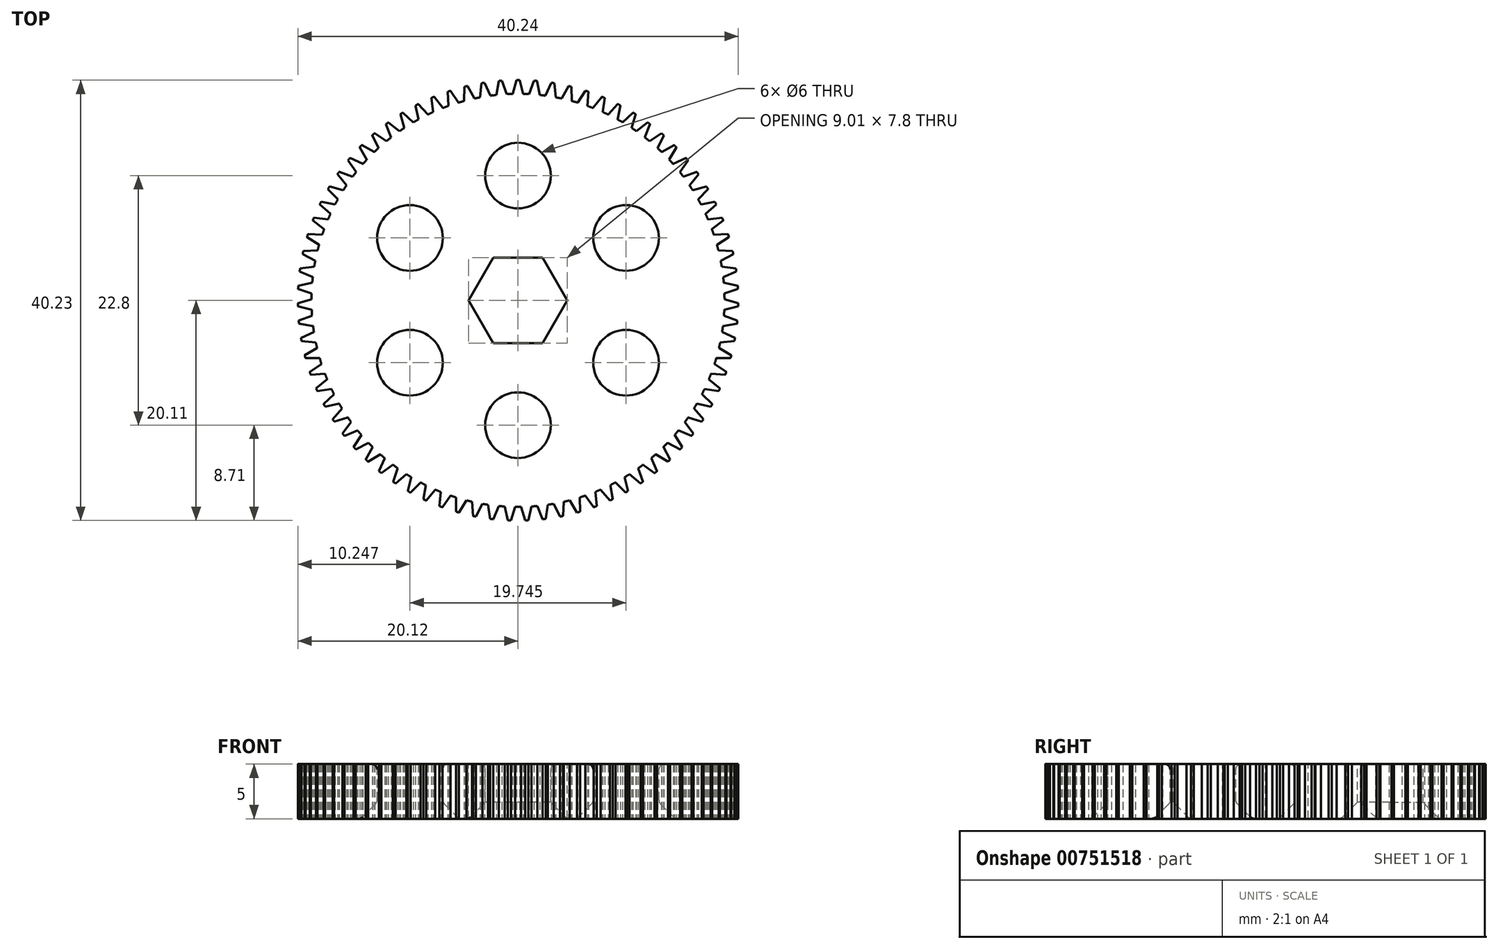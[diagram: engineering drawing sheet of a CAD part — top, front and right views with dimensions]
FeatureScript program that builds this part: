
annotation { "Feature Type Name" : "Feature", "Feature Type Description" : "" }
export const myFeature = defineFeature(function(context is Context, id is Id, definition is map)
    precondition{}
    {
        {
            assignVariable(context, id + "F0", {"name" : "GearHeight", "anyValue" : 5 * mm});
        }
        {
            assignVariable(context, id + "F1", {"name" : "teeth", "anyValue" : 79});
        }
        {
            var Q0;
            Q0=qCreatedBy(makeId("Top.planeOp"),FACE);
            var sketch = newSketch(context, id + "F2", { "sketchPlane" : qUnion([Q0])});
            skCircle(sketch, "E0", {"center": v(0, 0) * mm, "radius": 18.87 * mm});
            skCircle(sketch, "E1", {"center": v(0, 0) * mm, "radius": 20.12 * mm});
            skLineSegment(sketch, "E2", {"start": v(0.48, 18.86) * mm, "end": v(0.14, 20.12) * mm});
            skLineSegment(sketch, "E3", {"start": v(-0.48, 18.86) * mm, "end": v(-0.14, 20.12) * mm});
            skLineSegment(sketch, "E4", {"start": v(0, 0) * mm, "end": v(0, 64.06) * mm, "construction": true});
            skArc(sketch, "E5", {"start": v(-0.48, 18.86) * mm, "mid": v(-0.24, 18.87) * mm, "end": v(0, 18.87) * mm});
            skArc(sketch, "E6", {"start": v(0.48, 18.86) * mm, "mid": v(0.24, 18.87) * mm, "end": v(0, 18.87) * mm});
            skCircle(sketch, "E7", {"center": v(0, 0) * mm, "radius": 19.5 * mm, "construction": true});
            skPoint(sketch, "E8", {"position": v(-0.31, 19.5) * mm});
            skArc(sketch, "E9", {"start": v(0.14, 20.12) * mm, "mid": v(0.07, 20.12) * mm, "end": v(0, 20.12) * mm});
            skArc(sketch, "E10", {"start": v(-0.14, 20.12) * mm, "mid": v(-0.07, 20.12) * mm, "end": v(0, 20.12) * mm});
            skPoint(sketch, "E11", {"position": v(0.31, 19.5) * mm});
            skSolve(sketch);
        }
        {
            var Q0;
            Q0=qCreatedBy(makeId("Right.planeOp"),FACE);
            var sketch = newSketch(context, id + "F3", { "sketchPlane" : qUnion([Q0])});
            skLineSegment(sketch, "E12", {"start": v(0, 16.96) * mm, "end": v(0, -9.96) * mm, "construction": true});
            skSolve(sketch);
        }
        {
            var Q0;
            {var subQ0=sQuery(id+"F2.wireOp",EDGE,"E0");var subQ1=makeQuery(id+"F2.imprint","INTERSECT",VERTEX,{"derivedFrom":[subQ0,sQuery(id+"F2.wireOp",EDGE,"E2")]});Q0=makeQuery(id+"F2.imprint","IMPRINT",FACE,{"disambiguationData":[TD([[makeQuery(id+"F2.imprint","IMPRINT",EDGE,{"disambiguationData":[TD([[subQ1,-1.0]])],"derivedFrom":subQ0}),1.0]])]});}
            extrude(context, id + "F4", {"entities" : qUnion([Q0]), "depth" : getVariable(context, 'GearHeight'), "offsetDistance" : 25 * mm});
        }
        {
            var Q0;
            {var subQ0=sQuery(id+"F2.wireOp",EDGE,"E2");Q0=makeQuery(id+"F2.imprint","IMPRINT",FACE,{"disambiguationData":[TD([[makeQuery(id+"F2.imprint","IMPRINT",EDGE,{"derivedFrom":subQ0}),1.0]])]});}
            extrude(context, id + "F5", {"entities" : qUnion([Q0]), "operationType" : NewBodyOperationType.ADD, "depth" : getVariable(context, 'GearHeight'), "offsetDistance" : 25 * mm});
        }
        {
            var Q0;
            Q0=makeQuery(id+"F4.opExtrude","SWEPT_BODY",BODY,{"disambiguationData":[OSD([sQuery(id+"F2.wireOp",EDGE,"E0")])]});
            var Q1;
            Q1=sQuery(id+"F3.wireOp",EDGE,"E12");
            circularPattern(context, id + "F6", {"operationType" : NewBodyOperationType.ADD, "entities" : qUnion([Q0]), "axis" : qUnion([Q1]), "angle" : 360 * degree, "instanceCount" : getVariable(context, 'teeth'), "equalSpace" : true});
        }
        {
            var Q0;
            {var subQ0=sQuery(id+"F2.wireOp",EDGE,"E0");var subQ1=makeQuery(id+"F5.boolean.opBoolean","MERGE",FACE,{"derivedFrom":[makeQuery(id+"F4.opExtrude","CAP_FACE",FACE,{"disambiguationData":[OSD([subQ0])],"isStart":false}),makeQuery(id+"F5.opExtrude","CAP_FACE",FACE,{"disambiguationData":[OSD([subQ0,sQuery(id+"F2.wireOp",EDGE,"E1"),sQuery(id+"F2.wireOp",EDGE,"E2"),sQuery(id+"F2.wireOp",EDGE,"E3")])],"isStart":false})]});Q0=makeQuery(id+"F6.boolean.opBoolean","MERGE",FACE,{"derivedFrom":[subQ1,makeQuery(id+"F6.opPattern","COPY",FACE,{"derivedFrom":subQ1,"instanceName":"1"}),makeQuery(id+"F6.opPattern","COPY",FACE,{"derivedFrom":subQ1,"instanceName":"2"}),makeQuery(id+"F6.opPattern","COPY",FACE,{"derivedFrom":subQ1,"instanceName":"3"}),makeQuery(id+"F6.opPattern","COPY",FACE,{"derivedFrom":subQ1,"instanceName":"4"}),makeQuery(id+"F6.opPattern","COPY",FACE,{"derivedFrom":subQ1,"instanceName":"5"}),makeQuery(id+"F6.opPattern","COPY",FACE,{"derivedFrom":subQ1,"instanceName":"6"}),makeQuery(id+"F6.opPattern","COPY",FACE,{"derivedFrom":subQ1,"instanceName":"7"}),makeQuery(id+"F6.opPattern","COPY",FACE,{"derivedFrom":subQ1,"instanceName":"8"}),makeQuery(id+"F6.opPattern","COPY",FACE,{"derivedFrom":subQ1,"instanceName":"9"}),makeQuery(id+"F6.opPattern","COPY",FACE,{"derivedFrom":subQ1,"instanceName":"10"}),makeQuery(id+"F6.opPattern","COPY",FACE,{"derivedFrom":subQ1,"instanceName":"11"}),makeQuery(id+"F6.opPattern","COPY",FACE,{"derivedFrom":subQ1,"instanceName":"12"}),makeQuery(id+"F6.opPattern","COPY",FACE,{"derivedFrom":subQ1,"instanceName":"13"}),makeQuery(id+"F6.opPattern","COPY",FACE,{"derivedFrom":subQ1,"instanceName":"14"}),makeQuery(id+"F6.opPattern","COPY",FACE,{"derivedFrom":subQ1,"instanceName":"15"}),makeQuery(id+"F6.opPattern","COPY",FACE,{"derivedFrom":subQ1,"instanceName":"16"}),makeQuery(id+"F6.opPattern","COPY",FACE,{"derivedFrom":subQ1,"instanceName":"17"}),makeQuery(id+"F6.opPattern","COPY",FACE,{"derivedFrom":subQ1,"instanceName":"18"}),makeQuery(id+"F6.opPattern","COPY",FACE,{"derivedFrom":subQ1,"instanceName":"19"}),makeQuery(id+"F6.opPattern","COPY",FACE,{"derivedFrom":subQ1,"instanceName":"20"}),makeQuery(id+"F6.opPattern","COPY",FACE,{"derivedFrom":subQ1,"instanceName":"21"}),makeQuery(id+"F6.opPattern","COPY",FACE,{"derivedFrom":subQ1,"instanceName":"22"}),makeQuery(id+"F6.opPattern","COPY",FACE,{"derivedFrom":subQ1,"instanceName":"23"}),makeQuery(id+"F6.opPattern","COPY",FACE,{"derivedFrom":subQ1,"instanceName":"24"})]});}
            var sketch = newSketch(context, id + "F7", { "sketchPlane" : qUnion([Q0])});
            skCircle(sketch, "E13.cCircle", {"center": v(0, 0) * mm, "radius": 3.9 * mm, "construction": true});
            skLineSegment(sketch, "E13.0", {"start": v(-2.25, 3.9) * mm, "end": v(2.25, 3.9) * mm});
            skLineSegment(sketch, "E13.1", {"start": v(2.25, 3.9) * mm, "end": v(4.5, 0) * mm});
            skLineSegment(sketch, "E13.2", {"start": v(4.5, 0) * mm, "end": v(2.25, -3.9) * mm});
            skLineSegment(sketch, "E13.3", {"start": v(2.25, -3.9) * mm, "end": v(-2.25, -3.9) * mm});
            skLineSegment(sketch, "E13.4", {"start": v(-2.25, -3.9) * mm, "end": v(-4.5, 0) * mm});
            skLineSegment(sketch, "E13.5", {"start": v(-4.5, 0) * mm, "end": v(-2.25, 3.9) * mm});
            skPoint(sketch, "E13.0.midPoint", {"position": v(0, 3.9) * mm});
            skCircle(sketch, "E14", {"center": v(0, 11.4) * mm, "radius": 3 * mm});
            skCircle(sketch, "E15.1.0", {"center": v(-9.87, 5.7) * mm, "radius": 3 * mm});
            skCircle(sketch, "E15.2.0", {"center": v(-9.87, -5.7) * mm, "radius": 3 * mm});
            skCircle(sketch, "E16.1.3.0", {"center": v(0, -11.4) * mm, "radius": 3 * mm});
            skCircle(sketch, "E16.1.4.0", {"center": v(9.87, -5.7) * mm, "radius": 3 * mm});
            skCircle(sketch, "E16.1.5.0", {"center": v(9.87, 5.7) * mm, "radius": 3 * mm});
            skSolve(sketch);
        }
        {
            var Q0;
            Q0=makeQuery(id+"F7.imprint","IMPRINT",FACE,{"disambiguationData":[TD([[makeQuery(id+"F7.imprint","IMPRINT",EDGE,{"derivedFrom":sQuery(id+"F7.wireOp",EDGE,"E13.0")}),-1.0]])]});
            var Q1;
            Q1=makeQuery(id+"F7.imprint","IMPRINT",FACE,{"disambiguationData":[TD([[makeQuery(id+"F7.imprint","IMPRINT",EDGE,{"derivedFrom":sQuery(id+"F7.wireOp",EDGE,"E14")}),1.0]])]});
            var Q2;
            Q2=makeQuery(id+"F7.imprint","IMPRINT",FACE,{"disambiguationData":[TD([[makeQuery(id+"F7.imprint","IMPRINT",EDGE,{"derivedFrom":sQuery(id+"F7.wireOp",EDGE,"E15.1.0")}),1.0]])]});
            var Q3;
            Q3=makeQuery(id+"F7.imprint","IMPRINT",FACE,{"disambiguationData":[TD([[makeQuery(id+"F7.imprint","IMPRINT",EDGE,{"derivedFrom":sQuery(id+"F7.wireOp",EDGE,"E15.2.0")}),1.0]])]});
            var Q4;
            Q4=makeQuery(id+"F7.imprint","IMPRINT",FACE,{"disambiguationData":[TD([[makeQuery(id+"F7.imprint","IMPRINT",EDGE,{"derivedFrom":sQuery(id+"F7.wireOp",EDGE,"E16.1.3.0")}),1.0]])]});
            var Q5;
            Q5=makeQuery(id+"F7.imprint","IMPRINT",FACE,{"disambiguationData":[TD([[makeQuery(id+"F7.imprint","IMPRINT",EDGE,{"derivedFrom":sQuery(id+"F7.wireOp",EDGE,"E16.1.4.0")}),1.0]])]});
            var Q6;
            Q6=makeQuery(id+"F7.imprint","IMPRINT",FACE,{"disambiguationData":[TD([[makeQuery(id+"F7.imprint","IMPRINT",EDGE,{"derivedFrom":sQuery(id+"F7.wireOp",EDGE,"E16.1.5.0")}),1.0]])]});
            extrude(context, id + "F8", {"entities" : qUnion([Q0, Q1, Q2, Q3, Q4, Q5, Q6]), "operationType" : NewBodyOperationType.REMOVE, "endBound" : BoundingType.THROUGH_ALL, "oppositeDirection" : true, "depth" : 25 * mm, "offsetDistance" : 25 * mm});
        }
        {
            var Q0;
            Q0=makeQuery(id+"F8.boolean.opBoolean","COPY",EDGE,{"derivedFrom":makeQuery(id+"F8.opExtrude","CAP_EDGE",EDGE,{"disambiguationData":[OSD([sQuery(id+"F7.wireOp",EDGE,"E14")])],"isStart":true})});
            var Q1;
            Q1=makeQuery(id+"F8.boolean.opBoolean","COPY",EDGE,{"derivedFrom":makeQuery(id+"F8.opExtrude","CAP_EDGE",EDGE,{"disambiguationData":[OSD([sQuery(id+"F7.wireOp",EDGE,"E15.1.0")])],"isStart":true})});
            var Q2;
            Q2=makeQuery(id+"F8.boolean.opBoolean","COPY",EDGE,{"derivedFrom":makeQuery(id+"F8.opExtrude","CAP_EDGE",EDGE,{"disambiguationData":[OSD([sQuery(id+"F7.wireOp",EDGE,"E16.1.5.0")])],"isStart":true})});
            var Q3;
            Q3=makeQuery(id+"F8.boolean.opBoolean","COPY",EDGE,{"derivedFrom":makeQuery(id+"F8.opExtrude","CAP_EDGE",EDGE,{"disambiguationData":[OSD([sQuery(id+"F7.wireOp",EDGE,"E16.1.4.0")])],"isStart":true})});
            var Q4;
            Q4=makeQuery(id+"F8.boolean.opBoolean","COPY",EDGE,{"derivedFrom":makeQuery(id+"F8.opExtrude","CAP_EDGE",EDGE,{"disambiguationData":[OSD([sQuery(id+"F7.wireOp",EDGE,"E16.1.3.0")])],"isStart":true})});
            var Q5;
            Q5=makeQuery(id+"F8.boolean.opBoolean","COPY",EDGE,{"derivedFrom":makeQuery(id+"F8.opExtrude","CAP_EDGE",EDGE,{"disambiguationData":[OSD([sQuery(id+"F7.wireOp",EDGE,"E15.2.0")])],"isStart":true})});
            var Q6;
            {var subQ0=sQuery(id+"F2.wireOp",EDGE,"E0");var subQ1=makeQuery(id+"F5.boolean.opBoolean","MERGE",FACE,{"derivedFrom":[makeQuery(id+"F4.opExtrude","CAP_FACE",FACE,{"disambiguationData":[OSD([subQ0])],"isStart":true}),makeQuery(id+"F5.opExtrude","CAP_FACE",FACE,{"disambiguationData":[OSD([subQ0,sQuery(id+"F2.wireOp",EDGE,"E1"),sQuery(id+"F2.wireOp",EDGE,"E2"),sQuery(id+"F2.wireOp",EDGE,"E3")])],"isStart":true})]});Q6=makeQuery(id+"F8.boolean.opBoolean","INTERSECT",EDGE,{"derivedFrom":[makeQuery(id+"F6.boolean.opBoolean","MERGE",FACE,{"derivedFrom":[subQ1,makeQuery(id+"F6.opPattern","COPY",FACE,{"derivedFrom":subQ1,"instanceName":"1"}),makeQuery(id+"F6.opPattern","COPY",FACE,{"derivedFrom":subQ1,"instanceName":"2"}),makeQuery(id+"F6.opPattern","COPY",FACE,{"derivedFrom":subQ1,"instanceName":"3"}),makeQuery(id+"F6.opPattern","COPY",FACE,{"derivedFrom":subQ1,"instanceName":"4"}),makeQuery(id+"F6.opPattern","COPY",FACE,{"derivedFrom":subQ1,"instanceName":"5"}),makeQuery(id+"F6.opPattern","COPY",FACE,{"derivedFrom":subQ1,"instanceName":"6"}),makeQuery(id+"F6.opPattern","COPY",FACE,{"derivedFrom":subQ1,"instanceName":"7"}),makeQuery(id+"F6.opPattern","COPY",FACE,{"derivedFrom":subQ1,"instanceName":"8"}),makeQuery(id+"F6.opPattern","COPY",FACE,{"derivedFrom":subQ1,"instanceName":"9"}),makeQuery(id+"F6.opPattern","COPY",FACE,{"derivedFrom":subQ1,"instanceName":"10"}),makeQuery(id+"F6.opPattern","COPY",FACE,{"derivedFrom":subQ1,"instanceName":"11"}),makeQuery(id+"F6.opPattern","COPY",FACE,{"derivedFrom":subQ1,"instanceName":"12"}),makeQuery(id+"F6.opPattern","COPY",FACE,{"derivedFrom":subQ1,"instanceName":"13"}),makeQuery(id+"F6.opPattern","COPY",FACE,{"derivedFrom":subQ1,"instanceName":"14"}),makeQuery(id+"F6.opPattern","COPY",FACE,{"derivedFrom":subQ1,"instanceName":"15"}),makeQuery(id+"F6.opPattern","COPY",FACE,{"derivedFrom":subQ1,"instanceName":"16"}),makeQuery(id+"F6.opPattern","COPY",FACE,{"derivedFrom":subQ1,"instanceName":"17"}),makeQuery(id+"F6.opPattern","COPY",FACE,{"derivedFrom":subQ1,"instanceName":"18"}),makeQuery(id+"F6.opPattern","COPY",FACE,{"derivedFrom":subQ1,"instanceName":"19"}),makeQuery(id+"F6.opPattern","COPY",FACE,{"derivedFrom":subQ1,"instanceName":"20"}),makeQuery(id+"F6.opPattern","COPY",FACE,{"derivedFrom":subQ1,"instanceName":"21"}),makeQuery(id+"F6.opPattern","COPY",FACE,{"derivedFrom":subQ1,"instanceName":"22"}),makeQuery(id+"F6.opPattern","COPY",FACE,{"derivedFrom":subQ1,"instanceName":"23"}),makeQuery(id+"F6.opPattern","COPY",FACE,{"derivedFrom":subQ1,"instanceName":"24"}),makeQuery(id+"F6.opPattern","COPY",FACE,{"derivedFrom":subQ1,"instanceName":"25"}),makeQuery(id+"F6.opPattern","COPY",FACE,{"derivedFrom":subQ1,"instanceName":"26"}),makeQuery(id+"F6.opPattern","COPY",FACE,{"derivedFrom":subQ1,"instanceName":"27"}),makeQuery(id+"F6.opPattern","COPY",FACE,{"derivedFrom":subQ1,"instanceName":"28"}),makeQuery(id+"F6.opPattern","COPY",FACE,{"derivedFrom":subQ1,"instanceName":"29"}),makeQuery(id+"F6.opPattern","COPY",FACE,{"derivedFrom":subQ1,"instanceName":"30"}),makeQuery(id+"F6.opPattern","COPY",FACE,{"derivedFrom":subQ1,"instanceName":"31"}),makeQuery(id+"F6.opPattern","COPY",FACE,{"derivedFrom":subQ1,"instanceName":"32"}),makeQuery(id+"F6.opPattern","COPY",FACE,{"derivedFrom":subQ1,"instanceName":"33"}),makeQuery(id+"F6.opPattern","COPY",FACE,{"derivedFrom":subQ1,"instanceName":"34"}),makeQuery(id+"F6.opPattern","COPY",FACE,{"derivedFrom":subQ1,"instanceName":"35"}),makeQuery(id+"F6.opPattern","COPY",FACE,{"derivedFrom":subQ1,"instanceName":"36"}),makeQuery(id+"F6.opPattern","COPY",FACE,{"derivedFrom":subQ1,"instanceName":"37"}),makeQuery(id+"F6.opPattern","COPY",FACE,{"derivedFrom":subQ1,"instanceName":"38"}),makeQuery(id+"F6.opPattern","COPY",FACE,{"derivedFrom":subQ1,"instanceName":"39"}),makeQuery(id+"F6.opPattern","COPY",FACE,{"derivedFrom":subQ1,"instanceName":"40"}),makeQuery(id+"F6.opPattern","COPY",FACE,{"derivedFrom":subQ1,"instanceName":"41"}),makeQuery(id+"F6.opPattern","COPY",FACE,{"derivedFrom":subQ1,"instanceName":"42"}),makeQuery(id+"F6.opPattern","COPY",FACE,{"derivedFrom":subQ1,"instanceName":"43"}),makeQuery(id+"F6.opPattern","COPY",FACE,{"derivedFrom":subQ1,"instanceName":"44"}),makeQuery(id+"F6.opPattern","COPY",FACE,{"derivedFrom":subQ1,"instanceName":"45"}),makeQuery(id+"F6.opPattern","COPY",FACE,{"derivedFrom":subQ1,"instanceName":"46"}),makeQuery(id+"F6.opPattern","COPY",FACE,{"derivedFrom":subQ1,"instanceName":"47"}),makeQuery(id+"F6.opPattern","COPY",FACE,{"derivedFrom":subQ1,"instanceName":"48"}),makeQuery(id+"F6.opPattern","COPY",FACE,{"derivedFrom":subQ1,"instanceName":"49"}),makeQuery(id+"F6.opPattern","COPY",FACE,{"derivedFrom":subQ1,"instanceName":"50"}),makeQuery(id+"F6.opPattern","COPY",FACE,{"derivedFrom":subQ1,"instanceName":"51"}),makeQuery(id+"F6.opPattern","COPY",FACE,{"derivedFrom":subQ1,"instanceName":"52"}),makeQuery(id+"F6.opPattern","COPY",FACE,{"derivedFrom":subQ1,"instanceName":"53"}),makeQuery(id+"F6.opPattern","COPY",FACE,{"derivedFrom":subQ1,"instanceName":"54"}),makeQuery(id+"F6.opPattern","COPY",FACE,{"derivedFrom":subQ1,"instanceName":"55"}),makeQuery(id+"F6.opPattern","COPY",FACE,{"derivedFrom":subQ1,"instanceName":"56"}),makeQuery(id+"F6.opPattern","COPY",FACE,{"derivedFrom":subQ1,"instanceName":"57"}),makeQuery(id+"F6.opPattern","COPY",FACE,{"derivedFrom":subQ1,"instanceName":"58"}),makeQuery(id+"F6.opPattern","COPY",FACE,{"derivedFrom":subQ1,"instanceName":"59"}),makeQuery(id+"F6.opPattern","COPY",FACE,{"derivedFrom":subQ1,"instanceName":"60"}),makeQuery(id+"F6.opPattern","COPY",FACE,{"derivedFrom":subQ1,"instanceName":"61"}),makeQuery(id+"F6.opPattern","COPY",FACE,{"derivedFrom":subQ1,"instanceName":"62"}),makeQuery(id+"F6.opPattern","COPY",FACE,{"derivedFrom":subQ1,"instanceName":"63"}),makeQuery(id+"F6.opPattern","COPY",FACE,{"derivedFrom":subQ1,"instanceName":"64"}),makeQuery(id+"F6.opPattern","COPY",FACE,{"derivedFrom":subQ1,"instanceName":"65"}),makeQuery(id+"F6.opPattern","COPY",FACE,{"derivedFrom":subQ1,"instanceName":"66"}),makeQuery(id+"F6.opPattern","COPY",FACE,{"derivedFrom":subQ1,"instanceName":"67"}),makeQuery(id+"F6.opPattern","COPY",FACE,{"derivedFrom":subQ1,"instanceName":"68"}),makeQuery(id+"F6.opPattern","COPY",FACE,{"derivedFrom":subQ1,"instanceName":"69"}),makeQuery(id+"F6.opPattern","COPY",FACE,{"derivedFrom":subQ1,"instanceName":"70"}),makeQuery(id+"F6.opPattern","COPY",FACE,{"derivedFrom":subQ1,"instanceName":"71"}),makeQuery(id+"F6.opPattern","COPY",FACE,{"derivedFrom":subQ1,"instanceName":"72"}),makeQuery(id+"F6.opPattern","COPY",FACE,{"derivedFrom":subQ1,"instanceName":"73"}),makeQuery(id+"F6.opPattern","COPY",FACE,{"derivedFrom":subQ1,"instanceName":"74"}),makeQuery(id+"F6.opPattern","COPY",FACE,{"derivedFrom":subQ1,"instanceName":"75"}),makeQuery(id+"F6.opPattern","COPY",FACE,{"derivedFrom":subQ1,"instanceName":"76"}),makeQuery(id+"F6.opPattern","COPY",FACE,{"derivedFrom":subQ1,"instanceName":"77"}),makeQuery(id+"F6.opPattern","COPY",FACE,{"derivedFrom":subQ1,"instanceName":"78"})]}),makeQuery(id+"F8.opExtrude","SWEPT_FACE",FACE,{"disambiguationData":[OSD([sQuery(id+"F7.wireOp",EDGE,"E16.1.3.0")])]})]});}
            var Q7;
            {var subQ0=sQuery(id+"F2.wireOp",EDGE,"E0");var subQ1=makeQuery(id+"F5.boolean.opBoolean","MERGE",FACE,{"derivedFrom":[makeQuery(id+"F4.opExtrude","CAP_FACE",FACE,{"disambiguationData":[OSD([subQ0])],"isStart":true}),makeQuery(id+"F5.opExtrude","CAP_FACE",FACE,{"disambiguationData":[OSD([subQ0,sQuery(id+"F2.wireOp",EDGE,"E1"),sQuery(id+"F2.wireOp",EDGE,"E2"),sQuery(id+"F2.wireOp",EDGE,"E3")])],"isStart":true})]});Q7=makeQuery(id+"F8.boolean.opBoolean","INTERSECT",EDGE,{"derivedFrom":[makeQuery(id+"F6.boolean.opBoolean","MERGE",FACE,{"derivedFrom":[subQ1,makeQuery(id+"F6.opPattern","COPY",FACE,{"derivedFrom":subQ1,"instanceName":"1"}),makeQuery(id+"F6.opPattern","COPY",FACE,{"derivedFrom":subQ1,"instanceName":"2"}),makeQuery(id+"F6.opPattern","COPY",FACE,{"derivedFrom":subQ1,"instanceName":"3"}),makeQuery(id+"F6.opPattern","COPY",FACE,{"derivedFrom":subQ1,"instanceName":"4"}),makeQuery(id+"F6.opPattern","COPY",FACE,{"derivedFrom":subQ1,"instanceName":"5"}),makeQuery(id+"F6.opPattern","COPY",FACE,{"derivedFrom":subQ1,"instanceName":"6"}),makeQuery(id+"F6.opPattern","COPY",FACE,{"derivedFrom":subQ1,"instanceName":"7"}),makeQuery(id+"F6.opPattern","COPY",FACE,{"derivedFrom":subQ1,"instanceName":"8"}),makeQuery(id+"F6.opPattern","COPY",FACE,{"derivedFrom":subQ1,"instanceName":"9"}),makeQuery(id+"F6.opPattern","COPY",FACE,{"derivedFrom":subQ1,"instanceName":"10"}),makeQuery(id+"F6.opPattern","COPY",FACE,{"derivedFrom":subQ1,"instanceName":"11"}),makeQuery(id+"F6.opPattern","COPY",FACE,{"derivedFrom":subQ1,"instanceName":"12"}),makeQuery(id+"F6.opPattern","COPY",FACE,{"derivedFrom":subQ1,"instanceName":"13"}),makeQuery(id+"F6.opPattern","COPY",FACE,{"derivedFrom":subQ1,"instanceName":"14"}),makeQuery(id+"F6.opPattern","COPY",FACE,{"derivedFrom":subQ1,"instanceName":"15"}),makeQuery(id+"F6.opPattern","COPY",FACE,{"derivedFrom":subQ1,"instanceName":"16"}),makeQuery(id+"F6.opPattern","COPY",FACE,{"derivedFrom":subQ1,"instanceName":"17"}),makeQuery(id+"F6.opPattern","COPY",FACE,{"derivedFrom":subQ1,"instanceName":"18"}),makeQuery(id+"F6.opPattern","COPY",FACE,{"derivedFrom":subQ1,"instanceName":"19"}),makeQuery(id+"F6.opPattern","COPY",FACE,{"derivedFrom":subQ1,"instanceName":"20"}),makeQuery(id+"F6.opPattern","COPY",FACE,{"derivedFrom":subQ1,"instanceName":"21"}),makeQuery(id+"F6.opPattern","COPY",FACE,{"derivedFrom":subQ1,"instanceName":"22"}),makeQuery(id+"F6.opPattern","COPY",FACE,{"derivedFrom":subQ1,"instanceName":"23"}),makeQuery(id+"F6.opPattern","COPY",FACE,{"derivedFrom":subQ1,"instanceName":"24"}),makeQuery(id+"F6.opPattern","COPY",FACE,{"derivedFrom":subQ1,"instanceName":"25"}),makeQuery(id+"F6.opPattern","COPY",FACE,{"derivedFrom":subQ1,"instanceName":"26"}),makeQuery(id+"F6.opPattern","COPY",FACE,{"derivedFrom":subQ1,"instanceName":"27"}),makeQuery(id+"F6.opPattern","COPY",FACE,{"derivedFrom":subQ1,"instanceName":"28"}),makeQuery(id+"F6.opPattern","COPY",FACE,{"derivedFrom":subQ1,"instanceName":"29"}),makeQuery(id+"F6.opPattern","COPY",FACE,{"derivedFrom":subQ1,"instanceName":"30"}),makeQuery(id+"F6.opPattern","COPY",FACE,{"derivedFrom":subQ1,"instanceName":"31"}),makeQuery(id+"F6.opPattern","COPY",FACE,{"derivedFrom":subQ1,"instanceName":"32"}),makeQuery(id+"F6.opPattern","COPY",FACE,{"derivedFrom":subQ1,"instanceName":"33"}),makeQuery(id+"F6.opPattern","COPY",FACE,{"derivedFrom":subQ1,"instanceName":"34"}),makeQuery(id+"F6.opPattern","COPY",FACE,{"derivedFrom":subQ1,"instanceName":"35"}),makeQuery(id+"F6.opPattern","COPY",FACE,{"derivedFrom":subQ1,"instanceName":"36"}),makeQuery(id+"F6.opPattern","COPY",FACE,{"derivedFrom":subQ1,"instanceName":"37"}),makeQuery(id+"F6.opPattern","COPY",FACE,{"derivedFrom":subQ1,"instanceName":"38"}),makeQuery(id+"F6.opPattern","COPY",FACE,{"derivedFrom":subQ1,"instanceName":"39"}),makeQuery(id+"F6.opPattern","COPY",FACE,{"derivedFrom":subQ1,"instanceName":"40"}),makeQuery(id+"F6.opPattern","COPY",FACE,{"derivedFrom":subQ1,"instanceName":"41"}),makeQuery(id+"F6.opPattern","COPY",FACE,{"derivedFrom":subQ1,"instanceName":"42"}),makeQuery(id+"F6.opPattern","COPY",FACE,{"derivedFrom":subQ1,"instanceName":"43"}),makeQuery(id+"F6.opPattern","COPY",FACE,{"derivedFrom":subQ1,"instanceName":"44"}),makeQuery(id+"F6.opPattern","COPY",FACE,{"derivedFrom":subQ1,"instanceName":"45"}),makeQuery(id+"F6.opPattern","COPY",FACE,{"derivedFrom":subQ1,"instanceName":"46"}),makeQuery(id+"F6.opPattern","COPY",FACE,{"derivedFrom":subQ1,"instanceName":"47"}),makeQuery(id+"F6.opPattern","COPY",FACE,{"derivedFrom":subQ1,"instanceName":"48"}),makeQuery(id+"F6.opPattern","COPY",FACE,{"derivedFrom":subQ1,"instanceName":"49"}),makeQuery(id+"F6.opPattern","COPY",FACE,{"derivedFrom":subQ1,"instanceName":"50"}),makeQuery(id+"F6.opPattern","COPY",FACE,{"derivedFrom":subQ1,"instanceName":"51"}),makeQuery(id+"F6.opPattern","COPY",FACE,{"derivedFrom":subQ1,"instanceName":"52"}),makeQuery(id+"F6.opPattern","COPY",FACE,{"derivedFrom":subQ1,"instanceName":"53"}),makeQuery(id+"F6.opPattern","COPY",FACE,{"derivedFrom":subQ1,"instanceName":"54"}),makeQuery(id+"F6.opPattern","COPY",FACE,{"derivedFrom":subQ1,"instanceName":"55"}),makeQuery(id+"F6.opPattern","COPY",FACE,{"derivedFrom":subQ1,"instanceName":"56"}),makeQuery(id+"F6.opPattern","COPY",FACE,{"derivedFrom":subQ1,"instanceName":"57"}),makeQuery(id+"F6.opPattern","COPY",FACE,{"derivedFrom":subQ1,"instanceName":"58"}),makeQuery(id+"F6.opPattern","COPY",FACE,{"derivedFrom":subQ1,"instanceName":"59"}),makeQuery(id+"F6.opPattern","COPY",FACE,{"derivedFrom":subQ1,"instanceName":"60"}),makeQuery(id+"F6.opPattern","COPY",FACE,{"derivedFrom":subQ1,"instanceName":"61"}),makeQuery(id+"F6.opPattern","COPY",FACE,{"derivedFrom":subQ1,"instanceName":"62"}),makeQuery(id+"F6.opPattern","COPY",FACE,{"derivedFrom":subQ1,"instanceName":"63"}),makeQuery(id+"F6.opPattern","COPY",FACE,{"derivedFrom":subQ1,"instanceName":"64"}),makeQuery(id+"F6.opPattern","COPY",FACE,{"derivedFrom":subQ1,"instanceName":"65"}),makeQuery(id+"F6.opPattern","COPY",FACE,{"derivedFrom":subQ1,"instanceName":"66"}),makeQuery(id+"F6.opPattern","COPY",FACE,{"derivedFrom":subQ1,"instanceName":"67"}),makeQuery(id+"F6.opPattern","COPY",FACE,{"derivedFrom":subQ1,"instanceName":"68"}),makeQuery(id+"F6.opPattern","COPY",FACE,{"derivedFrom":subQ1,"instanceName":"69"}),makeQuery(id+"F6.opPattern","COPY",FACE,{"derivedFrom":subQ1,"instanceName":"70"}),makeQuery(id+"F6.opPattern","COPY",FACE,{"derivedFrom":subQ1,"instanceName":"71"}),makeQuery(id+"F6.opPattern","COPY",FACE,{"derivedFrom":subQ1,"instanceName":"72"}),makeQuery(id+"F6.opPattern","COPY",FACE,{"derivedFrom":subQ1,"instanceName":"73"}),makeQuery(id+"F6.opPattern","COPY",FACE,{"derivedFrom":subQ1,"instanceName":"74"}),makeQuery(id+"F6.opPattern","COPY",FACE,{"derivedFrom":subQ1,"instanceName":"75"}),makeQuery(id+"F6.opPattern","COPY",FACE,{"derivedFrom":subQ1,"instanceName":"76"}),makeQuery(id+"F6.opPattern","COPY",FACE,{"derivedFrom":subQ1,"instanceName":"77"}),makeQuery(id+"F6.opPattern","COPY",FACE,{"derivedFrom":subQ1,"instanceName":"78"})]}),makeQuery(id+"F8.opExtrude","SWEPT_FACE",FACE,{"disambiguationData":[OSD([sQuery(id+"F7.wireOp",EDGE,"E15.2.0")])]})]});}
            var Q8;
            {var subQ0=sQuery(id+"F2.wireOp",EDGE,"E0");var subQ1=makeQuery(id+"F5.boolean.opBoolean","MERGE",FACE,{"derivedFrom":[makeQuery(id+"F4.opExtrude","CAP_FACE",FACE,{"disambiguationData":[OSD([subQ0])],"isStart":true}),makeQuery(id+"F5.opExtrude","CAP_FACE",FACE,{"disambiguationData":[OSD([subQ0,sQuery(id+"F2.wireOp",EDGE,"E1"),sQuery(id+"F2.wireOp",EDGE,"E2"),sQuery(id+"F2.wireOp",EDGE,"E3")])],"isStart":true})]});Q8=makeQuery(id+"F8.boolean.opBoolean","INTERSECT",EDGE,{"derivedFrom":[makeQuery(id+"F6.boolean.opBoolean","MERGE",FACE,{"derivedFrom":[subQ1,makeQuery(id+"F6.opPattern","COPY",FACE,{"derivedFrom":subQ1,"instanceName":"1"}),makeQuery(id+"F6.opPattern","COPY",FACE,{"derivedFrom":subQ1,"instanceName":"2"}),makeQuery(id+"F6.opPattern","COPY",FACE,{"derivedFrom":subQ1,"instanceName":"3"}),makeQuery(id+"F6.opPattern","COPY",FACE,{"derivedFrom":subQ1,"instanceName":"4"}),makeQuery(id+"F6.opPattern","COPY",FACE,{"derivedFrom":subQ1,"instanceName":"5"}),makeQuery(id+"F6.opPattern","COPY",FACE,{"derivedFrom":subQ1,"instanceName":"6"}),makeQuery(id+"F6.opPattern","COPY",FACE,{"derivedFrom":subQ1,"instanceName":"7"}),makeQuery(id+"F6.opPattern","COPY",FACE,{"derivedFrom":subQ1,"instanceName":"8"}),makeQuery(id+"F6.opPattern","COPY",FACE,{"derivedFrom":subQ1,"instanceName":"9"}),makeQuery(id+"F6.opPattern","COPY",FACE,{"derivedFrom":subQ1,"instanceName":"10"}),makeQuery(id+"F6.opPattern","COPY",FACE,{"derivedFrom":subQ1,"instanceName":"11"}),makeQuery(id+"F6.opPattern","COPY",FACE,{"derivedFrom":subQ1,"instanceName":"12"}),makeQuery(id+"F6.opPattern","COPY",FACE,{"derivedFrom":subQ1,"instanceName":"13"}),makeQuery(id+"F6.opPattern","COPY",FACE,{"derivedFrom":subQ1,"instanceName":"14"}),makeQuery(id+"F6.opPattern","COPY",FACE,{"derivedFrom":subQ1,"instanceName":"15"}),makeQuery(id+"F6.opPattern","COPY",FACE,{"derivedFrom":subQ1,"instanceName":"16"}),makeQuery(id+"F6.opPattern","COPY",FACE,{"derivedFrom":subQ1,"instanceName":"17"}),makeQuery(id+"F6.opPattern","COPY",FACE,{"derivedFrom":subQ1,"instanceName":"18"}),makeQuery(id+"F6.opPattern","COPY",FACE,{"derivedFrom":subQ1,"instanceName":"19"}),makeQuery(id+"F6.opPattern","COPY",FACE,{"derivedFrom":subQ1,"instanceName":"20"}),makeQuery(id+"F6.opPattern","COPY",FACE,{"derivedFrom":subQ1,"instanceName":"21"}),makeQuery(id+"F6.opPattern","COPY",FACE,{"derivedFrom":subQ1,"instanceName":"22"}),makeQuery(id+"F6.opPattern","COPY",FACE,{"derivedFrom":subQ1,"instanceName":"23"}),makeQuery(id+"F6.opPattern","COPY",FACE,{"derivedFrom":subQ1,"instanceName":"24"}),makeQuery(id+"F6.opPattern","COPY",FACE,{"derivedFrom":subQ1,"instanceName":"25"}),makeQuery(id+"F6.opPattern","COPY",FACE,{"derivedFrom":subQ1,"instanceName":"26"}),makeQuery(id+"F6.opPattern","COPY",FACE,{"derivedFrom":subQ1,"instanceName":"27"}),makeQuery(id+"F6.opPattern","COPY",FACE,{"derivedFrom":subQ1,"instanceName":"28"}),makeQuery(id+"F6.opPattern","COPY",FACE,{"derivedFrom":subQ1,"instanceName":"29"}),makeQuery(id+"F6.opPattern","COPY",FACE,{"derivedFrom":subQ1,"instanceName":"30"}),makeQuery(id+"F6.opPattern","COPY",FACE,{"derivedFrom":subQ1,"instanceName":"31"}),makeQuery(id+"F6.opPattern","COPY",FACE,{"derivedFrom":subQ1,"instanceName":"32"}),makeQuery(id+"F6.opPattern","COPY",FACE,{"derivedFrom":subQ1,"instanceName":"33"}),makeQuery(id+"F6.opPattern","COPY",FACE,{"derivedFrom":subQ1,"instanceName":"34"}),makeQuery(id+"F6.opPattern","COPY",FACE,{"derivedFrom":subQ1,"instanceName":"35"}),makeQuery(id+"F6.opPattern","COPY",FACE,{"derivedFrom":subQ1,"instanceName":"36"}),makeQuery(id+"F6.opPattern","COPY",FACE,{"derivedFrom":subQ1,"instanceName":"37"}),makeQuery(id+"F6.opPattern","COPY",FACE,{"derivedFrom":subQ1,"instanceName":"38"}),makeQuery(id+"F6.opPattern","COPY",FACE,{"derivedFrom":subQ1,"instanceName":"39"}),makeQuery(id+"F6.opPattern","COPY",FACE,{"derivedFrom":subQ1,"instanceName":"40"}),makeQuery(id+"F6.opPattern","COPY",FACE,{"derivedFrom":subQ1,"instanceName":"41"}),makeQuery(id+"F6.opPattern","COPY",FACE,{"derivedFrom":subQ1,"instanceName":"42"}),makeQuery(id+"F6.opPattern","COPY",FACE,{"derivedFrom":subQ1,"instanceName":"43"}),makeQuery(id+"F6.opPattern","COPY",FACE,{"derivedFrom":subQ1,"instanceName":"44"}),makeQuery(id+"F6.opPattern","COPY",FACE,{"derivedFrom":subQ1,"instanceName":"45"}),makeQuery(id+"F6.opPattern","COPY",FACE,{"derivedFrom":subQ1,"instanceName":"46"}),makeQuery(id+"F6.opPattern","COPY",FACE,{"derivedFrom":subQ1,"instanceName":"47"}),makeQuery(id+"F6.opPattern","COPY",FACE,{"derivedFrom":subQ1,"instanceName":"48"}),makeQuery(id+"F6.opPattern","COPY",FACE,{"derivedFrom":subQ1,"instanceName":"49"}),makeQuery(id+"F6.opPattern","COPY",FACE,{"derivedFrom":subQ1,"instanceName":"50"}),makeQuery(id+"F6.opPattern","COPY",FACE,{"derivedFrom":subQ1,"instanceName":"51"}),makeQuery(id+"F6.opPattern","COPY",FACE,{"derivedFrom":subQ1,"instanceName":"52"}),makeQuery(id+"F6.opPattern","COPY",FACE,{"derivedFrom":subQ1,"instanceName":"53"}),makeQuery(id+"F6.opPattern","COPY",FACE,{"derivedFrom":subQ1,"instanceName":"54"}),makeQuery(id+"F6.opPattern","COPY",FACE,{"derivedFrom":subQ1,"instanceName":"55"}),makeQuery(id+"F6.opPattern","COPY",FACE,{"derivedFrom":subQ1,"instanceName":"56"}),makeQuery(id+"F6.opPattern","COPY",FACE,{"derivedFrom":subQ1,"instanceName":"57"}),makeQuery(id+"F6.opPattern","COPY",FACE,{"derivedFrom":subQ1,"instanceName":"58"}),makeQuery(id+"F6.opPattern","COPY",FACE,{"derivedFrom":subQ1,"instanceName":"59"}),makeQuery(id+"F6.opPattern","COPY",FACE,{"derivedFrom":subQ1,"instanceName":"60"}),makeQuery(id+"F6.opPattern","COPY",FACE,{"derivedFrom":subQ1,"instanceName":"61"}),makeQuery(id+"F6.opPattern","COPY",FACE,{"derivedFrom":subQ1,"instanceName":"62"}),makeQuery(id+"F6.opPattern","COPY",FACE,{"derivedFrom":subQ1,"instanceName":"63"}),makeQuery(id+"F6.opPattern","COPY",FACE,{"derivedFrom":subQ1,"instanceName":"64"}),makeQuery(id+"F6.opPattern","COPY",FACE,{"derivedFrom":subQ1,"instanceName":"65"}),makeQuery(id+"F6.opPattern","COPY",FACE,{"derivedFrom":subQ1,"instanceName":"66"}),makeQuery(id+"F6.opPattern","COPY",FACE,{"derivedFrom":subQ1,"instanceName":"67"}),makeQuery(id+"F6.opPattern","COPY",FACE,{"derivedFrom":subQ1,"instanceName":"68"}),makeQuery(id+"F6.opPattern","COPY",FACE,{"derivedFrom":subQ1,"instanceName":"69"}),makeQuery(id+"F6.opPattern","COPY",FACE,{"derivedFrom":subQ1,"instanceName":"70"}),makeQuery(id+"F6.opPattern","COPY",FACE,{"derivedFrom":subQ1,"instanceName":"71"}),makeQuery(id+"F6.opPattern","COPY",FACE,{"derivedFrom":subQ1,"instanceName":"72"}),makeQuery(id+"F6.opPattern","COPY",FACE,{"derivedFrom":subQ1,"instanceName":"73"}),makeQuery(id+"F6.opPattern","COPY",FACE,{"derivedFrom":subQ1,"instanceName":"74"}),makeQuery(id+"F6.opPattern","COPY",FACE,{"derivedFrom":subQ1,"instanceName":"75"}),makeQuery(id+"F6.opPattern","COPY",FACE,{"derivedFrom":subQ1,"instanceName":"76"}),makeQuery(id+"F6.opPattern","COPY",FACE,{"derivedFrom":subQ1,"instanceName":"77"}),makeQuery(id+"F6.opPattern","COPY",FACE,{"derivedFrom":subQ1,"instanceName":"78"})]}),makeQuery(id+"F8.opExtrude","SWEPT_FACE",FACE,{"disambiguationData":[OSD([sQuery(id+"F7.wireOp",EDGE,"E15.1.0")])]})]});}
            var Q9;
            {var subQ0=sQuery(id+"F2.wireOp",EDGE,"E0");var subQ1=makeQuery(id+"F5.boolean.opBoolean","MERGE",FACE,{"derivedFrom":[makeQuery(id+"F4.opExtrude","CAP_FACE",FACE,{"disambiguationData":[OSD([subQ0])],"isStart":true}),makeQuery(id+"F5.opExtrude","CAP_FACE",FACE,{"disambiguationData":[OSD([subQ0,sQuery(id+"F2.wireOp",EDGE,"E1"),sQuery(id+"F2.wireOp",EDGE,"E2"),sQuery(id+"F2.wireOp",EDGE,"E3")])],"isStart":true})]});Q9=makeQuery(id+"F8.boolean.opBoolean","INTERSECT",EDGE,{"derivedFrom":[makeQuery(id+"F6.boolean.opBoolean","MERGE",FACE,{"derivedFrom":[subQ1,makeQuery(id+"F6.opPattern","COPY",FACE,{"derivedFrom":subQ1,"instanceName":"1"}),makeQuery(id+"F6.opPattern","COPY",FACE,{"derivedFrom":subQ1,"instanceName":"2"}),makeQuery(id+"F6.opPattern","COPY",FACE,{"derivedFrom":subQ1,"instanceName":"3"}),makeQuery(id+"F6.opPattern","COPY",FACE,{"derivedFrom":subQ1,"instanceName":"4"}),makeQuery(id+"F6.opPattern","COPY",FACE,{"derivedFrom":subQ1,"instanceName":"5"}),makeQuery(id+"F6.opPattern","COPY",FACE,{"derivedFrom":subQ1,"instanceName":"6"}),makeQuery(id+"F6.opPattern","COPY",FACE,{"derivedFrom":subQ1,"instanceName":"7"}),makeQuery(id+"F6.opPattern","COPY",FACE,{"derivedFrom":subQ1,"instanceName":"8"}),makeQuery(id+"F6.opPattern","COPY",FACE,{"derivedFrom":subQ1,"instanceName":"9"}),makeQuery(id+"F6.opPattern","COPY",FACE,{"derivedFrom":subQ1,"instanceName":"10"}),makeQuery(id+"F6.opPattern","COPY",FACE,{"derivedFrom":subQ1,"instanceName":"11"}),makeQuery(id+"F6.opPattern","COPY",FACE,{"derivedFrom":subQ1,"instanceName":"12"}),makeQuery(id+"F6.opPattern","COPY",FACE,{"derivedFrom":subQ1,"instanceName":"13"}),makeQuery(id+"F6.opPattern","COPY",FACE,{"derivedFrom":subQ1,"instanceName":"14"}),makeQuery(id+"F6.opPattern","COPY",FACE,{"derivedFrom":subQ1,"instanceName":"15"}),makeQuery(id+"F6.opPattern","COPY",FACE,{"derivedFrom":subQ1,"instanceName":"16"}),makeQuery(id+"F6.opPattern","COPY",FACE,{"derivedFrom":subQ1,"instanceName":"17"}),makeQuery(id+"F6.opPattern","COPY",FACE,{"derivedFrom":subQ1,"instanceName":"18"}),makeQuery(id+"F6.opPattern","COPY",FACE,{"derivedFrom":subQ1,"instanceName":"19"}),makeQuery(id+"F6.opPattern","COPY",FACE,{"derivedFrom":subQ1,"instanceName":"20"}),makeQuery(id+"F6.opPattern","COPY",FACE,{"derivedFrom":subQ1,"instanceName":"21"}),makeQuery(id+"F6.opPattern","COPY",FACE,{"derivedFrom":subQ1,"instanceName":"22"}),makeQuery(id+"F6.opPattern","COPY",FACE,{"derivedFrom":subQ1,"instanceName":"23"}),makeQuery(id+"F6.opPattern","COPY",FACE,{"derivedFrom":subQ1,"instanceName":"24"}),makeQuery(id+"F6.opPattern","COPY",FACE,{"derivedFrom":subQ1,"instanceName":"25"}),makeQuery(id+"F6.opPattern","COPY",FACE,{"derivedFrom":subQ1,"instanceName":"26"}),makeQuery(id+"F6.opPattern","COPY",FACE,{"derivedFrom":subQ1,"instanceName":"27"}),makeQuery(id+"F6.opPattern","COPY",FACE,{"derivedFrom":subQ1,"instanceName":"28"}),makeQuery(id+"F6.opPattern","COPY",FACE,{"derivedFrom":subQ1,"instanceName":"29"}),makeQuery(id+"F6.opPattern","COPY",FACE,{"derivedFrom":subQ1,"instanceName":"30"}),makeQuery(id+"F6.opPattern","COPY",FACE,{"derivedFrom":subQ1,"instanceName":"31"}),makeQuery(id+"F6.opPattern","COPY",FACE,{"derivedFrom":subQ1,"instanceName":"32"}),makeQuery(id+"F6.opPattern","COPY",FACE,{"derivedFrom":subQ1,"instanceName":"33"}),makeQuery(id+"F6.opPattern","COPY",FACE,{"derivedFrom":subQ1,"instanceName":"34"}),makeQuery(id+"F6.opPattern","COPY",FACE,{"derivedFrom":subQ1,"instanceName":"35"}),makeQuery(id+"F6.opPattern","COPY",FACE,{"derivedFrom":subQ1,"instanceName":"36"}),makeQuery(id+"F6.opPattern","COPY",FACE,{"derivedFrom":subQ1,"instanceName":"37"}),makeQuery(id+"F6.opPattern","COPY",FACE,{"derivedFrom":subQ1,"instanceName":"38"}),makeQuery(id+"F6.opPattern","COPY",FACE,{"derivedFrom":subQ1,"instanceName":"39"}),makeQuery(id+"F6.opPattern","COPY",FACE,{"derivedFrom":subQ1,"instanceName":"40"}),makeQuery(id+"F6.opPattern","COPY",FACE,{"derivedFrom":subQ1,"instanceName":"41"}),makeQuery(id+"F6.opPattern","COPY",FACE,{"derivedFrom":subQ1,"instanceName":"42"}),makeQuery(id+"F6.opPattern","COPY",FACE,{"derivedFrom":subQ1,"instanceName":"43"}),makeQuery(id+"F6.opPattern","COPY",FACE,{"derivedFrom":subQ1,"instanceName":"44"}),makeQuery(id+"F6.opPattern","COPY",FACE,{"derivedFrom":subQ1,"instanceName":"45"}),makeQuery(id+"F6.opPattern","COPY",FACE,{"derivedFrom":subQ1,"instanceName":"46"}),makeQuery(id+"F6.opPattern","COPY",FACE,{"derivedFrom":subQ1,"instanceName":"47"}),makeQuery(id+"F6.opPattern","COPY",FACE,{"derivedFrom":subQ1,"instanceName":"48"}),makeQuery(id+"F6.opPattern","COPY",FACE,{"derivedFrom":subQ1,"instanceName":"49"}),makeQuery(id+"F6.opPattern","COPY",FACE,{"derivedFrom":subQ1,"instanceName":"50"}),makeQuery(id+"F6.opPattern","COPY",FACE,{"derivedFrom":subQ1,"instanceName":"51"}),makeQuery(id+"F6.opPattern","COPY",FACE,{"derivedFrom":subQ1,"instanceName":"52"}),makeQuery(id+"F6.opPattern","COPY",FACE,{"derivedFrom":subQ1,"instanceName":"53"}),makeQuery(id+"F6.opPattern","COPY",FACE,{"derivedFrom":subQ1,"instanceName":"54"}),makeQuery(id+"F6.opPattern","COPY",FACE,{"derivedFrom":subQ1,"instanceName":"55"}),makeQuery(id+"F6.opPattern","COPY",FACE,{"derivedFrom":subQ1,"instanceName":"56"}),makeQuery(id+"F6.opPattern","COPY",FACE,{"derivedFrom":subQ1,"instanceName":"57"}),makeQuery(id+"F6.opPattern","COPY",FACE,{"derivedFrom":subQ1,"instanceName":"58"}),makeQuery(id+"F6.opPattern","COPY",FACE,{"derivedFrom":subQ1,"instanceName":"59"}),makeQuery(id+"F6.opPattern","COPY",FACE,{"derivedFrom":subQ1,"instanceName":"60"}),makeQuery(id+"F6.opPattern","COPY",FACE,{"derivedFrom":subQ1,"instanceName":"61"}),makeQuery(id+"F6.opPattern","COPY",FACE,{"derivedFrom":subQ1,"instanceName":"62"}),makeQuery(id+"F6.opPattern","COPY",FACE,{"derivedFrom":subQ1,"instanceName":"63"}),makeQuery(id+"F6.opPattern","COPY",FACE,{"derivedFrom":subQ1,"instanceName":"64"}),makeQuery(id+"F6.opPattern","COPY",FACE,{"derivedFrom":subQ1,"instanceName":"65"}),makeQuery(id+"F6.opPattern","COPY",FACE,{"derivedFrom":subQ1,"instanceName":"66"}),makeQuery(id+"F6.opPattern","COPY",FACE,{"derivedFrom":subQ1,"instanceName":"67"}),makeQuery(id+"F6.opPattern","COPY",FACE,{"derivedFrom":subQ1,"instanceName":"68"}),makeQuery(id+"F6.opPattern","COPY",FACE,{"derivedFrom":subQ1,"instanceName":"69"}),makeQuery(id+"F6.opPattern","COPY",FACE,{"derivedFrom":subQ1,"instanceName":"70"}),makeQuery(id+"F6.opPattern","COPY",FACE,{"derivedFrom":subQ1,"instanceName":"71"}),makeQuery(id+"F6.opPattern","COPY",FACE,{"derivedFrom":subQ1,"instanceName":"72"}),makeQuery(id+"F6.opPattern","COPY",FACE,{"derivedFrom":subQ1,"instanceName":"73"}),makeQuery(id+"F6.opPattern","COPY",FACE,{"derivedFrom":subQ1,"instanceName":"74"}),makeQuery(id+"F6.opPattern","COPY",FACE,{"derivedFrom":subQ1,"instanceName":"75"}),makeQuery(id+"F6.opPattern","COPY",FACE,{"derivedFrom":subQ1,"instanceName":"76"}),makeQuery(id+"F6.opPattern","COPY",FACE,{"derivedFrom":subQ1,"instanceName":"77"}),makeQuery(id+"F6.opPattern","COPY",FACE,{"derivedFrom":subQ1,"instanceName":"78"})]}),makeQuery(id+"F8.opExtrude","SWEPT_FACE",FACE,{"disambiguationData":[OSD([sQuery(id+"F7.wireOp",EDGE,"E14")])]})]});}
            var Q10;
            {var subQ0=sQuery(id+"F2.wireOp",EDGE,"E0");var subQ1=makeQuery(id+"F5.boolean.opBoolean","MERGE",FACE,{"derivedFrom":[makeQuery(id+"F4.opExtrude","CAP_FACE",FACE,{"disambiguationData":[OSD([subQ0])],"isStart":true}),makeQuery(id+"F5.opExtrude","CAP_FACE",FACE,{"disambiguationData":[OSD([subQ0,sQuery(id+"F2.wireOp",EDGE,"E1"),sQuery(id+"F2.wireOp",EDGE,"E2"),sQuery(id+"F2.wireOp",EDGE,"E3")])],"isStart":true})]});Q10=makeQuery(id+"F8.boolean.opBoolean","INTERSECT",EDGE,{"derivedFrom":[makeQuery(id+"F6.boolean.opBoolean","MERGE",FACE,{"derivedFrom":[subQ1,makeQuery(id+"F6.opPattern","COPY",FACE,{"derivedFrom":subQ1,"instanceName":"1"}),makeQuery(id+"F6.opPattern","COPY",FACE,{"derivedFrom":subQ1,"instanceName":"2"}),makeQuery(id+"F6.opPattern","COPY",FACE,{"derivedFrom":subQ1,"instanceName":"3"}),makeQuery(id+"F6.opPattern","COPY",FACE,{"derivedFrom":subQ1,"instanceName":"4"}),makeQuery(id+"F6.opPattern","COPY",FACE,{"derivedFrom":subQ1,"instanceName":"5"}),makeQuery(id+"F6.opPattern","COPY",FACE,{"derivedFrom":subQ1,"instanceName":"6"}),makeQuery(id+"F6.opPattern","COPY",FACE,{"derivedFrom":subQ1,"instanceName":"7"}),makeQuery(id+"F6.opPattern","COPY",FACE,{"derivedFrom":subQ1,"instanceName":"8"}),makeQuery(id+"F6.opPattern","COPY",FACE,{"derivedFrom":subQ1,"instanceName":"9"}),makeQuery(id+"F6.opPattern","COPY",FACE,{"derivedFrom":subQ1,"instanceName":"10"}),makeQuery(id+"F6.opPattern","COPY",FACE,{"derivedFrom":subQ1,"instanceName":"11"}),makeQuery(id+"F6.opPattern","COPY",FACE,{"derivedFrom":subQ1,"instanceName":"12"}),makeQuery(id+"F6.opPattern","COPY",FACE,{"derivedFrom":subQ1,"instanceName":"13"}),makeQuery(id+"F6.opPattern","COPY",FACE,{"derivedFrom":subQ1,"instanceName":"14"}),makeQuery(id+"F6.opPattern","COPY",FACE,{"derivedFrom":subQ1,"instanceName":"15"}),makeQuery(id+"F6.opPattern","COPY",FACE,{"derivedFrom":subQ1,"instanceName":"16"}),makeQuery(id+"F6.opPattern","COPY",FACE,{"derivedFrom":subQ1,"instanceName":"17"}),makeQuery(id+"F6.opPattern","COPY",FACE,{"derivedFrom":subQ1,"instanceName":"18"}),makeQuery(id+"F6.opPattern","COPY",FACE,{"derivedFrom":subQ1,"instanceName":"19"}),makeQuery(id+"F6.opPattern","COPY",FACE,{"derivedFrom":subQ1,"instanceName":"20"}),makeQuery(id+"F6.opPattern","COPY",FACE,{"derivedFrom":subQ1,"instanceName":"21"}),makeQuery(id+"F6.opPattern","COPY",FACE,{"derivedFrom":subQ1,"instanceName":"22"}),makeQuery(id+"F6.opPattern","COPY",FACE,{"derivedFrom":subQ1,"instanceName":"23"}),makeQuery(id+"F6.opPattern","COPY",FACE,{"derivedFrom":subQ1,"instanceName":"24"}),makeQuery(id+"F6.opPattern","COPY",FACE,{"derivedFrom":subQ1,"instanceName":"25"}),makeQuery(id+"F6.opPattern","COPY",FACE,{"derivedFrom":subQ1,"instanceName":"26"}),makeQuery(id+"F6.opPattern","COPY",FACE,{"derivedFrom":subQ1,"instanceName":"27"}),makeQuery(id+"F6.opPattern","COPY",FACE,{"derivedFrom":subQ1,"instanceName":"28"}),makeQuery(id+"F6.opPattern","COPY",FACE,{"derivedFrom":subQ1,"instanceName":"29"}),makeQuery(id+"F6.opPattern","COPY",FACE,{"derivedFrom":subQ1,"instanceName":"30"}),makeQuery(id+"F6.opPattern","COPY",FACE,{"derivedFrom":subQ1,"instanceName":"31"}),makeQuery(id+"F6.opPattern","COPY",FACE,{"derivedFrom":subQ1,"instanceName":"32"}),makeQuery(id+"F6.opPattern","COPY",FACE,{"derivedFrom":subQ1,"instanceName":"33"}),makeQuery(id+"F6.opPattern","COPY",FACE,{"derivedFrom":subQ1,"instanceName":"34"}),makeQuery(id+"F6.opPattern","COPY",FACE,{"derivedFrom":subQ1,"instanceName":"35"}),makeQuery(id+"F6.opPattern","COPY",FACE,{"derivedFrom":subQ1,"instanceName":"36"}),makeQuery(id+"F6.opPattern","COPY",FACE,{"derivedFrom":subQ1,"instanceName":"37"}),makeQuery(id+"F6.opPattern","COPY",FACE,{"derivedFrom":subQ1,"instanceName":"38"}),makeQuery(id+"F6.opPattern","COPY",FACE,{"derivedFrom":subQ1,"instanceName":"39"}),makeQuery(id+"F6.opPattern","COPY",FACE,{"derivedFrom":subQ1,"instanceName":"40"}),makeQuery(id+"F6.opPattern","COPY",FACE,{"derivedFrom":subQ1,"instanceName":"41"}),makeQuery(id+"F6.opPattern","COPY",FACE,{"derivedFrom":subQ1,"instanceName":"42"}),makeQuery(id+"F6.opPattern","COPY",FACE,{"derivedFrom":subQ1,"instanceName":"43"}),makeQuery(id+"F6.opPattern","COPY",FACE,{"derivedFrom":subQ1,"instanceName":"44"}),makeQuery(id+"F6.opPattern","COPY",FACE,{"derivedFrom":subQ1,"instanceName":"45"}),makeQuery(id+"F6.opPattern","COPY",FACE,{"derivedFrom":subQ1,"instanceName":"46"}),makeQuery(id+"F6.opPattern","COPY",FACE,{"derivedFrom":subQ1,"instanceName":"47"}),makeQuery(id+"F6.opPattern","COPY",FACE,{"derivedFrom":subQ1,"instanceName":"48"}),makeQuery(id+"F6.opPattern","COPY",FACE,{"derivedFrom":subQ1,"instanceName":"49"}),makeQuery(id+"F6.opPattern","COPY",FACE,{"derivedFrom":subQ1,"instanceName":"50"}),makeQuery(id+"F6.opPattern","COPY",FACE,{"derivedFrom":subQ1,"instanceName":"51"}),makeQuery(id+"F6.opPattern","COPY",FACE,{"derivedFrom":subQ1,"instanceName":"52"}),makeQuery(id+"F6.opPattern","COPY",FACE,{"derivedFrom":subQ1,"instanceName":"53"}),makeQuery(id+"F6.opPattern","COPY",FACE,{"derivedFrom":subQ1,"instanceName":"54"}),makeQuery(id+"F6.opPattern","COPY",FACE,{"derivedFrom":subQ1,"instanceName":"55"}),makeQuery(id+"F6.opPattern","COPY",FACE,{"derivedFrom":subQ1,"instanceName":"56"}),makeQuery(id+"F6.opPattern","COPY",FACE,{"derivedFrom":subQ1,"instanceName":"57"}),makeQuery(id+"F6.opPattern","COPY",FACE,{"derivedFrom":subQ1,"instanceName":"58"}),makeQuery(id+"F6.opPattern","COPY",FACE,{"derivedFrom":subQ1,"instanceName":"59"}),makeQuery(id+"F6.opPattern","COPY",FACE,{"derivedFrom":subQ1,"instanceName":"60"}),makeQuery(id+"F6.opPattern","COPY",FACE,{"derivedFrom":subQ1,"instanceName":"61"}),makeQuery(id+"F6.opPattern","COPY",FACE,{"derivedFrom":subQ1,"instanceName":"62"}),makeQuery(id+"F6.opPattern","COPY",FACE,{"derivedFrom":subQ1,"instanceName":"63"}),makeQuery(id+"F6.opPattern","COPY",FACE,{"derivedFrom":subQ1,"instanceName":"64"}),makeQuery(id+"F6.opPattern","COPY",FACE,{"derivedFrom":subQ1,"instanceName":"65"}),makeQuery(id+"F6.opPattern","COPY",FACE,{"derivedFrom":subQ1,"instanceName":"66"}),makeQuery(id+"F6.opPattern","COPY",FACE,{"derivedFrom":subQ1,"instanceName":"67"}),makeQuery(id+"F6.opPattern","COPY",FACE,{"derivedFrom":subQ1,"instanceName":"68"}),makeQuery(id+"F6.opPattern","COPY",FACE,{"derivedFrom":subQ1,"instanceName":"69"}),makeQuery(id+"F6.opPattern","COPY",FACE,{"derivedFrom":subQ1,"instanceName":"70"}),makeQuery(id+"F6.opPattern","COPY",FACE,{"derivedFrom":subQ1,"instanceName":"71"}),makeQuery(id+"F6.opPattern","COPY",FACE,{"derivedFrom":subQ1,"instanceName":"72"}),makeQuery(id+"F6.opPattern","COPY",FACE,{"derivedFrom":subQ1,"instanceName":"73"}),makeQuery(id+"F6.opPattern","COPY",FACE,{"derivedFrom":subQ1,"instanceName":"74"}),makeQuery(id+"F6.opPattern","COPY",FACE,{"derivedFrom":subQ1,"instanceName":"75"}),makeQuery(id+"F6.opPattern","COPY",FACE,{"derivedFrom":subQ1,"instanceName":"76"}),makeQuery(id+"F6.opPattern","COPY",FACE,{"derivedFrom":subQ1,"instanceName":"77"}),makeQuery(id+"F6.opPattern","COPY",FACE,{"derivedFrom":subQ1,"instanceName":"78"})]}),makeQuery(id+"F8.opExtrude","SWEPT_FACE",FACE,{"disambiguationData":[OSD([sQuery(id+"F7.wireOp",EDGE,"E16.1.5.0")])]})]});}
            var Q11;
            {var subQ0=sQuery(id+"F2.wireOp",EDGE,"E0");var subQ1=makeQuery(id+"F5.boolean.opBoolean","MERGE",FACE,{"derivedFrom":[makeQuery(id+"F4.opExtrude","CAP_FACE",FACE,{"disambiguationData":[OSD([subQ0])],"isStart":true}),makeQuery(id+"F5.opExtrude","CAP_FACE",FACE,{"disambiguationData":[OSD([subQ0,sQuery(id+"F2.wireOp",EDGE,"E1"),sQuery(id+"F2.wireOp",EDGE,"E2"),sQuery(id+"F2.wireOp",EDGE,"E3")])],"isStart":true})]});Q11=makeQuery(id+"F8.boolean.opBoolean","INTERSECT",EDGE,{"derivedFrom":[makeQuery(id+"F6.boolean.opBoolean","MERGE",FACE,{"derivedFrom":[subQ1,makeQuery(id+"F6.opPattern","COPY",FACE,{"derivedFrom":subQ1,"instanceName":"1"}),makeQuery(id+"F6.opPattern","COPY",FACE,{"derivedFrom":subQ1,"instanceName":"2"}),makeQuery(id+"F6.opPattern","COPY",FACE,{"derivedFrom":subQ1,"instanceName":"3"}),makeQuery(id+"F6.opPattern","COPY",FACE,{"derivedFrom":subQ1,"instanceName":"4"}),makeQuery(id+"F6.opPattern","COPY",FACE,{"derivedFrom":subQ1,"instanceName":"5"}),makeQuery(id+"F6.opPattern","COPY",FACE,{"derivedFrom":subQ1,"instanceName":"6"}),makeQuery(id+"F6.opPattern","COPY",FACE,{"derivedFrom":subQ1,"instanceName":"7"}),makeQuery(id+"F6.opPattern","COPY",FACE,{"derivedFrom":subQ1,"instanceName":"8"}),makeQuery(id+"F6.opPattern","COPY",FACE,{"derivedFrom":subQ1,"instanceName":"9"}),makeQuery(id+"F6.opPattern","COPY",FACE,{"derivedFrom":subQ1,"instanceName":"10"}),makeQuery(id+"F6.opPattern","COPY",FACE,{"derivedFrom":subQ1,"instanceName":"11"}),makeQuery(id+"F6.opPattern","COPY",FACE,{"derivedFrom":subQ1,"instanceName":"12"}),makeQuery(id+"F6.opPattern","COPY",FACE,{"derivedFrom":subQ1,"instanceName":"13"}),makeQuery(id+"F6.opPattern","COPY",FACE,{"derivedFrom":subQ1,"instanceName":"14"}),makeQuery(id+"F6.opPattern","COPY",FACE,{"derivedFrom":subQ1,"instanceName":"15"}),makeQuery(id+"F6.opPattern","COPY",FACE,{"derivedFrom":subQ1,"instanceName":"16"}),makeQuery(id+"F6.opPattern","COPY",FACE,{"derivedFrom":subQ1,"instanceName":"17"}),makeQuery(id+"F6.opPattern","COPY",FACE,{"derivedFrom":subQ1,"instanceName":"18"}),makeQuery(id+"F6.opPattern","COPY",FACE,{"derivedFrom":subQ1,"instanceName":"19"}),makeQuery(id+"F6.opPattern","COPY",FACE,{"derivedFrom":subQ1,"instanceName":"20"}),makeQuery(id+"F6.opPattern","COPY",FACE,{"derivedFrom":subQ1,"instanceName":"21"}),makeQuery(id+"F6.opPattern","COPY",FACE,{"derivedFrom":subQ1,"instanceName":"22"}),makeQuery(id+"F6.opPattern","COPY",FACE,{"derivedFrom":subQ1,"instanceName":"23"}),makeQuery(id+"F6.opPattern","COPY",FACE,{"derivedFrom":subQ1,"instanceName":"24"}),makeQuery(id+"F6.opPattern","COPY",FACE,{"derivedFrom":subQ1,"instanceName":"25"}),makeQuery(id+"F6.opPattern","COPY",FACE,{"derivedFrom":subQ1,"instanceName":"26"}),makeQuery(id+"F6.opPattern","COPY",FACE,{"derivedFrom":subQ1,"instanceName":"27"}),makeQuery(id+"F6.opPattern","COPY",FACE,{"derivedFrom":subQ1,"instanceName":"28"}),makeQuery(id+"F6.opPattern","COPY",FACE,{"derivedFrom":subQ1,"instanceName":"29"}),makeQuery(id+"F6.opPattern","COPY",FACE,{"derivedFrom":subQ1,"instanceName":"30"}),makeQuery(id+"F6.opPattern","COPY",FACE,{"derivedFrom":subQ1,"instanceName":"31"}),makeQuery(id+"F6.opPattern","COPY",FACE,{"derivedFrom":subQ1,"instanceName":"32"}),makeQuery(id+"F6.opPattern","COPY",FACE,{"derivedFrom":subQ1,"instanceName":"33"}),makeQuery(id+"F6.opPattern","COPY",FACE,{"derivedFrom":subQ1,"instanceName":"34"}),makeQuery(id+"F6.opPattern","COPY",FACE,{"derivedFrom":subQ1,"instanceName":"35"}),makeQuery(id+"F6.opPattern","COPY",FACE,{"derivedFrom":subQ1,"instanceName":"36"}),makeQuery(id+"F6.opPattern","COPY",FACE,{"derivedFrom":subQ1,"instanceName":"37"}),makeQuery(id+"F6.opPattern","COPY",FACE,{"derivedFrom":subQ1,"instanceName":"38"}),makeQuery(id+"F6.opPattern","COPY",FACE,{"derivedFrom":subQ1,"instanceName":"39"}),makeQuery(id+"F6.opPattern","COPY",FACE,{"derivedFrom":subQ1,"instanceName":"40"}),makeQuery(id+"F6.opPattern","COPY",FACE,{"derivedFrom":subQ1,"instanceName":"41"}),makeQuery(id+"F6.opPattern","COPY",FACE,{"derivedFrom":subQ1,"instanceName":"42"}),makeQuery(id+"F6.opPattern","COPY",FACE,{"derivedFrom":subQ1,"instanceName":"43"}),makeQuery(id+"F6.opPattern","COPY",FACE,{"derivedFrom":subQ1,"instanceName":"44"}),makeQuery(id+"F6.opPattern","COPY",FACE,{"derivedFrom":subQ1,"instanceName":"45"}),makeQuery(id+"F6.opPattern","COPY",FACE,{"derivedFrom":subQ1,"instanceName":"46"}),makeQuery(id+"F6.opPattern","COPY",FACE,{"derivedFrom":subQ1,"instanceName":"47"}),makeQuery(id+"F6.opPattern","COPY",FACE,{"derivedFrom":subQ1,"instanceName":"48"}),makeQuery(id+"F6.opPattern","COPY",FACE,{"derivedFrom":subQ1,"instanceName":"49"}),makeQuery(id+"F6.opPattern","COPY",FACE,{"derivedFrom":subQ1,"instanceName":"50"}),makeQuery(id+"F6.opPattern","COPY",FACE,{"derivedFrom":subQ1,"instanceName":"51"}),makeQuery(id+"F6.opPattern","COPY",FACE,{"derivedFrom":subQ1,"instanceName":"52"}),makeQuery(id+"F6.opPattern","COPY",FACE,{"derivedFrom":subQ1,"instanceName":"53"}),makeQuery(id+"F6.opPattern","COPY",FACE,{"derivedFrom":subQ1,"instanceName":"54"}),makeQuery(id+"F6.opPattern","COPY",FACE,{"derivedFrom":subQ1,"instanceName":"55"}),makeQuery(id+"F6.opPattern","COPY",FACE,{"derivedFrom":subQ1,"instanceName":"56"}),makeQuery(id+"F6.opPattern","COPY",FACE,{"derivedFrom":subQ1,"instanceName":"57"}),makeQuery(id+"F6.opPattern","COPY",FACE,{"derivedFrom":subQ1,"instanceName":"58"}),makeQuery(id+"F6.opPattern","COPY",FACE,{"derivedFrom":subQ1,"instanceName":"59"}),makeQuery(id+"F6.opPattern","COPY",FACE,{"derivedFrom":subQ1,"instanceName":"60"}),makeQuery(id+"F6.opPattern","COPY",FACE,{"derivedFrom":subQ1,"instanceName":"61"}),makeQuery(id+"F6.opPattern","COPY",FACE,{"derivedFrom":subQ1,"instanceName":"62"}),makeQuery(id+"F6.opPattern","COPY",FACE,{"derivedFrom":subQ1,"instanceName":"63"}),makeQuery(id+"F6.opPattern","COPY",FACE,{"derivedFrom":subQ1,"instanceName":"64"}),makeQuery(id+"F6.opPattern","COPY",FACE,{"derivedFrom":subQ1,"instanceName":"65"}),makeQuery(id+"F6.opPattern","COPY",FACE,{"derivedFrom":subQ1,"instanceName":"66"}),makeQuery(id+"F6.opPattern","COPY",FACE,{"derivedFrom":subQ1,"instanceName":"67"}),makeQuery(id+"F6.opPattern","COPY",FACE,{"derivedFrom":subQ1,"instanceName":"68"}),makeQuery(id+"F6.opPattern","COPY",FACE,{"derivedFrom":subQ1,"instanceName":"69"}),makeQuery(id+"F6.opPattern","COPY",FACE,{"derivedFrom":subQ1,"instanceName":"70"}),makeQuery(id+"F6.opPattern","COPY",FACE,{"derivedFrom":subQ1,"instanceName":"71"}),makeQuery(id+"F6.opPattern","COPY",FACE,{"derivedFrom":subQ1,"instanceName":"72"}),makeQuery(id+"F6.opPattern","COPY",FACE,{"derivedFrom":subQ1,"instanceName":"73"}),makeQuery(id+"F6.opPattern","COPY",FACE,{"derivedFrom":subQ1,"instanceName":"74"}),makeQuery(id+"F6.opPattern","COPY",FACE,{"derivedFrom":subQ1,"instanceName":"75"}),makeQuery(id+"F6.opPattern","COPY",FACE,{"derivedFrom":subQ1,"instanceName":"76"}),makeQuery(id+"F6.opPattern","COPY",FACE,{"derivedFrom":subQ1,"instanceName":"77"}),makeQuery(id+"F6.opPattern","COPY",FACE,{"derivedFrom":subQ1,"instanceName":"78"})]}),makeQuery(id+"F8.opExtrude","SWEPT_FACE",FACE,{"disambiguationData":[OSD([sQuery(id+"F7.wireOp",EDGE,"E16.1.4.0")])]})]});}
            chamfer(context, id + "F9", {"entities" : qUnion([Q0, Q1, Q2, Q3, Q4, Q5, Q6, Q7, Q8, Q9, Q10, Q11]), "width" : 1.5 * mm, "tangentPropagation" : true});
        }
        {
            var Q0;
            {var subQ0=sQuery(id+"F2.wireOp",EDGE,"E0");var subQ1=makeQuery(id+"F5.boolean.opBoolean","MERGE",FACE,{"derivedFrom":[makeQuery(id+"F4.opExtrude","CAP_FACE",FACE,{"disambiguationData":[OSD([subQ0])],"isStart":false}),makeQuery(id+"F5.opExtrude","CAP_FACE",FACE,{"disambiguationData":[OSD([subQ0,sQuery(id+"F2.wireOp",EDGE,"E1"),sQuery(id+"F2.wireOp",EDGE,"E2"),sQuery(id+"F2.wireOp",EDGE,"E3")])],"isStart":false})]});Q0=makeQuery(id+"F9.opChamfer","BLEND_EDGE",EDGE,{"blendedFrom":[makeQuery(id+"F8.boolean.opBoolean","COPY",EDGE,{"derivedFrom":makeQuery(id+"F8.opExtrude","CAP_EDGE",EDGE,{"disambiguationData":[OSD([sQuery(id+"F7.wireOp",EDGE,"E15.1.0")])],"isStart":true})}),makeQuery(id+"F6.boolean.opBoolean","MERGE",FACE,{"derivedFrom":[subQ1,makeQuery(id+"F6.opPattern","COPY",FACE,{"derivedFrom":subQ1,"instanceName":"1"}),makeQuery(id+"F6.opPattern","COPY",FACE,{"derivedFrom":subQ1,"instanceName":"2"}),makeQuery(id+"F6.opPattern","COPY",FACE,{"derivedFrom":subQ1,"instanceName":"3"}),makeQuery(id+"F6.opPattern","COPY",FACE,{"derivedFrom":subQ1,"instanceName":"4"}),makeQuery(id+"F6.opPattern","COPY",FACE,{"derivedFrom":subQ1,"instanceName":"5"}),makeQuery(id+"F6.opPattern","COPY",FACE,{"derivedFrom":subQ1,"instanceName":"6"}),makeQuery(id+"F6.opPattern","COPY",FACE,{"derivedFrom":subQ1,"instanceName":"7"}),makeQuery(id+"F6.opPattern","COPY",FACE,{"derivedFrom":subQ1,"instanceName":"8"}),makeQuery(id+"F6.opPattern","COPY",FACE,{"derivedFrom":subQ1,"instanceName":"9"}),makeQuery(id+"F6.opPattern","COPY",FACE,{"derivedFrom":subQ1,"instanceName":"10"}),makeQuery(id+"F6.opPattern","COPY",FACE,{"derivedFrom":subQ1,"instanceName":"11"}),makeQuery(id+"F6.opPattern","COPY",FACE,{"derivedFrom":subQ1,"instanceName":"12"}),makeQuery(id+"F6.opPattern","COPY",FACE,{"derivedFrom":subQ1,"instanceName":"13"}),makeQuery(id+"F6.opPattern","COPY",FACE,{"derivedFrom":subQ1,"instanceName":"14"}),makeQuery(id+"F6.opPattern","COPY",FACE,{"derivedFrom":subQ1,"instanceName":"15"}),makeQuery(id+"F6.opPattern","COPY",FACE,{"derivedFrom":subQ1,"instanceName":"16"}),makeQuery(id+"F6.opPattern","COPY",FACE,{"derivedFrom":subQ1,"instanceName":"17"}),makeQuery(id+"F6.opPattern","COPY",FACE,{"derivedFrom":subQ1,"instanceName":"18"}),makeQuery(id+"F6.opPattern","COPY",FACE,{"derivedFrom":subQ1,"instanceName":"19"}),makeQuery(id+"F6.opPattern","COPY",FACE,{"derivedFrom":subQ1,"instanceName":"20"}),makeQuery(id+"F6.opPattern","COPY",FACE,{"derivedFrom":subQ1,"instanceName":"21"}),makeQuery(id+"F6.opPattern","COPY",FACE,{"derivedFrom":subQ1,"instanceName":"22"}),makeQuery(id+"F6.opPattern","COPY",FACE,{"derivedFrom":subQ1,"instanceName":"23"}),makeQuery(id+"F6.opPattern","COPY",FACE,{"derivedFrom":subQ1,"instanceName":"24"}),makeQuery(id+"F6.opPattern","COPY",FACE,{"derivedFrom":subQ1,"instanceName":"25"}),makeQuery(id+"F6.opPattern","COPY",FACE,{"derivedFrom":subQ1,"instanceName":"26"}),makeQuery(id+"F6.opPattern","COPY",FACE,{"derivedFrom":subQ1,"instanceName":"27"}),makeQuery(id+"F6.opPattern","COPY",FACE,{"derivedFrom":subQ1,"instanceName":"28"}),makeQuery(id+"F6.opPattern","COPY",FACE,{"derivedFrom":subQ1,"instanceName":"29"}),makeQuery(id+"F6.opPattern","COPY",FACE,{"derivedFrom":subQ1,"instanceName":"30"}),makeQuery(id+"F6.opPattern","COPY",FACE,{"derivedFrom":subQ1,"instanceName":"31"}),makeQuery(id+"F6.opPattern","COPY",FACE,{"derivedFrom":subQ1,"instanceName":"32"}),makeQuery(id+"F6.opPattern","COPY",FACE,{"derivedFrom":subQ1,"instanceName":"33"}),makeQuery(id+"F6.opPattern","COPY",FACE,{"derivedFrom":subQ1,"instanceName":"34"}),makeQuery(id+"F6.opPattern","COPY",FACE,{"derivedFrom":subQ1,"instanceName":"35"}),makeQuery(id+"F6.opPattern","COPY",FACE,{"derivedFrom":subQ1,"instanceName":"36"}),makeQuery(id+"F6.opPattern","COPY",FACE,{"derivedFrom":subQ1,"instanceName":"37"}),makeQuery(id+"F6.opPattern","COPY",FACE,{"derivedFrom":subQ1,"instanceName":"38"}),makeQuery(id+"F6.opPattern","COPY",FACE,{"derivedFrom":subQ1,"instanceName":"39"}),makeQuery(id+"F6.opPattern","COPY",FACE,{"derivedFrom":subQ1,"instanceName":"40"}),makeQuery(id+"F6.opPattern","COPY",FACE,{"derivedFrom":subQ1,"instanceName":"41"}),makeQuery(id+"F6.opPattern","COPY",FACE,{"derivedFrom":subQ1,"instanceName":"42"}),makeQuery(id+"F6.opPattern","COPY",FACE,{"derivedFrom":subQ1,"instanceName":"43"}),makeQuery(id+"F6.opPattern","COPY",FACE,{"derivedFrom":subQ1,"instanceName":"44"}),makeQuery(id+"F6.opPattern","COPY",FACE,{"derivedFrom":subQ1,"instanceName":"45"}),makeQuery(id+"F6.opPattern","COPY",FACE,{"derivedFrom":subQ1,"instanceName":"46"}),makeQuery(id+"F6.opPattern","COPY",FACE,{"derivedFrom":subQ1,"instanceName":"47"}),makeQuery(id+"F6.opPattern","COPY",FACE,{"derivedFrom":subQ1,"instanceName":"48"}),makeQuery(id+"F6.opPattern","COPY",FACE,{"derivedFrom":subQ1,"instanceName":"49"}),makeQuery(id+"F6.opPattern","COPY",FACE,{"derivedFrom":subQ1,"instanceName":"50"}),makeQuery(id+"F6.opPattern","COPY",FACE,{"derivedFrom":subQ1,"instanceName":"51"}),makeQuery(id+"F6.opPattern","COPY",FACE,{"derivedFrom":subQ1,"instanceName":"52"}),makeQuery(id+"F6.opPattern","COPY",FACE,{"derivedFrom":subQ1,"instanceName":"53"}),makeQuery(id+"F6.opPattern","COPY",FACE,{"derivedFrom":subQ1,"instanceName":"54"}),makeQuery(id+"F6.opPattern","COPY",FACE,{"derivedFrom":subQ1,"instanceName":"55"}),makeQuery(id+"F6.opPattern","COPY",FACE,{"derivedFrom":subQ1,"instanceName":"56"}),makeQuery(id+"F6.opPattern","COPY",FACE,{"derivedFrom":subQ1,"instanceName":"57"}),makeQuery(id+"F6.opPattern","COPY",FACE,{"derivedFrom":subQ1,"instanceName":"58"}),makeQuery(id+"F6.opPattern","COPY",FACE,{"derivedFrom":subQ1,"instanceName":"59"}),makeQuery(id+"F6.opPattern","COPY",FACE,{"derivedFrom":subQ1,"instanceName":"60"}),makeQuery(id+"F6.opPattern","COPY",FACE,{"derivedFrom":subQ1,"instanceName":"61"}),makeQuery(id+"F6.opPattern","COPY",FACE,{"derivedFrom":subQ1,"instanceName":"62"}),makeQuery(id+"F6.opPattern","COPY",FACE,{"derivedFrom":subQ1,"instanceName":"63"}),makeQuery(id+"F6.opPattern","COPY",FACE,{"derivedFrom":subQ1,"instanceName":"64"}),makeQuery(id+"F6.opPattern","COPY",FACE,{"derivedFrom":subQ1,"instanceName":"65"}),makeQuery(id+"F6.opPattern","COPY",FACE,{"derivedFrom":subQ1,"instanceName":"66"}),makeQuery(id+"F6.opPattern","COPY",FACE,{"derivedFrom":subQ1,"instanceName":"67"}),makeQuery(id+"F6.opPattern","COPY",FACE,{"derivedFrom":subQ1,"instanceName":"68"}),makeQuery(id+"F6.opPattern","COPY",FACE,{"derivedFrom":subQ1,"instanceName":"69"}),makeQuery(id+"F6.opPattern","COPY",FACE,{"derivedFrom":subQ1,"instanceName":"70"}),makeQuery(id+"F6.opPattern","COPY",FACE,{"derivedFrom":subQ1,"instanceName":"71"}),makeQuery(id+"F6.opPattern","COPY",FACE,{"derivedFrom":subQ1,"instanceName":"72"}),makeQuery(id+"F6.opPattern","COPY",FACE,{"derivedFrom":subQ1,"instanceName":"73"}),makeQuery(id+"F6.opPattern","COPY",FACE,{"derivedFrom":subQ1,"instanceName":"74"}),makeQuery(id+"F6.opPattern","COPY",FACE,{"derivedFrom":subQ1,"instanceName":"75"}),makeQuery(id+"F6.opPattern","COPY",FACE,{"derivedFrom":subQ1,"instanceName":"76"}),makeQuery(id+"F6.opPattern","COPY",FACE,{"derivedFrom":subQ1,"instanceName":"77"}),makeQuery(id+"F6.opPattern","COPY",FACE,{"derivedFrom":subQ1,"instanceName":"78"})]})],"blendedInto":[makeQuery(id+"F6.boolean.opBoolean","MERGE",FACE,{"derivedFrom":[subQ1,makeQuery(id+"F6.opPattern","COPY",FACE,{"derivedFrom":subQ1,"instanceName":"1"}),makeQuery(id+"F6.opPattern","COPY",FACE,{"derivedFrom":subQ1,"instanceName":"2"}),makeQuery(id+"F6.opPattern","COPY",FACE,{"derivedFrom":subQ1,"instanceName":"3"}),makeQuery(id+"F6.opPattern","COPY",FACE,{"derivedFrom":subQ1,"instanceName":"4"}),makeQuery(id+"F6.opPattern","COPY",FACE,{"derivedFrom":subQ1,"instanceName":"5"}),makeQuery(id+"F6.opPattern","COPY",FACE,{"derivedFrom":subQ1,"instanceName":"6"}),makeQuery(id+"F6.opPattern","COPY",FACE,{"derivedFrom":subQ1,"instanceName":"7"}),makeQuery(id+"F6.opPattern","COPY",FACE,{"derivedFrom":subQ1,"instanceName":"8"}),makeQuery(id+"F6.opPattern","COPY",FACE,{"derivedFrom":subQ1,"instanceName":"9"}),makeQuery(id+"F6.opPattern","COPY",FACE,{"derivedFrom":subQ1,"instanceName":"10"}),makeQuery(id+"F6.opPattern","COPY",FACE,{"derivedFrom":subQ1,"instanceName":"11"}),makeQuery(id+"F6.opPattern","COPY",FACE,{"derivedFrom":subQ1,"instanceName":"12"}),makeQuery(id+"F6.opPattern","COPY",FACE,{"derivedFrom":subQ1,"instanceName":"13"}),makeQuery(id+"F6.opPattern","COPY",FACE,{"derivedFrom":subQ1,"instanceName":"14"}),makeQuery(id+"F6.opPattern","COPY",FACE,{"derivedFrom":subQ1,"instanceName":"15"}),makeQuery(id+"F6.opPattern","COPY",FACE,{"derivedFrom":subQ1,"instanceName":"16"}),makeQuery(id+"F6.opPattern","COPY",FACE,{"derivedFrom":subQ1,"instanceName":"17"}),makeQuery(id+"F6.opPattern","COPY",FACE,{"derivedFrom":subQ1,"instanceName":"18"}),makeQuery(id+"F6.opPattern","COPY",FACE,{"derivedFrom":subQ1,"instanceName":"19"}),makeQuery(id+"F6.opPattern","COPY",FACE,{"derivedFrom":subQ1,"instanceName":"20"}),makeQuery(id+"F6.opPattern","COPY",FACE,{"derivedFrom":subQ1,"instanceName":"21"}),makeQuery(id+"F6.opPattern","COPY",FACE,{"derivedFrom":subQ1,"instanceName":"22"}),makeQuery(id+"F6.opPattern","COPY",FACE,{"derivedFrom":subQ1,"instanceName":"23"}),makeQuery(id+"F6.opPattern","COPY",FACE,{"derivedFrom":subQ1,"instanceName":"24"}),makeQuery(id+"F6.opPattern","COPY",FACE,{"derivedFrom":subQ1,"instanceName":"25"}),makeQuery(id+"F6.opPattern","COPY",FACE,{"derivedFrom":subQ1,"instanceName":"26"}),makeQuery(id+"F6.opPattern","COPY",FACE,{"derivedFrom":subQ1,"instanceName":"27"}),makeQuery(id+"F6.opPattern","COPY",FACE,{"derivedFrom":subQ1,"instanceName":"28"}),makeQuery(id+"F6.opPattern","COPY",FACE,{"derivedFrom":subQ1,"instanceName":"29"}),makeQuery(id+"F6.opPattern","COPY",FACE,{"derivedFrom":subQ1,"instanceName":"30"}),makeQuery(id+"F6.opPattern","COPY",FACE,{"derivedFrom":subQ1,"instanceName":"31"}),makeQuery(id+"F6.opPattern","COPY",FACE,{"derivedFrom":subQ1,"instanceName":"32"}),makeQuery(id+"F6.opPattern","COPY",FACE,{"derivedFrom":subQ1,"instanceName":"33"}),makeQuery(id+"F6.opPattern","COPY",FACE,{"derivedFrom":subQ1,"instanceName":"34"}),makeQuery(id+"F6.opPattern","COPY",FACE,{"derivedFrom":subQ1,"instanceName":"35"}),makeQuery(id+"F6.opPattern","COPY",FACE,{"derivedFrom":subQ1,"instanceName":"36"}),makeQuery(id+"F6.opPattern","COPY",FACE,{"derivedFrom":subQ1,"instanceName":"37"}),makeQuery(id+"F6.opPattern","COPY",FACE,{"derivedFrom":subQ1,"instanceName":"38"}),makeQuery(id+"F6.opPattern","COPY",FACE,{"derivedFrom":subQ1,"instanceName":"39"}),makeQuery(id+"F6.opPattern","COPY",FACE,{"derivedFrom":subQ1,"instanceName":"40"}),makeQuery(id+"F6.opPattern","COPY",FACE,{"derivedFrom":subQ1,"instanceName":"41"}),makeQuery(id+"F6.opPattern","COPY",FACE,{"derivedFrom":subQ1,"instanceName":"42"}),makeQuery(id+"F6.opPattern","COPY",FACE,{"derivedFrom":subQ1,"instanceName":"43"}),makeQuery(id+"F6.opPattern","COPY",FACE,{"derivedFrom":subQ1,"instanceName":"44"}),makeQuery(id+"F6.opPattern","COPY",FACE,{"derivedFrom":subQ1,"instanceName":"45"}),makeQuery(id+"F6.opPattern","COPY",FACE,{"derivedFrom":subQ1,"instanceName":"46"}),makeQuery(id+"F6.opPattern","COPY",FACE,{"derivedFrom":subQ1,"instanceName":"47"}),makeQuery(id+"F6.opPattern","COPY",FACE,{"derivedFrom":subQ1,"instanceName":"48"}),makeQuery(id+"F6.opPattern","COPY",FACE,{"derivedFrom":subQ1,"instanceName":"49"}),makeQuery(id+"F6.opPattern","COPY",FACE,{"derivedFrom":subQ1,"instanceName":"50"}),makeQuery(id+"F6.opPattern","COPY",FACE,{"derivedFrom":subQ1,"instanceName":"51"}),makeQuery(id+"F6.opPattern","COPY",FACE,{"derivedFrom":subQ1,"instanceName":"52"}),makeQuery(id+"F6.opPattern","COPY",FACE,{"derivedFrom":subQ1,"instanceName":"53"}),makeQuery(id+"F6.opPattern","COPY",FACE,{"derivedFrom":subQ1,"instanceName":"54"}),makeQuery(id+"F6.opPattern","COPY",FACE,{"derivedFrom":subQ1,"instanceName":"55"}),makeQuery(id+"F6.opPattern","COPY",FACE,{"derivedFrom":subQ1,"instanceName":"56"}),makeQuery(id+"F6.opPattern","COPY",FACE,{"derivedFrom":subQ1,"instanceName":"57"}),makeQuery(id+"F6.opPattern","COPY",FACE,{"derivedFrom":subQ1,"instanceName":"58"}),makeQuery(id+"F6.opPattern","COPY",FACE,{"derivedFrom":subQ1,"instanceName":"59"}),makeQuery(id+"F6.opPattern","COPY",FACE,{"derivedFrom":subQ1,"instanceName":"60"}),makeQuery(id+"F6.opPattern","COPY",FACE,{"derivedFrom":subQ1,"instanceName":"61"}),makeQuery(id+"F6.opPattern","COPY",FACE,{"derivedFrom":subQ1,"instanceName":"62"}),makeQuery(id+"F6.opPattern","COPY",FACE,{"derivedFrom":subQ1,"instanceName":"63"}),makeQuery(id+"F6.opPattern","COPY",FACE,{"derivedFrom":subQ1,"instanceName":"64"}),makeQuery(id+"F6.opPattern","COPY",FACE,{"derivedFrom":subQ1,"instanceName":"65"}),makeQuery(id+"F6.opPattern","COPY",FACE,{"derivedFrom":subQ1,"instanceName":"66"}),makeQuery(id+"F6.opPattern","COPY",FACE,{"derivedFrom":subQ1,"instanceName":"67"}),makeQuery(id+"F6.opPattern","COPY",FACE,{"derivedFrom":subQ1,"instanceName":"68"}),makeQuery(id+"F6.opPattern","COPY",FACE,{"derivedFrom":subQ1,"instanceName":"69"}),makeQuery(id+"F6.opPattern","COPY",FACE,{"derivedFrom":subQ1,"instanceName":"70"}),makeQuery(id+"F6.opPattern","COPY",FACE,{"derivedFrom":subQ1,"instanceName":"71"}),makeQuery(id+"F6.opPattern","COPY",FACE,{"derivedFrom":subQ1,"instanceName":"72"}),makeQuery(id+"F6.opPattern","COPY",FACE,{"derivedFrom":subQ1,"instanceName":"73"}),makeQuery(id+"F6.opPattern","COPY",FACE,{"derivedFrom":subQ1,"instanceName":"74"}),makeQuery(id+"F6.opPattern","COPY",FACE,{"derivedFrom":subQ1,"instanceName":"75"}),makeQuery(id+"F6.opPattern","COPY",FACE,{"derivedFrom":subQ1,"instanceName":"76"}),makeQuery(id+"F6.opPattern","COPY",FACE,{"derivedFrom":subQ1,"instanceName":"77"}),makeQuery(id+"F6.opPattern","COPY",FACE,{"derivedFrom":subQ1,"instanceName":"78"})]})]});}
            var Q1;
            {var subQ0=sQuery(id+"F2.wireOp",EDGE,"E0");var subQ1=makeQuery(id+"F5.boolean.opBoolean","MERGE",FACE,{"derivedFrom":[makeQuery(id+"F4.opExtrude","CAP_FACE",FACE,{"disambiguationData":[OSD([subQ0])],"isStart":false}),makeQuery(id+"F5.opExtrude","CAP_FACE",FACE,{"disambiguationData":[OSD([subQ0,sQuery(id+"F2.wireOp",EDGE,"E1"),sQuery(id+"F2.wireOp",EDGE,"E2"),sQuery(id+"F2.wireOp",EDGE,"E3")])],"isStart":false})]});Q1=makeQuery(id+"F9.opChamfer","BLEND_EDGE",EDGE,{"blendedFrom":[makeQuery(id+"F8.boolean.opBoolean","COPY",EDGE,{"derivedFrom":makeQuery(id+"F8.opExtrude","CAP_EDGE",EDGE,{"disambiguationData":[OSD([sQuery(id+"F7.wireOp",EDGE,"E14")])],"isStart":true})}),makeQuery(id+"F6.boolean.opBoolean","MERGE",FACE,{"derivedFrom":[subQ1,makeQuery(id+"F6.opPattern","COPY",FACE,{"derivedFrom":subQ1,"instanceName":"1"}),makeQuery(id+"F6.opPattern","COPY",FACE,{"derivedFrom":subQ1,"instanceName":"2"}),makeQuery(id+"F6.opPattern","COPY",FACE,{"derivedFrom":subQ1,"instanceName":"3"}),makeQuery(id+"F6.opPattern","COPY",FACE,{"derivedFrom":subQ1,"instanceName":"4"}),makeQuery(id+"F6.opPattern","COPY",FACE,{"derivedFrom":subQ1,"instanceName":"5"}),makeQuery(id+"F6.opPattern","COPY",FACE,{"derivedFrom":subQ1,"instanceName":"6"}),makeQuery(id+"F6.opPattern","COPY",FACE,{"derivedFrom":subQ1,"instanceName":"7"}),makeQuery(id+"F6.opPattern","COPY",FACE,{"derivedFrom":subQ1,"instanceName":"8"}),makeQuery(id+"F6.opPattern","COPY",FACE,{"derivedFrom":subQ1,"instanceName":"9"}),makeQuery(id+"F6.opPattern","COPY",FACE,{"derivedFrom":subQ1,"instanceName":"10"}),makeQuery(id+"F6.opPattern","COPY",FACE,{"derivedFrom":subQ1,"instanceName":"11"}),makeQuery(id+"F6.opPattern","COPY",FACE,{"derivedFrom":subQ1,"instanceName":"12"}),makeQuery(id+"F6.opPattern","COPY",FACE,{"derivedFrom":subQ1,"instanceName":"13"}),makeQuery(id+"F6.opPattern","COPY",FACE,{"derivedFrom":subQ1,"instanceName":"14"}),makeQuery(id+"F6.opPattern","COPY",FACE,{"derivedFrom":subQ1,"instanceName":"15"}),makeQuery(id+"F6.opPattern","COPY",FACE,{"derivedFrom":subQ1,"instanceName":"16"}),makeQuery(id+"F6.opPattern","COPY",FACE,{"derivedFrom":subQ1,"instanceName":"17"}),makeQuery(id+"F6.opPattern","COPY",FACE,{"derivedFrom":subQ1,"instanceName":"18"}),makeQuery(id+"F6.opPattern","COPY",FACE,{"derivedFrom":subQ1,"instanceName":"19"}),makeQuery(id+"F6.opPattern","COPY",FACE,{"derivedFrom":subQ1,"instanceName":"20"}),makeQuery(id+"F6.opPattern","COPY",FACE,{"derivedFrom":subQ1,"instanceName":"21"}),makeQuery(id+"F6.opPattern","COPY",FACE,{"derivedFrom":subQ1,"instanceName":"22"}),makeQuery(id+"F6.opPattern","COPY",FACE,{"derivedFrom":subQ1,"instanceName":"23"}),makeQuery(id+"F6.opPattern","COPY",FACE,{"derivedFrom":subQ1,"instanceName":"24"}),makeQuery(id+"F6.opPattern","COPY",FACE,{"derivedFrom":subQ1,"instanceName":"25"}),makeQuery(id+"F6.opPattern","COPY",FACE,{"derivedFrom":subQ1,"instanceName":"26"}),makeQuery(id+"F6.opPattern","COPY",FACE,{"derivedFrom":subQ1,"instanceName":"27"}),makeQuery(id+"F6.opPattern","COPY",FACE,{"derivedFrom":subQ1,"instanceName":"28"}),makeQuery(id+"F6.opPattern","COPY",FACE,{"derivedFrom":subQ1,"instanceName":"29"}),makeQuery(id+"F6.opPattern","COPY",FACE,{"derivedFrom":subQ1,"instanceName":"30"}),makeQuery(id+"F6.opPattern","COPY",FACE,{"derivedFrom":subQ1,"instanceName":"31"}),makeQuery(id+"F6.opPattern","COPY",FACE,{"derivedFrom":subQ1,"instanceName":"32"}),makeQuery(id+"F6.opPattern","COPY",FACE,{"derivedFrom":subQ1,"instanceName":"33"}),makeQuery(id+"F6.opPattern","COPY",FACE,{"derivedFrom":subQ1,"instanceName":"34"}),makeQuery(id+"F6.opPattern","COPY",FACE,{"derivedFrom":subQ1,"instanceName":"35"}),makeQuery(id+"F6.opPattern","COPY",FACE,{"derivedFrom":subQ1,"instanceName":"36"}),makeQuery(id+"F6.opPattern","COPY",FACE,{"derivedFrom":subQ1,"instanceName":"37"}),makeQuery(id+"F6.opPattern","COPY",FACE,{"derivedFrom":subQ1,"instanceName":"38"}),makeQuery(id+"F6.opPattern","COPY",FACE,{"derivedFrom":subQ1,"instanceName":"39"}),makeQuery(id+"F6.opPattern","COPY",FACE,{"derivedFrom":subQ1,"instanceName":"40"}),makeQuery(id+"F6.opPattern","COPY",FACE,{"derivedFrom":subQ1,"instanceName":"41"}),makeQuery(id+"F6.opPattern","COPY",FACE,{"derivedFrom":subQ1,"instanceName":"42"}),makeQuery(id+"F6.opPattern","COPY",FACE,{"derivedFrom":subQ1,"instanceName":"43"}),makeQuery(id+"F6.opPattern","COPY",FACE,{"derivedFrom":subQ1,"instanceName":"44"}),makeQuery(id+"F6.opPattern","COPY",FACE,{"derivedFrom":subQ1,"instanceName":"45"}),makeQuery(id+"F6.opPattern","COPY",FACE,{"derivedFrom":subQ1,"instanceName":"46"}),makeQuery(id+"F6.opPattern","COPY",FACE,{"derivedFrom":subQ1,"instanceName":"47"}),makeQuery(id+"F6.opPattern","COPY",FACE,{"derivedFrom":subQ1,"instanceName":"48"}),makeQuery(id+"F6.opPattern","COPY",FACE,{"derivedFrom":subQ1,"instanceName":"49"}),makeQuery(id+"F6.opPattern","COPY",FACE,{"derivedFrom":subQ1,"instanceName":"50"}),makeQuery(id+"F6.opPattern","COPY",FACE,{"derivedFrom":subQ1,"instanceName":"51"}),makeQuery(id+"F6.opPattern","COPY",FACE,{"derivedFrom":subQ1,"instanceName":"52"}),makeQuery(id+"F6.opPattern","COPY",FACE,{"derivedFrom":subQ1,"instanceName":"53"}),makeQuery(id+"F6.opPattern","COPY",FACE,{"derivedFrom":subQ1,"instanceName":"54"}),makeQuery(id+"F6.opPattern","COPY",FACE,{"derivedFrom":subQ1,"instanceName":"55"}),makeQuery(id+"F6.opPattern","COPY",FACE,{"derivedFrom":subQ1,"instanceName":"56"}),makeQuery(id+"F6.opPattern","COPY",FACE,{"derivedFrom":subQ1,"instanceName":"57"}),makeQuery(id+"F6.opPattern","COPY",FACE,{"derivedFrom":subQ1,"instanceName":"58"}),makeQuery(id+"F6.opPattern","COPY",FACE,{"derivedFrom":subQ1,"instanceName":"59"}),makeQuery(id+"F6.opPattern","COPY",FACE,{"derivedFrom":subQ1,"instanceName":"60"}),makeQuery(id+"F6.opPattern","COPY",FACE,{"derivedFrom":subQ1,"instanceName":"61"}),makeQuery(id+"F6.opPattern","COPY",FACE,{"derivedFrom":subQ1,"instanceName":"62"}),makeQuery(id+"F6.opPattern","COPY",FACE,{"derivedFrom":subQ1,"instanceName":"63"}),makeQuery(id+"F6.opPattern","COPY",FACE,{"derivedFrom":subQ1,"instanceName":"64"}),makeQuery(id+"F6.opPattern","COPY",FACE,{"derivedFrom":subQ1,"instanceName":"65"}),makeQuery(id+"F6.opPattern","COPY",FACE,{"derivedFrom":subQ1,"instanceName":"66"}),makeQuery(id+"F6.opPattern","COPY",FACE,{"derivedFrom":subQ1,"instanceName":"67"}),makeQuery(id+"F6.opPattern","COPY",FACE,{"derivedFrom":subQ1,"instanceName":"68"}),makeQuery(id+"F6.opPattern","COPY",FACE,{"derivedFrom":subQ1,"instanceName":"69"}),makeQuery(id+"F6.opPattern","COPY",FACE,{"derivedFrom":subQ1,"instanceName":"70"}),makeQuery(id+"F6.opPattern","COPY",FACE,{"derivedFrom":subQ1,"instanceName":"71"}),makeQuery(id+"F6.opPattern","COPY",FACE,{"derivedFrom":subQ1,"instanceName":"72"}),makeQuery(id+"F6.opPattern","COPY",FACE,{"derivedFrom":subQ1,"instanceName":"73"}),makeQuery(id+"F6.opPattern","COPY",FACE,{"derivedFrom":subQ1,"instanceName":"74"}),makeQuery(id+"F6.opPattern","COPY",FACE,{"derivedFrom":subQ1,"instanceName":"75"}),makeQuery(id+"F6.opPattern","COPY",FACE,{"derivedFrom":subQ1,"instanceName":"76"}),makeQuery(id+"F6.opPattern","COPY",FACE,{"derivedFrom":subQ1,"instanceName":"77"}),makeQuery(id+"F6.opPattern","COPY",FACE,{"derivedFrom":subQ1,"instanceName":"78"})]})],"blendedInto":[makeQuery(id+"F6.boolean.opBoolean","MERGE",FACE,{"derivedFrom":[subQ1,makeQuery(id+"F6.opPattern","COPY",FACE,{"derivedFrom":subQ1,"instanceName":"1"}),makeQuery(id+"F6.opPattern","COPY",FACE,{"derivedFrom":subQ1,"instanceName":"2"}),makeQuery(id+"F6.opPattern","COPY",FACE,{"derivedFrom":subQ1,"instanceName":"3"}),makeQuery(id+"F6.opPattern","COPY",FACE,{"derivedFrom":subQ1,"instanceName":"4"}),makeQuery(id+"F6.opPattern","COPY",FACE,{"derivedFrom":subQ1,"instanceName":"5"}),makeQuery(id+"F6.opPattern","COPY",FACE,{"derivedFrom":subQ1,"instanceName":"6"}),makeQuery(id+"F6.opPattern","COPY",FACE,{"derivedFrom":subQ1,"instanceName":"7"}),makeQuery(id+"F6.opPattern","COPY",FACE,{"derivedFrom":subQ1,"instanceName":"8"}),makeQuery(id+"F6.opPattern","COPY",FACE,{"derivedFrom":subQ1,"instanceName":"9"}),makeQuery(id+"F6.opPattern","COPY",FACE,{"derivedFrom":subQ1,"instanceName":"10"}),makeQuery(id+"F6.opPattern","COPY",FACE,{"derivedFrom":subQ1,"instanceName":"11"}),makeQuery(id+"F6.opPattern","COPY",FACE,{"derivedFrom":subQ1,"instanceName":"12"}),makeQuery(id+"F6.opPattern","COPY",FACE,{"derivedFrom":subQ1,"instanceName":"13"}),makeQuery(id+"F6.opPattern","COPY",FACE,{"derivedFrom":subQ1,"instanceName":"14"}),makeQuery(id+"F6.opPattern","COPY",FACE,{"derivedFrom":subQ1,"instanceName":"15"}),makeQuery(id+"F6.opPattern","COPY",FACE,{"derivedFrom":subQ1,"instanceName":"16"}),makeQuery(id+"F6.opPattern","COPY",FACE,{"derivedFrom":subQ1,"instanceName":"17"}),makeQuery(id+"F6.opPattern","COPY",FACE,{"derivedFrom":subQ1,"instanceName":"18"}),makeQuery(id+"F6.opPattern","COPY",FACE,{"derivedFrom":subQ1,"instanceName":"19"}),makeQuery(id+"F6.opPattern","COPY",FACE,{"derivedFrom":subQ1,"instanceName":"20"}),makeQuery(id+"F6.opPattern","COPY",FACE,{"derivedFrom":subQ1,"instanceName":"21"}),makeQuery(id+"F6.opPattern","COPY",FACE,{"derivedFrom":subQ1,"instanceName":"22"}),makeQuery(id+"F6.opPattern","COPY",FACE,{"derivedFrom":subQ1,"instanceName":"23"}),makeQuery(id+"F6.opPattern","COPY",FACE,{"derivedFrom":subQ1,"instanceName":"24"}),makeQuery(id+"F6.opPattern","COPY",FACE,{"derivedFrom":subQ1,"instanceName":"25"}),makeQuery(id+"F6.opPattern","COPY",FACE,{"derivedFrom":subQ1,"instanceName":"26"}),makeQuery(id+"F6.opPattern","COPY",FACE,{"derivedFrom":subQ1,"instanceName":"27"}),makeQuery(id+"F6.opPattern","COPY",FACE,{"derivedFrom":subQ1,"instanceName":"28"}),makeQuery(id+"F6.opPattern","COPY",FACE,{"derivedFrom":subQ1,"instanceName":"29"}),makeQuery(id+"F6.opPattern","COPY",FACE,{"derivedFrom":subQ1,"instanceName":"30"}),makeQuery(id+"F6.opPattern","COPY",FACE,{"derivedFrom":subQ1,"instanceName":"31"}),makeQuery(id+"F6.opPattern","COPY",FACE,{"derivedFrom":subQ1,"instanceName":"32"}),makeQuery(id+"F6.opPattern","COPY",FACE,{"derivedFrom":subQ1,"instanceName":"33"}),makeQuery(id+"F6.opPattern","COPY",FACE,{"derivedFrom":subQ1,"instanceName":"34"}),makeQuery(id+"F6.opPattern","COPY",FACE,{"derivedFrom":subQ1,"instanceName":"35"}),makeQuery(id+"F6.opPattern","COPY",FACE,{"derivedFrom":subQ1,"instanceName":"36"}),makeQuery(id+"F6.opPattern","COPY",FACE,{"derivedFrom":subQ1,"instanceName":"37"}),makeQuery(id+"F6.opPattern","COPY",FACE,{"derivedFrom":subQ1,"instanceName":"38"}),makeQuery(id+"F6.opPattern","COPY",FACE,{"derivedFrom":subQ1,"instanceName":"39"}),makeQuery(id+"F6.opPattern","COPY",FACE,{"derivedFrom":subQ1,"instanceName":"40"}),makeQuery(id+"F6.opPattern","COPY",FACE,{"derivedFrom":subQ1,"instanceName":"41"}),makeQuery(id+"F6.opPattern","COPY",FACE,{"derivedFrom":subQ1,"instanceName":"42"}),makeQuery(id+"F6.opPattern","COPY",FACE,{"derivedFrom":subQ1,"instanceName":"43"}),makeQuery(id+"F6.opPattern","COPY",FACE,{"derivedFrom":subQ1,"instanceName":"44"}),makeQuery(id+"F6.opPattern","COPY",FACE,{"derivedFrom":subQ1,"instanceName":"45"}),makeQuery(id+"F6.opPattern","COPY",FACE,{"derivedFrom":subQ1,"instanceName":"46"}),makeQuery(id+"F6.opPattern","COPY",FACE,{"derivedFrom":subQ1,"instanceName":"47"}),makeQuery(id+"F6.opPattern","COPY",FACE,{"derivedFrom":subQ1,"instanceName":"48"}),makeQuery(id+"F6.opPattern","COPY",FACE,{"derivedFrom":subQ1,"instanceName":"49"}),makeQuery(id+"F6.opPattern","COPY",FACE,{"derivedFrom":subQ1,"instanceName":"50"}),makeQuery(id+"F6.opPattern","COPY",FACE,{"derivedFrom":subQ1,"instanceName":"51"}),makeQuery(id+"F6.opPattern","COPY",FACE,{"derivedFrom":subQ1,"instanceName":"52"}),makeQuery(id+"F6.opPattern","COPY",FACE,{"derivedFrom":subQ1,"instanceName":"53"}),makeQuery(id+"F6.opPattern","COPY",FACE,{"derivedFrom":subQ1,"instanceName":"54"}),makeQuery(id+"F6.opPattern","COPY",FACE,{"derivedFrom":subQ1,"instanceName":"55"}),makeQuery(id+"F6.opPattern","COPY",FACE,{"derivedFrom":subQ1,"instanceName":"56"}),makeQuery(id+"F6.opPattern","COPY",FACE,{"derivedFrom":subQ1,"instanceName":"57"}),makeQuery(id+"F6.opPattern","COPY",FACE,{"derivedFrom":subQ1,"instanceName":"58"}),makeQuery(id+"F6.opPattern","COPY",FACE,{"derivedFrom":subQ1,"instanceName":"59"}),makeQuery(id+"F6.opPattern","COPY",FACE,{"derivedFrom":subQ1,"instanceName":"60"}),makeQuery(id+"F6.opPattern","COPY",FACE,{"derivedFrom":subQ1,"instanceName":"61"}),makeQuery(id+"F6.opPattern","COPY",FACE,{"derivedFrom":subQ1,"instanceName":"62"}),makeQuery(id+"F6.opPattern","COPY",FACE,{"derivedFrom":subQ1,"instanceName":"63"}),makeQuery(id+"F6.opPattern","COPY",FACE,{"derivedFrom":subQ1,"instanceName":"64"}),makeQuery(id+"F6.opPattern","COPY",FACE,{"derivedFrom":subQ1,"instanceName":"65"}),makeQuery(id+"F6.opPattern","COPY",FACE,{"derivedFrom":subQ1,"instanceName":"66"}),makeQuery(id+"F6.opPattern","COPY",FACE,{"derivedFrom":subQ1,"instanceName":"67"}),makeQuery(id+"F6.opPattern","COPY",FACE,{"derivedFrom":subQ1,"instanceName":"68"}),makeQuery(id+"F6.opPattern","COPY",FACE,{"derivedFrom":subQ1,"instanceName":"69"}),makeQuery(id+"F6.opPattern","COPY",FACE,{"derivedFrom":subQ1,"instanceName":"70"}),makeQuery(id+"F6.opPattern","COPY",FACE,{"derivedFrom":subQ1,"instanceName":"71"}),makeQuery(id+"F6.opPattern","COPY",FACE,{"derivedFrom":subQ1,"instanceName":"72"}),makeQuery(id+"F6.opPattern","COPY",FACE,{"derivedFrom":subQ1,"instanceName":"73"}),makeQuery(id+"F6.opPattern","COPY",FACE,{"derivedFrom":subQ1,"instanceName":"74"}),makeQuery(id+"F6.opPattern","COPY",FACE,{"derivedFrom":subQ1,"instanceName":"75"}),makeQuery(id+"F6.opPattern","COPY",FACE,{"derivedFrom":subQ1,"instanceName":"76"}),makeQuery(id+"F6.opPattern","COPY",FACE,{"derivedFrom":subQ1,"instanceName":"77"}),makeQuery(id+"F6.opPattern","COPY",FACE,{"derivedFrom":subQ1,"instanceName":"78"})]})]});}
            var Q2;
            {var subQ0=sQuery(id+"F2.wireOp",EDGE,"E0");var subQ1=makeQuery(id+"F5.boolean.opBoolean","MERGE",FACE,{"derivedFrom":[makeQuery(id+"F4.opExtrude","CAP_FACE",FACE,{"disambiguationData":[OSD([subQ0])],"isStart":false}),makeQuery(id+"F5.opExtrude","CAP_FACE",FACE,{"disambiguationData":[OSD([subQ0,sQuery(id+"F2.wireOp",EDGE,"E1"),sQuery(id+"F2.wireOp",EDGE,"E2"),sQuery(id+"F2.wireOp",EDGE,"E3")])],"isStart":false})]});Q2=makeQuery(id+"F9.opChamfer","BLEND_EDGE",EDGE,{"blendedFrom":[makeQuery(id+"F8.boolean.opBoolean","COPY",EDGE,{"derivedFrom":makeQuery(id+"F8.opExtrude","CAP_EDGE",EDGE,{"disambiguationData":[OSD([sQuery(id+"F7.wireOp",EDGE,"E16.1.5.0")])],"isStart":true})}),makeQuery(id+"F6.boolean.opBoolean","MERGE",FACE,{"derivedFrom":[subQ1,makeQuery(id+"F6.opPattern","COPY",FACE,{"derivedFrom":subQ1,"instanceName":"1"}),makeQuery(id+"F6.opPattern","COPY",FACE,{"derivedFrom":subQ1,"instanceName":"2"}),makeQuery(id+"F6.opPattern","COPY",FACE,{"derivedFrom":subQ1,"instanceName":"3"}),makeQuery(id+"F6.opPattern","COPY",FACE,{"derivedFrom":subQ1,"instanceName":"4"}),makeQuery(id+"F6.opPattern","COPY",FACE,{"derivedFrom":subQ1,"instanceName":"5"}),makeQuery(id+"F6.opPattern","COPY",FACE,{"derivedFrom":subQ1,"instanceName":"6"}),makeQuery(id+"F6.opPattern","COPY",FACE,{"derivedFrom":subQ1,"instanceName":"7"}),makeQuery(id+"F6.opPattern","COPY",FACE,{"derivedFrom":subQ1,"instanceName":"8"}),makeQuery(id+"F6.opPattern","COPY",FACE,{"derivedFrom":subQ1,"instanceName":"9"}),makeQuery(id+"F6.opPattern","COPY",FACE,{"derivedFrom":subQ1,"instanceName":"10"}),makeQuery(id+"F6.opPattern","COPY",FACE,{"derivedFrom":subQ1,"instanceName":"11"}),makeQuery(id+"F6.opPattern","COPY",FACE,{"derivedFrom":subQ1,"instanceName":"12"}),makeQuery(id+"F6.opPattern","COPY",FACE,{"derivedFrom":subQ1,"instanceName":"13"}),makeQuery(id+"F6.opPattern","COPY",FACE,{"derivedFrom":subQ1,"instanceName":"14"}),makeQuery(id+"F6.opPattern","COPY",FACE,{"derivedFrom":subQ1,"instanceName":"15"}),makeQuery(id+"F6.opPattern","COPY",FACE,{"derivedFrom":subQ1,"instanceName":"16"}),makeQuery(id+"F6.opPattern","COPY",FACE,{"derivedFrom":subQ1,"instanceName":"17"}),makeQuery(id+"F6.opPattern","COPY",FACE,{"derivedFrom":subQ1,"instanceName":"18"}),makeQuery(id+"F6.opPattern","COPY",FACE,{"derivedFrom":subQ1,"instanceName":"19"}),makeQuery(id+"F6.opPattern","COPY",FACE,{"derivedFrom":subQ1,"instanceName":"20"}),makeQuery(id+"F6.opPattern","COPY",FACE,{"derivedFrom":subQ1,"instanceName":"21"}),makeQuery(id+"F6.opPattern","COPY",FACE,{"derivedFrom":subQ1,"instanceName":"22"}),makeQuery(id+"F6.opPattern","COPY",FACE,{"derivedFrom":subQ1,"instanceName":"23"}),makeQuery(id+"F6.opPattern","COPY",FACE,{"derivedFrom":subQ1,"instanceName":"24"}),makeQuery(id+"F6.opPattern","COPY",FACE,{"derivedFrom":subQ1,"instanceName":"25"}),makeQuery(id+"F6.opPattern","COPY",FACE,{"derivedFrom":subQ1,"instanceName":"26"}),makeQuery(id+"F6.opPattern","COPY",FACE,{"derivedFrom":subQ1,"instanceName":"27"}),makeQuery(id+"F6.opPattern","COPY",FACE,{"derivedFrom":subQ1,"instanceName":"28"}),makeQuery(id+"F6.opPattern","COPY",FACE,{"derivedFrom":subQ1,"instanceName":"29"}),makeQuery(id+"F6.opPattern","COPY",FACE,{"derivedFrom":subQ1,"instanceName":"30"}),makeQuery(id+"F6.opPattern","COPY",FACE,{"derivedFrom":subQ1,"instanceName":"31"}),makeQuery(id+"F6.opPattern","COPY",FACE,{"derivedFrom":subQ1,"instanceName":"32"}),makeQuery(id+"F6.opPattern","COPY",FACE,{"derivedFrom":subQ1,"instanceName":"33"}),makeQuery(id+"F6.opPattern","COPY",FACE,{"derivedFrom":subQ1,"instanceName":"34"}),makeQuery(id+"F6.opPattern","COPY",FACE,{"derivedFrom":subQ1,"instanceName":"35"}),makeQuery(id+"F6.opPattern","COPY",FACE,{"derivedFrom":subQ1,"instanceName":"36"}),makeQuery(id+"F6.opPattern","COPY",FACE,{"derivedFrom":subQ1,"instanceName":"37"}),makeQuery(id+"F6.opPattern","COPY",FACE,{"derivedFrom":subQ1,"instanceName":"38"}),makeQuery(id+"F6.opPattern","COPY",FACE,{"derivedFrom":subQ1,"instanceName":"39"}),makeQuery(id+"F6.opPattern","COPY",FACE,{"derivedFrom":subQ1,"instanceName":"40"}),makeQuery(id+"F6.opPattern","COPY",FACE,{"derivedFrom":subQ1,"instanceName":"41"}),makeQuery(id+"F6.opPattern","COPY",FACE,{"derivedFrom":subQ1,"instanceName":"42"}),makeQuery(id+"F6.opPattern","COPY",FACE,{"derivedFrom":subQ1,"instanceName":"43"}),makeQuery(id+"F6.opPattern","COPY",FACE,{"derivedFrom":subQ1,"instanceName":"44"}),makeQuery(id+"F6.opPattern","COPY",FACE,{"derivedFrom":subQ1,"instanceName":"45"}),makeQuery(id+"F6.opPattern","COPY",FACE,{"derivedFrom":subQ1,"instanceName":"46"}),makeQuery(id+"F6.opPattern","COPY",FACE,{"derivedFrom":subQ1,"instanceName":"47"}),makeQuery(id+"F6.opPattern","COPY",FACE,{"derivedFrom":subQ1,"instanceName":"48"}),makeQuery(id+"F6.opPattern","COPY",FACE,{"derivedFrom":subQ1,"instanceName":"49"}),makeQuery(id+"F6.opPattern","COPY",FACE,{"derivedFrom":subQ1,"instanceName":"50"}),makeQuery(id+"F6.opPattern","COPY",FACE,{"derivedFrom":subQ1,"instanceName":"51"}),makeQuery(id+"F6.opPattern","COPY",FACE,{"derivedFrom":subQ1,"instanceName":"52"}),makeQuery(id+"F6.opPattern","COPY",FACE,{"derivedFrom":subQ1,"instanceName":"53"}),makeQuery(id+"F6.opPattern","COPY",FACE,{"derivedFrom":subQ1,"instanceName":"54"}),makeQuery(id+"F6.opPattern","COPY",FACE,{"derivedFrom":subQ1,"instanceName":"55"}),makeQuery(id+"F6.opPattern","COPY",FACE,{"derivedFrom":subQ1,"instanceName":"56"}),makeQuery(id+"F6.opPattern","COPY",FACE,{"derivedFrom":subQ1,"instanceName":"57"}),makeQuery(id+"F6.opPattern","COPY",FACE,{"derivedFrom":subQ1,"instanceName":"58"}),makeQuery(id+"F6.opPattern","COPY",FACE,{"derivedFrom":subQ1,"instanceName":"59"}),makeQuery(id+"F6.opPattern","COPY",FACE,{"derivedFrom":subQ1,"instanceName":"60"}),makeQuery(id+"F6.opPattern","COPY",FACE,{"derivedFrom":subQ1,"instanceName":"61"}),makeQuery(id+"F6.opPattern","COPY",FACE,{"derivedFrom":subQ1,"instanceName":"62"}),makeQuery(id+"F6.opPattern","COPY",FACE,{"derivedFrom":subQ1,"instanceName":"63"}),makeQuery(id+"F6.opPattern","COPY",FACE,{"derivedFrom":subQ1,"instanceName":"64"}),makeQuery(id+"F6.opPattern","COPY",FACE,{"derivedFrom":subQ1,"instanceName":"65"}),makeQuery(id+"F6.opPattern","COPY",FACE,{"derivedFrom":subQ1,"instanceName":"66"}),makeQuery(id+"F6.opPattern","COPY",FACE,{"derivedFrom":subQ1,"instanceName":"67"}),makeQuery(id+"F6.opPattern","COPY",FACE,{"derivedFrom":subQ1,"instanceName":"68"}),makeQuery(id+"F6.opPattern","COPY",FACE,{"derivedFrom":subQ1,"instanceName":"69"}),makeQuery(id+"F6.opPattern","COPY",FACE,{"derivedFrom":subQ1,"instanceName":"70"}),makeQuery(id+"F6.opPattern","COPY",FACE,{"derivedFrom":subQ1,"instanceName":"71"}),makeQuery(id+"F6.opPattern","COPY",FACE,{"derivedFrom":subQ1,"instanceName":"72"}),makeQuery(id+"F6.opPattern","COPY",FACE,{"derivedFrom":subQ1,"instanceName":"73"}),makeQuery(id+"F6.opPattern","COPY",FACE,{"derivedFrom":subQ1,"instanceName":"74"}),makeQuery(id+"F6.opPattern","COPY",FACE,{"derivedFrom":subQ1,"instanceName":"75"}),makeQuery(id+"F6.opPattern","COPY",FACE,{"derivedFrom":subQ1,"instanceName":"76"}),makeQuery(id+"F6.opPattern","COPY",FACE,{"derivedFrom":subQ1,"instanceName":"77"}),makeQuery(id+"F6.opPattern","COPY",FACE,{"derivedFrom":subQ1,"instanceName":"78"})]})],"blendedInto":[makeQuery(id+"F6.boolean.opBoolean","MERGE",FACE,{"derivedFrom":[subQ1,makeQuery(id+"F6.opPattern","COPY",FACE,{"derivedFrom":subQ1,"instanceName":"1"}),makeQuery(id+"F6.opPattern","COPY",FACE,{"derivedFrom":subQ1,"instanceName":"2"}),makeQuery(id+"F6.opPattern","COPY",FACE,{"derivedFrom":subQ1,"instanceName":"3"}),makeQuery(id+"F6.opPattern","COPY",FACE,{"derivedFrom":subQ1,"instanceName":"4"}),makeQuery(id+"F6.opPattern","COPY",FACE,{"derivedFrom":subQ1,"instanceName":"5"}),makeQuery(id+"F6.opPattern","COPY",FACE,{"derivedFrom":subQ1,"instanceName":"6"}),makeQuery(id+"F6.opPattern","COPY",FACE,{"derivedFrom":subQ1,"instanceName":"7"}),makeQuery(id+"F6.opPattern","COPY",FACE,{"derivedFrom":subQ1,"instanceName":"8"}),makeQuery(id+"F6.opPattern","COPY",FACE,{"derivedFrom":subQ1,"instanceName":"9"}),makeQuery(id+"F6.opPattern","COPY",FACE,{"derivedFrom":subQ1,"instanceName":"10"}),makeQuery(id+"F6.opPattern","COPY",FACE,{"derivedFrom":subQ1,"instanceName":"11"}),makeQuery(id+"F6.opPattern","COPY",FACE,{"derivedFrom":subQ1,"instanceName":"12"}),makeQuery(id+"F6.opPattern","COPY",FACE,{"derivedFrom":subQ1,"instanceName":"13"}),makeQuery(id+"F6.opPattern","COPY",FACE,{"derivedFrom":subQ1,"instanceName":"14"}),makeQuery(id+"F6.opPattern","COPY",FACE,{"derivedFrom":subQ1,"instanceName":"15"}),makeQuery(id+"F6.opPattern","COPY",FACE,{"derivedFrom":subQ1,"instanceName":"16"}),makeQuery(id+"F6.opPattern","COPY",FACE,{"derivedFrom":subQ1,"instanceName":"17"}),makeQuery(id+"F6.opPattern","COPY",FACE,{"derivedFrom":subQ1,"instanceName":"18"}),makeQuery(id+"F6.opPattern","COPY",FACE,{"derivedFrom":subQ1,"instanceName":"19"}),makeQuery(id+"F6.opPattern","COPY",FACE,{"derivedFrom":subQ1,"instanceName":"20"}),makeQuery(id+"F6.opPattern","COPY",FACE,{"derivedFrom":subQ1,"instanceName":"21"}),makeQuery(id+"F6.opPattern","COPY",FACE,{"derivedFrom":subQ1,"instanceName":"22"}),makeQuery(id+"F6.opPattern","COPY",FACE,{"derivedFrom":subQ1,"instanceName":"23"}),makeQuery(id+"F6.opPattern","COPY",FACE,{"derivedFrom":subQ1,"instanceName":"24"}),makeQuery(id+"F6.opPattern","COPY",FACE,{"derivedFrom":subQ1,"instanceName":"25"}),makeQuery(id+"F6.opPattern","COPY",FACE,{"derivedFrom":subQ1,"instanceName":"26"}),makeQuery(id+"F6.opPattern","COPY",FACE,{"derivedFrom":subQ1,"instanceName":"27"}),makeQuery(id+"F6.opPattern","COPY",FACE,{"derivedFrom":subQ1,"instanceName":"28"}),makeQuery(id+"F6.opPattern","COPY",FACE,{"derivedFrom":subQ1,"instanceName":"29"}),makeQuery(id+"F6.opPattern","COPY",FACE,{"derivedFrom":subQ1,"instanceName":"30"}),makeQuery(id+"F6.opPattern","COPY",FACE,{"derivedFrom":subQ1,"instanceName":"31"}),makeQuery(id+"F6.opPattern","COPY",FACE,{"derivedFrom":subQ1,"instanceName":"32"}),makeQuery(id+"F6.opPattern","COPY",FACE,{"derivedFrom":subQ1,"instanceName":"33"}),makeQuery(id+"F6.opPattern","COPY",FACE,{"derivedFrom":subQ1,"instanceName":"34"}),makeQuery(id+"F6.opPattern","COPY",FACE,{"derivedFrom":subQ1,"instanceName":"35"}),makeQuery(id+"F6.opPattern","COPY",FACE,{"derivedFrom":subQ1,"instanceName":"36"}),makeQuery(id+"F6.opPattern","COPY",FACE,{"derivedFrom":subQ1,"instanceName":"37"}),makeQuery(id+"F6.opPattern","COPY",FACE,{"derivedFrom":subQ1,"instanceName":"38"}),makeQuery(id+"F6.opPattern","COPY",FACE,{"derivedFrom":subQ1,"instanceName":"39"}),makeQuery(id+"F6.opPattern","COPY",FACE,{"derivedFrom":subQ1,"instanceName":"40"}),makeQuery(id+"F6.opPattern","COPY",FACE,{"derivedFrom":subQ1,"instanceName":"41"}),makeQuery(id+"F6.opPattern","COPY",FACE,{"derivedFrom":subQ1,"instanceName":"42"}),makeQuery(id+"F6.opPattern","COPY",FACE,{"derivedFrom":subQ1,"instanceName":"43"}),makeQuery(id+"F6.opPattern","COPY",FACE,{"derivedFrom":subQ1,"instanceName":"44"}),makeQuery(id+"F6.opPattern","COPY",FACE,{"derivedFrom":subQ1,"instanceName":"45"}),makeQuery(id+"F6.opPattern","COPY",FACE,{"derivedFrom":subQ1,"instanceName":"46"}),makeQuery(id+"F6.opPattern","COPY",FACE,{"derivedFrom":subQ1,"instanceName":"47"}),makeQuery(id+"F6.opPattern","COPY",FACE,{"derivedFrom":subQ1,"instanceName":"48"}),makeQuery(id+"F6.opPattern","COPY",FACE,{"derivedFrom":subQ1,"instanceName":"49"}),makeQuery(id+"F6.opPattern","COPY",FACE,{"derivedFrom":subQ1,"instanceName":"50"}),makeQuery(id+"F6.opPattern","COPY",FACE,{"derivedFrom":subQ1,"instanceName":"51"}),makeQuery(id+"F6.opPattern","COPY",FACE,{"derivedFrom":subQ1,"instanceName":"52"}),makeQuery(id+"F6.opPattern","COPY",FACE,{"derivedFrom":subQ1,"instanceName":"53"}),makeQuery(id+"F6.opPattern","COPY",FACE,{"derivedFrom":subQ1,"instanceName":"54"}),makeQuery(id+"F6.opPattern","COPY",FACE,{"derivedFrom":subQ1,"instanceName":"55"}),makeQuery(id+"F6.opPattern","COPY",FACE,{"derivedFrom":subQ1,"instanceName":"56"}),makeQuery(id+"F6.opPattern","COPY",FACE,{"derivedFrom":subQ1,"instanceName":"57"}),makeQuery(id+"F6.opPattern","COPY",FACE,{"derivedFrom":subQ1,"instanceName":"58"}),makeQuery(id+"F6.opPattern","COPY",FACE,{"derivedFrom":subQ1,"instanceName":"59"}),makeQuery(id+"F6.opPattern","COPY",FACE,{"derivedFrom":subQ1,"instanceName":"60"}),makeQuery(id+"F6.opPattern","COPY",FACE,{"derivedFrom":subQ1,"instanceName":"61"}),makeQuery(id+"F6.opPattern","COPY",FACE,{"derivedFrom":subQ1,"instanceName":"62"}),makeQuery(id+"F6.opPattern","COPY",FACE,{"derivedFrom":subQ1,"instanceName":"63"}),makeQuery(id+"F6.opPattern","COPY",FACE,{"derivedFrom":subQ1,"instanceName":"64"}),makeQuery(id+"F6.opPattern","COPY",FACE,{"derivedFrom":subQ1,"instanceName":"65"}),makeQuery(id+"F6.opPattern","COPY",FACE,{"derivedFrom":subQ1,"instanceName":"66"}),makeQuery(id+"F6.opPattern","COPY",FACE,{"derivedFrom":subQ1,"instanceName":"67"}),makeQuery(id+"F6.opPattern","COPY",FACE,{"derivedFrom":subQ1,"instanceName":"68"}),makeQuery(id+"F6.opPattern","COPY",FACE,{"derivedFrom":subQ1,"instanceName":"69"}),makeQuery(id+"F6.opPattern","COPY",FACE,{"derivedFrom":subQ1,"instanceName":"70"}),makeQuery(id+"F6.opPattern","COPY",FACE,{"derivedFrom":subQ1,"instanceName":"71"}),makeQuery(id+"F6.opPattern","COPY",FACE,{"derivedFrom":subQ1,"instanceName":"72"}),makeQuery(id+"F6.opPattern","COPY",FACE,{"derivedFrom":subQ1,"instanceName":"73"}),makeQuery(id+"F6.opPattern","COPY",FACE,{"derivedFrom":subQ1,"instanceName":"74"}),makeQuery(id+"F6.opPattern","COPY",FACE,{"derivedFrom":subQ1,"instanceName":"75"}),makeQuery(id+"F6.opPattern","COPY",FACE,{"derivedFrom":subQ1,"instanceName":"76"}),makeQuery(id+"F6.opPattern","COPY",FACE,{"derivedFrom":subQ1,"instanceName":"77"}),makeQuery(id+"F6.opPattern","COPY",FACE,{"derivedFrom":subQ1,"instanceName":"78"})]})]});}
            var Q3;
            {var subQ0=sQuery(id+"F2.wireOp",EDGE,"E0");var subQ1=makeQuery(id+"F5.boolean.opBoolean","MERGE",FACE,{"derivedFrom":[makeQuery(id+"F4.opExtrude","CAP_FACE",FACE,{"disambiguationData":[OSD([subQ0])],"isStart":false}),makeQuery(id+"F5.opExtrude","CAP_FACE",FACE,{"disambiguationData":[OSD([subQ0,sQuery(id+"F2.wireOp",EDGE,"E1"),sQuery(id+"F2.wireOp",EDGE,"E2"),sQuery(id+"F2.wireOp",EDGE,"E3")])],"isStart":false})]});Q3=makeQuery(id+"F9.opChamfer","BLEND_EDGE",EDGE,{"blendedFrom":[makeQuery(id+"F8.boolean.opBoolean","COPY",EDGE,{"derivedFrom":makeQuery(id+"F8.opExtrude","CAP_EDGE",EDGE,{"disambiguationData":[OSD([sQuery(id+"F7.wireOp",EDGE,"E16.1.4.0")])],"isStart":true})}),makeQuery(id+"F6.boolean.opBoolean","MERGE",FACE,{"derivedFrom":[subQ1,makeQuery(id+"F6.opPattern","COPY",FACE,{"derivedFrom":subQ1,"instanceName":"1"}),makeQuery(id+"F6.opPattern","COPY",FACE,{"derivedFrom":subQ1,"instanceName":"2"}),makeQuery(id+"F6.opPattern","COPY",FACE,{"derivedFrom":subQ1,"instanceName":"3"}),makeQuery(id+"F6.opPattern","COPY",FACE,{"derivedFrom":subQ1,"instanceName":"4"}),makeQuery(id+"F6.opPattern","COPY",FACE,{"derivedFrom":subQ1,"instanceName":"5"}),makeQuery(id+"F6.opPattern","COPY",FACE,{"derivedFrom":subQ1,"instanceName":"6"}),makeQuery(id+"F6.opPattern","COPY",FACE,{"derivedFrom":subQ1,"instanceName":"7"}),makeQuery(id+"F6.opPattern","COPY",FACE,{"derivedFrom":subQ1,"instanceName":"8"}),makeQuery(id+"F6.opPattern","COPY",FACE,{"derivedFrom":subQ1,"instanceName":"9"}),makeQuery(id+"F6.opPattern","COPY",FACE,{"derivedFrom":subQ1,"instanceName":"10"}),makeQuery(id+"F6.opPattern","COPY",FACE,{"derivedFrom":subQ1,"instanceName":"11"}),makeQuery(id+"F6.opPattern","COPY",FACE,{"derivedFrom":subQ1,"instanceName":"12"}),makeQuery(id+"F6.opPattern","COPY",FACE,{"derivedFrom":subQ1,"instanceName":"13"}),makeQuery(id+"F6.opPattern","COPY",FACE,{"derivedFrom":subQ1,"instanceName":"14"}),makeQuery(id+"F6.opPattern","COPY",FACE,{"derivedFrom":subQ1,"instanceName":"15"}),makeQuery(id+"F6.opPattern","COPY",FACE,{"derivedFrom":subQ1,"instanceName":"16"}),makeQuery(id+"F6.opPattern","COPY",FACE,{"derivedFrom":subQ1,"instanceName":"17"}),makeQuery(id+"F6.opPattern","COPY",FACE,{"derivedFrom":subQ1,"instanceName":"18"}),makeQuery(id+"F6.opPattern","COPY",FACE,{"derivedFrom":subQ1,"instanceName":"19"}),makeQuery(id+"F6.opPattern","COPY",FACE,{"derivedFrom":subQ1,"instanceName":"20"}),makeQuery(id+"F6.opPattern","COPY",FACE,{"derivedFrom":subQ1,"instanceName":"21"}),makeQuery(id+"F6.opPattern","COPY",FACE,{"derivedFrom":subQ1,"instanceName":"22"}),makeQuery(id+"F6.opPattern","COPY",FACE,{"derivedFrom":subQ1,"instanceName":"23"}),makeQuery(id+"F6.opPattern","COPY",FACE,{"derivedFrom":subQ1,"instanceName":"24"}),makeQuery(id+"F6.opPattern","COPY",FACE,{"derivedFrom":subQ1,"instanceName":"25"}),makeQuery(id+"F6.opPattern","COPY",FACE,{"derivedFrom":subQ1,"instanceName":"26"}),makeQuery(id+"F6.opPattern","COPY",FACE,{"derivedFrom":subQ1,"instanceName":"27"}),makeQuery(id+"F6.opPattern","COPY",FACE,{"derivedFrom":subQ1,"instanceName":"28"}),makeQuery(id+"F6.opPattern","COPY",FACE,{"derivedFrom":subQ1,"instanceName":"29"}),makeQuery(id+"F6.opPattern","COPY",FACE,{"derivedFrom":subQ1,"instanceName":"30"}),makeQuery(id+"F6.opPattern","COPY",FACE,{"derivedFrom":subQ1,"instanceName":"31"}),makeQuery(id+"F6.opPattern","COPY",FACE,{"derivedFrom":subQ1,"instanceName":"32"}),makeQuery(id+"F6.opPattern","COPY",FACE,{"derivedFrom":subQ1,"instanceName":"33"}),makeQuery(id+"F6.opPattern","COPY",FACE,{"derivedFrom":subQ1,"instanceName":"34"}),makeQuery(id+"F6.opPattern","COPY",FACE,{"derivedFrom":subQ1,"instanceName":"35"}),makeQuery(id+"F6.opPattern","COPY",FACE,{"derivedFrom":subQ1,"instanceName":"36"}),makeQuery(id+"F6.opPattern","COPY",FACE,{"derivedFrom":subQ1,"instanceName":"37"}),makeQuery(id+"F6.opPattern","COPY",FACE,{"derivedFrom":subQ1,"instanceName":"38"}),makeQuery(id+"F6.opPattern","COPY",FACE,{"derivedFrom":subQ1,"instanceName":"39"}),makeQuery(id+"F6.opPattern","COPY",FACE,{"derivedFrom":subQ1,"instanceName":"40"}),makeQuery(id+"F6.opPattern","COPY",FACE,{"derivedFrom":subQ1,"instanceName":"41"}),makeQuery(id+"F6.opPattern","COPY",FACE,{"derivedFrom":subQ1,"instanceName":"42"}),makeQuery(id+"F6.opPattern","COPY",FACE,{"derivedFrom":subQ1,"instanceName":"43"}),makeQuery(id+"F6.opPattern","COPY",FACE,{"derivedFrom":subQ1,"instanceName":"44"}),makeQuery(id+"F6.opPattern","COPY",FACE,{"derivedFrom":subQ1,"instanceName":"45"}),makeQuery(id+"F6.opPattern","COPY",FACE,{"derivedFrom":subQ1,"instanceName":"46"}),makeQuery(id+"F6.opPattern","COPY",FACE,{"derivedFrom":subQ1,"instanceName":"47"}),makeQuery(id+"F6.opPattern","COPY",FACE,{"derivedFrom":subQ1,"instanceName":"48"}),makeQuery(id+"F6.opPattern","COPY",FACE,{"derivedFrom":subQ1,"instanceName":"49"}),makeQuery(id+"F6.opPattern","COPY",FACE,{"derivedFrom":subQ1,"instanceName":"50"}),makeQuery(id+"F6.opPattern","COPY",FACE,{"derivedFrom":subQ1,"instanceName":"51"}),makeQuery(id+"F6.opPattern","COPY",FACE,{"derivedFrom":subQ1,"instanceName":"52"}),makeQuery(id+"F6.opPattern","COPY",FACE,{"derivedFrom":subQ1,"instanceName":"53"}),makeQuery(id+"F6.opPattern","COPY",FACE,{"derivedFrom":subQ1,"instanceName":"54"}),makeQuery(id+"F6.opPattern","COPY",FACE,{"derivedFrom":subQ1,"instanceName":"55"}),makeQuery(id+"F6.opPattern","COPY",FACE,{"derivedFrom":subQ1,"instanceName":"56"}),makeQuery(id+"F6.opPattern","COPY",FACE,{"derivedFrom":subQ1,"instanceName":"57"}),makeQuery(id+"F6.opPattern","COPY",FACE,{"derivedFrom":subQ1,"instanceName":"58"}),makeQuery(id+"F6.opPattern","COPY",FACE,{"derivedFrom":subQ1,"instanceName":"59"}),makeQuery(id+"F6.opPattern","COPY",FACE,{"derivedFrom":subQ1,"instanceName":"60"}),makeQuery(id+"F6.opPattern","COPY",FACE,{"derivedFrom":subQ1,"instanceName":"61"}),makeQuery(id+"F6.opPattern","COPY",FACE,{"derivedFrom":subQ1,"instanceName":"62"}),makeQuery(id+"F6.opPattern","COPY",FACE,{"derivedFrom":subQ1,"instanceName":"63"}),makeQuery(id+"F6.opPattern","COPY",FACE,{"derivedFrom":subQ1,"instanceName":"64"}),makeQuery(id+"F6.opPattern","COPY",FACE,{"derivedFrom":subQ1,"instanceName":"65"}),makeQuery(id+"F6.opPattern","COPY",FACE,{"derivedFrom":subQ1,"instanceName":"66"}),makeQuery(id+"F6.opPattern","COPY",FACE,{"derivedFrom":subQ1,"instanceName":"67"}),makeQuery(id+"F6.opPattern","COPY",FACE,{"derivedFrom":subQ1,"instanceName":"68"}),makeQuery(id+"F6.opPattern","COPY",FACE,{"derivedFrom":subQ1,"instanceName":"69"}),makeQuery(id+"F6.opPattern","COPY",FACE,{"derivedFrom":subQ1,"instanceName":"70"}),makeQuery(id+"F6.opPattern","COPY",FACE,{"derivedFrom":subQ1,"instanceName":"71"}),makeQuery(id+"F6.opPattern","COPY",FACE,{"derivedFrom":subQ1,"instanceName":"72"}),makeQuery(id+"F6.opPattern","COPY",FACE,{"derivedFrom":subQ1,"instanceName":"73"}),makeQuery(id+"F6.opPattern","COPY",FACE,{"derivedFrom":subQ1,"instanceName":"74"}),makeQuery(id+"F6.opPattern","COPY",FACE,{"derivedFrom":subQ1,"instanceName":"75"}),makeQuery(id+"F6.opPattern","COPY",FACE,{"derivedFrom":subQ1,"instanceName":"76"}),makeQuery(id+"F6.opPattern","COPY",FACE,{"derivedFrom":subQ1,"instanceName":"77"}),makeQuery(id+"F6.opPattern","COPY",FACE,{"derivedFrom":subQ1,"instanceName":"78"})]})],"blendedInto":[makeQuery(id+"F6.boolean.opBoolean","MERGE",FACE,{"derivedFrom":[subQ1,makeQuery(id+"F6.opPattern","COPY",FACE,{"derivedFrom":subQ1,"instanceName":"1"}),makeQuery(id+"F6.opPattern","COPY",FACE,{"derivedFrom":subQ1,"instanceName":"2"}),makeQuery(id+"F6.opPattern","COPY",FACE,{"derivedFrom":subQ1,"instanceName":"3"}),makeQuery(id+"F6.opPattern","COPY",FACE,{"derivedFrom":subQ1,"instanceName":"4"}),makeQuery(id+"F6.opPattern","COPY",FACE,{"derivedFrom":subQ1,"instanceName":"5"}),makeQuery(id+"F6.opPattern","COPY",FACE,{"derivedFrom":subQ1,"instanceName":"6"}),makeQuery(id+"F6.opPattern","COPY",FACE,{"derivedFrom":subQ1,"instanceName":"7"}),makeQuery(id+"F6.opPattern","COPY",FACE,{"derivedFrom":subQ1,"instanceName":"8"}),makeQuery(id+"F6.opPattern","COPY",FACE,{"derivedFrom":subQ1,"instanceName":"9"}),makeQuery(id+"F6.opPattern","COPY",FACE,{"derivedFrom":subQ1,"instanceName":"10"}),makeQuery(id+"F6.opPattern","COPY",FACE,{"derivedFrom":subQ1,"instanceName":"11"}),makeQuery(id+"F6.opPattern","COPY",FACE,{"derivedFrom":subQ1,"instanceName":"12"}),makeQuery(id+"F6.opPattern","COPY",FACE,{"derivedFrom":subQ1,"instanceName":"13"}),makeQuery(id+"F6.opPattern","COPY",FACE,{"derivedFrom":subQ1,"instanceName":"14"}),makeQuery(id+"F6.opPattern","COPY",FACE,{"derivedFrom":subQ1,"instanceName":"15"}),makeQuery(id+"F6.opPattern","COPY",FACE,{"derivedFrom":subQ1,"instanceName":"16"}),makeQuery(id+"F6.opPattern","COPY",FACE,{"derivedFrom":subQ1,"instanceName":"17"}),makeQuery(id+"F6.opPattern","COPY",FACE,{"derivedFrom":subQ1,"instanceName":"18"}),makeQuery(id+"F6.opPattern","COPY",FACE,{"derivedFrom":subQ1,"instanceName":"19"}),makeQuery(id+"F6.opPattern","COPY",FACE,{"derivedFrom":subQ1,"instanceName":"20"}),makeQuery(id+"F6.opPattern","COPY",FACE,{"derivedFrom":subQ1,"instanceName":"21"}),makeQuery(id+"F6.opPattern","COPY",FACE,{"derivedFrom":subQ1,"instanceName":"22"}),makeQuery(id+"F6.opPattern","COPY",FACE,{"derivedFrom":subQ1,"instanceName":"23"}),makeQuery(id+"F6.opPattern","COPY",FACE,{"derivedFrom":subQ1,"instanceName":"24"}),makeQuery(id+"F6.opPattern","COPY",FACE,{"derivedFrom":subQ1,"instanceName":"25"}),makeQuery(id+"F6.opPattern","COPY",FACE,{"derivedFrom":subQ1,"instanceName":"26"}),makeQuery(id+"F6.opPattern","COPY",FACE,{"derivedFrom":subQ1,"instanceName":"27"}),makeQuery(id+"F6.opPattern","COPY",FACE,{"derivedFrom":subQ1,"instanceName":"28"}),makeQuery(id+"F6.opPattern","COPY",FACE,{"derivedFrom":subQ1,"instanceName":"29"}),makeQuery(id+"F6.opPattern","COPY",FACE,{"derivedFrom":subQ1,"instanceName":"30"}),makeQuery(id+"F6.opPattern","COPY",FACE,{"derivedFrom":subQ1,"instanceName":"31"}),makeQuery(id+"F6.opPattern","COPY",FACE,{"derivedFrom":subQ1,"instanceName":"32"}),makeQuery(id+"F6.opPattern","COPY",FACE,{"derivedFrom":subQ1,"instanceName":"33"}),makeQuery(id+"F6.opPattern","COPY",FACE,{"derivedFrom":subQ1,"instanceName":"34"}),makeQuery(id+"F6.opPattern","COPY",FACE,{"derivedFrom":subQ1,"instanceName":"35"}),makeQuery(id+"F6.opPattern","COPY",FACE,{"derivedFrom":subQ1,"instanceName":"36"}),makeQuery(id+"F6.opPattern","COPY",FACE,{"derivedFrom":subQ1,"instanceName":"37"}),makeQuery(id+"F6.opPattern","COPY",FACE,{"derivedFrom":subQ1,"instanceName":"38"}),makeQuery(id+"F6.opPattern","COPY",FACE,{"derivedFrom":subQ1,"instanceName":"39"}),makeQuery(id+"F6.opPattern","COPY",FACE,{"derivedFrom":subQ1,"instanceName":"40"}),makeQuery(id+"F6.opPattern","COPY",FACE,{"derivedFrom":subQ1,"instanceName":"41"}),makeQuery(id+"F6.opPattern","COPY",FACE,{"derivedFrom":subQ1,"instanceName":"42"}),makeQuery(id+"F6.opPattern","COPY",FACE,{"derivedFrom":subQ1,"instanceName":"43"}),makeQuery(id+"F6.opPattern","COPY",FACE,{"derivedFrom":subQ1,"instanceName":"44"}),makeQuery(id+"F6.opPattern","COPY",FACE,{"derivedFrom":subQ1,"instanceName":"45"}),makeQuery(id+"F6.opPattern","COPY",FACE,{"derivedFrom":subQ1,"instanceName":"46"}),makeQuery(id+"F6.opPattern","COPY",FACE,{"derivedFrom":subQ1,"instanceName":"47"}),makeQuery(id+"F6.opPattern","COPY",FACE,{"derivedFrom":subQ1,"instanceName":"48"}),makeQuery(id+"F6.opPattern","COPY",FACE,{"derivedFrom":subQ1,"instanceName":"49"}),makeQuery(id+"F6.opPattern","COPY",FACE,{"derivedFrom":subQ1,"instanceName":"50"}),makeQuery(id+"F6.opPattern","COPY",FACE,{"derivedFrom":subQ1,"instanceName":"51"}),makeQuery(id+"F6.opPattern","COPY",FACE,{"derivedFrom":subQ1,"instanceName":"52"}),makeQuery(id+"F6.opPattern","COPY",FACE,{"derivedFrom":subQ1,"instanceName":"53"}),makeQuery(id+"F6.opPattern","COPY",FACE,{"derivedFrom":subQ1,"instanceName":"54"}),makeQuery(id+"F6.opPattern","COPY",FACE,{"derivedFrom":subQ1,"instanceName":"55"}),makeQuery(id+"F6.opPattern","COPY",FACE,{"derivedFrom":subQ1,"instanceName":"56"}),makeQuery(id+"F6.opPattern","COPY",FACE,{"derivedFrom":subQ1,"instanceName":"57"}),makeQuery(id+"F6.opPattern","COPY",FACE,{"derivedFrom":subQ1,"instanceName":"58"}),makeQuery(id+"F6.opPattern","COPY",FACE,{"derivedFrom":subQ1,"instanceName":"59"}),makeQuery(id+"F6.opPattern","COPY",FACE,{"derivedFrom":subQ1,"instanceName":"60"}),makeQuery(id+"F6.opPattern","COPY",FACE,{"derivedFrom":subQ1,"instanceName":"61"}),makeQuery(id+"F6.opPattern","COPY",FACE,{"derivedFrom":subQ1,"instanceName":"62"}),makeQuery(id+"F6.opPattern","COPY",FACE,{"derivedFrom":subQ1,"instanceName":"63"}),makeQuery(id+"F6.opPattern","COPY",FACE,{"derivedFrom":subQ1,"instanceName":"64"}),makeQuery(id+"F6.opPattern","COPY",FACE,{"derivedFrom":subQ1,"instanceName":"65"}),makeQuery(id+"F6.opPattern","COPY",FACE,{"derivedFrom":subQ1,"instanceName":"66"}),makeQuery(id+"F6.opPattern","COPY",FACE,{"derivedFrom":subQ1,"instanceName":"67"}),makeQuery(id+"F6.opPattern","COPY",FACE,{"derivedFrom":subQ1,"instanceName":"68"}),makeQuery(id+"F6.opPattern","COPY",FACE,{"derivedFrom":subQ1,"instanceName":"69"}),makeQuery(id+"F6.opPattern","COPY",FACE,{"derivedFrom":subQ1,"instanceName":"70"}),makeQuery(id+"F6.opPattern","COPY",FACE,{"derivedFrom":subQ1,"instanceName":"71"}),makeQuery(id+"F6.opPattern","COPY",FACE,{"derivedFrom":subQ1,"instanceName":"72"}),makeQuery(id+"F6.opPattern","COPY",FACE,{"derivedFrom":subQ1,"instanceName":"73"}),makeQuery(id+"F6.opPattern","COPY",FACE,{"derivedFrom":subQ1,"instanceName":"74"}),makeQuery(id+"F6.opPattern","COPY",FACE,{"derivedFrom":subQ1,"instanceName":"75"}),makeQuery(id+"F6.opPattern","COPY",FACE,{"derivedFrom":subQ1,"instanceName":"76"}),makeQuery(id+"F6.opPattern","COPY",FACE,{"derivedFrom":subQ1,"instanceName":"77"}),makeQuery(id+"F6.opPattern","COPY",FACE,{"derivedFrom":subQ1,"instanceName":"78"})]})]});}
            var Q4;
            {var subQ0=sQuery(id+"F2.wireOp",EDGE,"E0");var subQ1=makeQuery(id+"F5.boolean.opBoolean","MERGE",FACE,{"derivedFrom":[makeQuery(id+"F4.opExtrude","CAP_FACE",FACE,{"disambiguationData":[OSD([subQ0])],"isStart":false}),makeQuery(id+"F5.opExtrude","CAP_FACE",FACE,{"disambiguationData":[OSD([subQ0,sQuery(id+"F2.wireOp",EDGE,"E1"),sQuery(id+"F2.wireOp",EDGE,"E2"),sQuery(id+"F2.wireOp",EDGE,"E3")])],"isStart":false})]});Q4=makeQuery(id+"F9.opChamfer","BLEND_EDGE",EDGE,{"blendedFrom":[makeQuery(id+"F8.boolean.opBoolean","COPY",EDGE,{"derivedFrom":makeQuery(id+"F8.opExtrude","CAP_EDGE",EDGE,{"disambiguationData":[OSD([sQuery(id+"F7.wireOp",EDGE,"E16.1.3.0")])],"isStart":true})}),makeQuery(id+"F6.boolean.opBoolean","MERGE",FACE,{"derivedFrom":[subQ1,makeQuery(id+"F6.opPattern","COPY",FACE,{"derivedFrom":subQ1,"instanceName":"1"}),makeQuery(id+"F6.opPattern","COPY",FACE,{"derivedFrom":subQ1,"instanceName":"2"}),makeQuery(id+"F6.opPattern","COPY",FACE,{"derivedFrom":subQ1,"instanceName":"3"}),makeQuery(id+"F6.opPattern","COPY",FACE,{"derivedFrom":subQ1,"instanceName":"4"}),makeQuery(id+"F6.opPattern","COPY",FACE,{"derivedFrom":subQ1,"instanceName":"5"}),makeQuery(id+"F6.opPattern","COPY",FACE,{"derivedFrom":subQ1,"instanceName":"6"}),makeQuery(id+"F6.opPattern","COPY",FACE,{"derivedFrom":subQ1,"instanceName":"7"}),makeQuery(id+"F6.opPattern","COPY",FACE,{"derivedFrom":subQ1,"instanceName":"8"}),makeQuery(id+"F6.opPattern","COPY",FACE,{"derivedFrom":subQ1,"instanceName":"9"}),makeQuery(id+"F6.opPattern","COPY",FACE,{"derivedFrom":subQ1,"instanceName":"10"}),makeQuery(id+"F6.opPattern","COPY",FACE,{"derivedFrom":subQ1,"instanceName":"11"}),makeQuery(id+"F6.opPattern","COPY",FACE,{"derivedFrom":subQ1,"instanceName":"12"}),makeQuery(id+"F6.opPattern","COPY",FACE,{"derivedFrom":subQ1,"instanceName":"13"}),makeQuery(id+"F6.opPattern","COPY",FACE,{"derivedFrom":subQ1,"instanceName":"14"}),makeQuery(id+"F6.opPattern","COPY",FACE,{"derivedFrom":subQ1,"instanceName":"15"}),makeQuery(id+"F6.opPattern","COPY",FACE,{"derivedFrom":subQ1,"instanceName":"16"}),makeQuery(id+"F6.opPattern","COPY",FACE,{"derivedFrom":subQ1,"instanceName":"17"}),makeQuery(id+"F6.opPattern","COPY",FACE,{"derivedFrom":subQ1,"instanceName":"18"}),makeQuery(id+"F6.opPattern","COPY",FACE,{"derivedFrom":subQ1,"instanceName":"19"}),makeQuery(id+"F6.opPattern","COPY",FACE,{"derivedFrom":subQ1,"instanceName":"20"}),makeQuery(id+"F6.opPattern","COPY",FACE,{"derivedFrom":subQ1,"instanceName":"21"}),makeQuery(id+"F6.opPattern","COPY",FACE,{"derivedFrom":subQ1,"instanceName":"22"}),makeQuery(id+"F6.opPattern","COPY",FACE,{"derivedFrom":subQ1,"instanceName":"23"}),makeQuery(id+"F6.opPattern","COPY",FACE,{"derivedFrom":subQ1,"instanceName":"24"}),makeQuery(id+"F6.opPattern","COPY",FACE,{"derivedFrom":subQ1,"instanceName":"25"}),makeQuery(id+"F6.opPattern","COPY",FACE,{"derivedFrom":subQ1,"instanceName":"26"}),makeQuery(id+"F6.opPattern","COPY",FACE,{"derivedFrom":subQ1,"instanceName":"27"}),makeQuery(id+"F6.opPattern","COPY",FACE,{"derivedFrom":subQ1,"instanceName":"28"}),makeQuery(id+"F6.opPattern","COPY",FACE,{"derivedFrom":subQ1,"instanceName":"29"}),makeQuery(id+"F6.opPattern","COPY",FACE,{"derivedFrom":subQ1,"instanceName":"30"}),makeQuery(id+"F6.opPattern","COPY",FACE,{"derivedFrom":subQ1,"instanceName":"31"}),makeQuery(id+"F6.opPattern","COPY",FACE,{"derivedFrom":subQ1,"instanceName":"32"}),makeQuery(id+"F6.opPattern","COPY",FACE,{"derivedFrom":subQ1,"instanceName":"33"}),makeQuery(id+"F6.opPattern","COPY",FACE,{"derivedFrom":subQ1,"instanceName":"34"}),makeQuery(id+"F6.opPattern","COPY",FACE,{"derivedFrom":subQ1,"instanceName":"35"}),makeQuery(id+"F6.opPattern","COPY",FACE,{"derivedFrom":subQ1,"instanceName":"36"}),makeQuery(id+"F6.opPattern","COPY",FACE,{"derivedFrom":subQ1,"instanceName":"37"}),makeQuery(id+"F6.opPattern","COPY",FACE,{"derivedFrom":subQ1,"instanceName":"38"}),makeQuery(id+"F6.opPattern","COPY",FACE,{"derivedFrom":subQ1,"instanceName":"39"}),makeQuery(id+"F6.opPattern","COPY",FACE,{"derivedFrom":subQ1,"instanceName":"40"}),makeQuery(id+"F6.opPattern","COPY",FACE,{"derivedFrom":subQ1,"instanceName":"41"}),makeQuery(id+"F6.opPattern","COPY",FACE,{"derivedFrom":subQ1,"instanceName":"42"}),makeQuery(id+"F6.opPattern","COPY",FACE,{"derivedFrom":subQ1,"instanceName":"43"}),makeQuery(id+"F6.opPattern","COPY",FACE,{"derivedFrom":subQ1,"instanceName":"44"}),makeQuery(id+"F6.opPattern","COPY",FACE,{"derivedFrom":subQ1,"instanceName":"45"}),makeQuery(id+"F6.opPattern","COPY",FACE,{"derivedFrom":subQ1,"instanceName":"46"}),makeQuery(id+"F6.opPattern","COPY",FACE,{"derivedFrom":subQ1,"instanceName":"47"}),makeQuery(id+"F6.opPattern","COPY",FACE,{"derivedFrom":subQ1,"instanceName":"48"}),makeQuery(id+"F6.opPattern","COPY",FACE,{"derivedFrom":subQ1,"instanceName":"49"}),makeQuery(id+"F6.opPattern","COPY",FACE,{"derivedFrom":subQ1,"instanceName":"50"}),makeQuery(id+"F6.opPattern","COPY",FACE,{"derivedFrom":subQ1,"instanceName":"51"}),makeQuery(id+"F6.opPattern","COPY",FACE,{"derivedFrom":subQ1,"instanceName":"52"}),makeQuery(id+"F6.opPattern","COPY",FACE,{"derivedFrom":subQ1,"instanceName":"53"}),makeQuery(id+"F6.opPattern","COPY",FACE,{"derivedFrom":subQ1,"instanceName":"54"}),makeQuery(id+"F6.opPattern","COPY",FACE,{"derivedFrom":subQ1,"instanceName":"55"}),makeQuery(id+"F6.opPattern","COPY",FACE,{"derivedFrom":subQ1,"instanceName":"56"}),makeQuery(id+"F6.opPattern","COPY",FACE,{"derivedFrom":subQ1,"instanceName":"57"}),makeQuery(id+"F6.opPattern","COPY",FACE,{"derivedFrom":subQ1,"instanceName":"58"}),makeQuery(id+"F6.opPattern","COPY",FACE,{"derivedFrom":subQ1,"instanceName":"59"}),makeQuery(id+"F6.opPattern","COPY",FACE,{"derivedFrom":subQ1,"instanceName":"60"}),makeQuery(id+"F6.opPattern","COPY",FACE,{"derivedFrom":subQ1,"instanceName":"61"}),makeQuery(id+"F6.opPattern","COPY",FACE,{"derivedFrom":subQ1,"instanceName":"62"}),makeQuery(id+"F6.opPattern","COPY",FACE,{"derivedFrom":subQ1,"instanceName":"63"}),makeQuery(id+"F6.opPattern","COPY",FACE,{"derivedFrom":subQ1,"instanceName":"64"}),makeQuery(id+"F6.opPattern","COPY",FACE,{"derivedFrom":subQ1,"instanceName":"65"}),makeQuery(id+"F6.opPattern","COPY",FACE,{"derivedFrom":subQ1,"instanceName":"66"}),makeQuery(id+"F6.opPattern","COPY",FACE,{"derivedFrom":subQ1,"instanceName":"67"}),makeQuery(id+"F6.opPattern","COPY",FACE,{"derivedFrom":subQ1,"instanceName":"68"}),makeQuery(id+"F6.opPattern","COPY",FACE,{"derivedFrom":subQ1,"instanceName":"69"}),makeQuery(id+"F6.opPattern","COPY",FACE,{"derivedFrom":subQ1,"instanceName":"70"}),makeQuery(id+"F6.opPattern","COPY",FACE,{"derivedFrom":subQ1,"instanceName":"71"}),makeQuery(id+"F6.opPattern","COPY",FACE,{"derivedFrom":subQ1,"instanceName":"72"}),makeQuery(id+"F6.opPattern","COPY",FACE,{"derivedFrom":subQ1,"instanceName":"73"}),makeQuery(id+"F6.opPattern","COPY",FACE,{"derivedFrom":subQ1,"instanceName":"74"}),makeQuery(id+"F6.opPattern","COPY",FACE,{"derivedFrom":subQ1,"instanceName":"75"}),makeQuery(id+"F6.opPattern","COPY",FACE,{"derivedFrom":subQ1,"instanceName":"76"}),makeQuery(id+"F6.opPattern","COPY",FACE,{"derivedFrom":subQ1,"instanceName":"77"}),makeQuery(id+"F6.opPattern","COPY",FACE,{"derivedFrom":subQ1,"instanceName":"78"})]})],"blendedInto":[makeQuery(id+"F6.boolean.opBoolean","MERGE",FACE,{"derivedFrom":[subQ1,makeQuery(id+"F6.opPattern","COPY",FACE,{"derivedFrom":subQ1,"instanceName":"1"}),makeQuery(id+"F6.opPattern","COPY",FACE,{"derivedFrom":subQ1,"instanceName":"2"}),makeQuery(id+"F6.opPattern","COPY",FACE,{"derivedFrom":subQ1,"instanceName":"3"}),makeQuery(id+"F6.opPattern","COPY",FACE,{"derivedFrom":subQ1,"instanceName":"4"}),makeQuery(id+"F6.opPattern","COPY",FACE,{"derivedFrom":subQ1,"instanceName":"5"}),makeQuery(id+"F6.opPattern","COPY",FACE,{"derivedFrom":subQ1,"instanceName":"6"}),makeQuery(id+"F6.opPattern","COPY",FACE,{"derivedFrom":subQ1,"instanceName":"7"}),makeQuery(id+"F6.opPattern","COPY",FACE,{"derivedFrom":subQ1,"instanceName":"8"}),makeQuery(id+"F6.opPattern","COPY",FACE,{"derivedFrom":subQ1,"instanceName":"9"}),makeQuery(id+"F6.opPattern","COPY",FACE,{"derivedFrom":subQ1,"instanceName":"10"}),makeQuery(id+"F6.opPattern","COPY",FACE,{"derivedFrom":subQ1,"instanceName":"11"}),makeQuery(id+"F6.opPattern","COPY",FACE,{"derivedFrom":subQ1,"instanceName":"12"}),makeQuery(id+"F6.opPattern","COPY",FACE,{"derivedFrom":subQ1,"instanceName":"13"}),makeQuery(id+"F6.opPattern","COPY",FACE,{"derivedFrom":subQ1,"instanceName":"14"}),makeQuery(id+"F6.opPattern","COPY",FACE,{"derivedFrom":subQ1,"instanceName":"15"}),makeQuery(id+"F6.opPattern","COPY",FACE,{"derivedFrom":subQ1,"instanceName":"16"}),makeQuery(id+"F6.opPattern","COPY",FACE,{"derivedFrom":subQ1,"instanceName":"17"}),makeQuery(id+"F6.opPattern","COPY",FACE,{"derivedFrom":subQ1,"instanceName":"18"}),makeQuery(id+"F6.opPattern","COPY",FACE,{"derivedFrom":subQ1,"instanceName":"19"}),makeQuery(id+"F6.opPattern","COPY",FACE,{"derivedFrom":subQ1,"instanceName":"20"}),makeQuery(id+"F6.opPattern","COPY",FACE,{"derivedFrom":subQ1,"instanceName":"21"}),makeQuery(id+"F6.opPattern","COPY",FACE,{"derivedFrom":subQ1,"instanceName":"22"}),makeQuery(id+"F6.opPattern","COPY",FACE,{"derivedFrom":subQ1,"instanceName":"23"}),makeQuery(id+"F6.opPattern","COPY",FACE,{"derivedFrom":subQ1,"instanceName":"24"}),makeQuery(id+"F6.opPattern","COPY",FACE,{"derivedFrom":subQ1,"instanceName":"25"}),makeQuery(id+"F6.opPattern","COPY",FACE,{"derivedFrom":subQ1,"instanceName":"26"}),makeQuery(id+"F6.opPattern","COPY",FACE,{"derivedFrom":subQ1,"instanceName":"27"}),makeQuery(id+"F6.opPattern","COPY",FACE,{"derivedFrom":subQ1,"instanceName":"28"}),makeQuery(id+"F6.opPattern","COPY",FACE,{"derivedFrom":subQ1,"instanceName":"29"}),makeQuery(id+"F6.opPattern","COPY",FACE,{"derivedFrom":subQ1,"instanceName":"30"}),makeQuery(id+"F6.opPattern","COPY",FACE,{"derivedFrom":subQ1,"instanceName":"31"}),makeQuery(id+"F6.opPattern","COPY",FACE,{"derivedFrom":subQ1,"instanceName":"32"}),makeQuery(id+"F6.opPattern","COPY",FACE,{"derivedFrom":subQ1,"instanceName":"33"}),makeQuery(id+"F6.opPattern","COPY",FACE,{"derivedFrom":subQ1,"instanceName":"34"}),makeQuery(id+"F6.opPattern","COPY",FACE,{"derivedFrom":subQ1,"instanceName":"35"}),makeQuery(id+"F6.opPattern","COPY",FACE,{"derivedFrom":subQ1,"instanceName":"36"}),makeQuery(id+"F6.opPattern","COPY",FACE,{"derivedFrom":subQ1,"instanceName":"37"}),makeQuery(id+"F6.opPattern","COPY",FACE,{"derivedFrom":subQ1,"instanceName":"38"}),makeQuery(id+"F6.opPattern","COPY",FACE,{"derivedFrom":subQ1,"instanceName":"39"}),makeQuery(id+"F6.opPattern","COPY",FACE,{"derivedFrom":subQ1,"instanceName":"40"}),makeQuery(id+"F6.opPattern","COPY",FACE,{"derivedFrom":subQ1,"instanceName":"41"}),makeQuery(id+"F6.opPattern","COPY",FACE,{"derivedFrom":subQ1,"instanceName":"42"}),makeQuery(id+"F6.opPattern","COPY",FACE,{"derivedFrom":subQ1,"instanceName":"43"}),makeQuery(id+"F6.opPattern","COPY",FACE,{"derivedFrom":subQ1,"instanceName":"44"}),makeQuery(id+"F6.opPattern","COPY",FACE,{"derivedFrom":subQ1,"instanceName":"45"}),makeQuery(id+"F6.opPattern","COPY",FACE,{"derivedFrom":subQ1,"instanceName":"46"}),makeQuery(id+"F6.opPattern","COPY",FACE,{"derivedFrom":subQ1,"instanceName":"47"}),makeQuery(id+"F6.opPattern","COPY",FACE,{"derivedFrom":subQ1,"instanceName":"48"}),makeQuery(id+"F6.opPattern","COPY",FACE,{"derivedFrom":subQ1,"instanceName":"49"}),makeQuery(id+"F6.opPattern","COPY",FACE,{"derivedFrom":subQ1,"instanceName":"50"}),makeQuery(id+"F6.opPattern","COPY",FACE,{"derivedFrom":subQ1,"instanceName":"51"}),makeQuery(id+"F6.opPattern","COPY",FACE,{"derivedFrom":subQ1,"instanceName":"52"}),makeQuery(id+"F6.opPattern","COPY",FACE,{"derivedFrom":subQ1,"instanceName":"53"}),makeQuery(id+"F6.opPattern","COPY",FACE,{"derivedFrom":subQ1,"instanceName":"54"}),makeQuery(id+"F6.opPattern","COPY",FACE,{"derivedFrom":subQ1,"instanceName":"55"}),makeQuery(id+"F6.opPattern","COPY",FACE,{"derivedFrom":subQ1,"instanceName":"56"}),makeQuery(id+"F6.opPattern","COPY",FACE,{"derivedFrom":subQ1,"instanceName":"57"}),makeQuery(id+"F6.opPattern","COPY",FACE,{"derivedFrom":subQ1,"instanceName":"58"}),makeQuery(id+"F6.opPattern","COPY",FACE,{"derivedFrom":subQ1,"instanceName":"59"}),makeQuery(id+"F6.opPattern","COPY",FACE,{"derivedFrom":subQ1,"instanceName":"60"}),makeQuery(id+"F6.opPattern","COPY",FACE,{"derivedFrom":subQ1,"instanceName":"61"}),makeQuery(id+"F6.opPattern","COPY",FACE,{"derivedFrom":subQ1,"instanceName":"62"}),makeQuery(id+"F6.opPattern","COPY",FACE,{"derivedFrom":subQ1,"instanceName":"63"}),makeQuery(id+"F6.opPattern","COPY",FACE,{"derivedFrom":subQ1,"instanceName":"64"}),makeQuery(id+"F6.opPattern","COPY",FACE,{"derivedFrom":subQ1,"instanceName":"65"}),makeQuery(id+"F6.opPattern","COPY",FACE,{"derivedFrom":subQ1,"instanceName":"66"}),makeQuery(id+"F6.opPattern","COPY",FACE,{"derivedFrom":subQ1,"instanceName":"67"}),makeQuery(id+"F6.opPattern","COPY",FACE,{"derivedFrom":subQ1,"instanceName":"68"}),makeQuery(id+"F6.opPattern","COPY",FACE,{"derivedFrom":subQ1,"instanceName":"69"}),makeQuery(id+"F6.opPattern","COPY",FACE,{"derivedFrom":subQ1,"instanceName":"70"}),makeQuery(id+"F6.opPattern","COPY",FACE,{"derivedFrom":subQ1,"instanceName":"71"}),makeQuery(id+"F6.opPattern","COPY",FACE,{"derivedFrom":subQ1,"instanceName":"72"}),makeQuery(id+"F6.opPattern","COPY",FACE,{"derivedFrom":subQ1,"instanceName":"73"}),makeQuery(id+"F6.opPattern","COPY",FACE,{"derivedFrom":subQ1,"instanceName":"74"}),makeQuery(id+"F6.opPattern","COPY",FACE,{"derivedFrom":subQ1,"instanceName":"75"}),makeQuery(id+"F6.opPattern","COPY",FACE,{"derivedFrom":subQ1,"instanceName":"76"}),makeQuery(id+"F6.opPattern","COPY",FACE,{"derivedFrom":subQ1,"instanceName":"77"}),makeQuery(id+"F6.opPattern","COPY",FACE,{"derivedFrom":subQ1,"instanceName":"78"})]})]});}
            var Q5;
            {var subQ0=sQuery(id+"F2.wireOp",EDGE,"E0");var subQ1=makeQuery(id+"F5.boolean.opBoolean","MERGE",FACE,{"derivedFrom":[makeQuery(id+"F4.opExtrude","CAP_FACE",FACE,{"disambiguationData":[OSD([subQ0])],"isStart":false}),makeQuery(id+"F5.opExtrude","CAP_FACE",FACE,{"disambiguationData":[OSD([subQ0,sQuery(id+"F2.wireOp",EDGE,"E1"),sQuery(id+"F2.wireOp",EDGE,"E2"),sQuery(id+"F2.wireOp",EDGE,"E3")])],"isStart":false})]});Q5=makeQuery(id+"F9.opChamfer","BLEND_EDGE",EDGE,{"blendedFrom":[makeQuery(id+"F8.boolean.opBoolean","COPY",EDGE,{"derivedFrom":makeQuery(id+"F8.opExtrude","CAP_EDGE",EDGE,{"disambiguationData":[OSD([sQuery(id+"F7.wireOp",EDGE,"E15.2.0")])],"isStart":true})}),makeQuery(id+"F6.boolean.opBoolean","MERGE",FACE,{"derivedFrom":[subQ1,makeQuery(id+"F6.opPattern","COPY",FACE,{"derivedFrom":subQ1,"instanceName":"1"}),makeQuery(id+"F6.opPattern","COPY",FACE,{"derivedFrom":subQ1,"instanceName":"2"}),makeQuery(id+"F6.opPattern","COPY",FACE,{"derivedFrom":subQ1,"instanceName":"3"}),makeQuery(id+"F6.opPattern","COPY",FACE,{"derivedFrom":subQ1,"instanceName":"4"}),makeQuery(id+"F6.opPattern","COPY",FACE,{"derivedFrom":subQ1,"instanceName":"5"}),makeQuery(id+"F6.opPattern","COPY",FACE,{"derivedFrom":subQ1,"instanceName":"6"}),makeQuery(id+"F6.opPattern","COPY",FACE,{"derivedFrom":subQ1,"instanceName":"7"}),makeQuery(id+"F6.opPattern","COPY",FACE,{"derivedFrom":subQ1,"instanceName":"8"}),makeQuery(id+"F6.opPattern","COPY",FACE,{"derivedFrom":subQ1,"instanceName":"9"}),makeQuery(id+"F6.opPattern","COPY",FACE,{"derivedFrom":subQ1,"instanceName":"10"}),makeQuery(id+"F6.opPattern","COPY",FACE,{"derivedFrom":subQ1,"instanceName":"11"}),makeQuery(id+"F6.opPattern","COPY",FACE,{"derivedFrom":subQ1,"instanceName":"12"}),makeQuery(id+"F6.opPattern","COPY",FACE,{"derivedFrom":subQ1,"instanceName":"13"}),makeQuery(id+"F6.opPattern","COPY",FACE,{"derivedFrom":subQ1,"instanceName":"14"}),makeQuery(id+"F6.opPattern","COPY",FACE,{"derivedFrom":subQ1,"instanceName":"15"}),makeQuery(id+"F6.opPattern","COPY",FACE,{"derivedFrom":subQ1,"instanceName":"16"}),makeQuery(id+"F6.opPattern","COPY",FACE,{"derivedFrom":subQ1,"instanceName":"17"}),makeQuery(id+"F6.opPattern","COPY",FACE,{"derivedFrom":subQ1,"instanceName":"18"}),makeQuery(id+"F6.opPattern","COPY",FACE,{"derivedFrom":subQ1,"instanceName":"19"}),makeQuery(id+"F6.opPattern","COPY",FACE,{"derivedFrom":subQ1,"instanceName":"20"}),makeQuery(id+"F6.opPattern","COPY",FACE,{"derivedFrom":subQ1,"instanceName":"21"}),makeQuery(id+"F6.opPattern","COPY",FACE,{"derivedFrom":subQ1,"instanceName":"22"}),makeQuery(id+"F6.opPattern","COPY",FACE,{"derivedFrom":subQ1,"instanceName":"23"}),makeQuery(id+"F6.opPattern","COPY",FACE,{"derivedFrom":subQ1,"instanceName":"24"}),makeQuery(id+"F6.opPattern","COPY",FACE,{"derivedFrom":subQ1,"instanceName":"25"}),makeQuery(id+"F6.opPattern","COPY",FACE,{"derivedFrom":subQ1,"instanceName":"26"}),makeQuery(id+"F6.opPattern","COPY",FACE,{"derivedFrom":subQ1,"instanceName":"27"}),makeQuery(id+"F6.opPattern","COPY",FACE,{"derivedFrom":subQ1,"instanceName":"28"}),makeQuery(id+"F6.opPattern","COPY",FACE,{"derivedFrom":subQ1,"instanceName":"29"}),makeQuery(id+"F6.opPattern","COPY",FACE,{"derivedFrom":subQ1,"instanceName":"30"}),makeQuery(id+"F6.opPattern","COPY",FACE,{"derivedFrom":subQ1,"instanceName":"31"}),makeQuery(id+"F6.opPattern","COPY",FACE,{"derivedFrom":subQ1,"instanceName":"32"}),makeQuery(id+"F6.opPattern","COPY",FACE,{"derivedFrom":subQ1,"instanceName":"33"}),makeQuery(id+"F6.opPattern","COPY",FACE,{"derivedFrom":subQ1,"instanceName":"34"}),makeQuery(id+"F6.opPattern","COPY",FACE,{"derivedFrom":subQ1,"instanceName":"35"}),makeQuery(id+"F6.opPattern","COPY",FACE,{"derivedFrom":subQ1,"instanceName":"36"}),makeQuery(id+"F6.opPattern","COPY",FACE,{"derivedFrom":subQ1,"instanceName":"37"}),makeQuery(id+"F6.opPattern","COPY",FACE,{"derivedFrom":subQ1,"instanceName":"38"}),makeQuery(id+"F6.opPattern","COPY",FACE,{"derivedFrom":subQ1,"instanceName":"39"}),makeQuery(id+"F6.opPattern","COPY",FACE,{"derivedFrom":subQ1,"instanceName":"40"}),makeQuery(id+"F6.opPattern","COPY",FACE,{"derivedFrom":subQ1,"instanceName":"41"}),makeQuery(id+"F6.opPattern","COPY",FACE,{"derivedFrom":subQ1,"instanceName":"42"}),makeQuery(id+"F6.opPattern","COPY",FACE,{"derivedFrom":subQ1,"instanceName":"43"}),makeQuery(id+"F6.opPattern","COPY",FACE,{"derivedFrom":subQ1,"instanceName":"44"}),makeQuery(id+"F6.opPattern","COPY",FACE,{"derivedFrom":subQ1,"instanceName":"45"}),makeQuery(id+"F6.opPattern","COPY",FACE,{"derivedFrom":subQ1,"instanceName":"46"}),makeQuery(id+"F6.opPattern","COPY",FACE,{"derivedFrom":subQ1,"instanceName":"47"}),makeQuery(id+"F6.opPattern","COPY",FACE,{"derivedFrom":subQ1,"instanceName":"48"}),makeQuery(id+"F6.opPattern","COPY",FACE,{"derivedFrom":subQ1,"instanceName":"49"}),makeQuery(id+"F6.opPattern","COPY",FACE,{"derivedFrom":subQ1,"instanceName":"50"}),makeQuery(id+"F6.opPattern","COPY",FACE,{"derivedFrom":subQ1,"instanceName":"51"}),makeQuery(id+"F6.opPattern","COPY",FACE,{"derivedFrom":subQ1,"instanceName":"52"}),makeQuery(id+"F6.opPattern","COPY",FACE,{"derivedFrom":subQ1,"instanceName":"53"}),makeQuery(id+"F6.opPattern","COPY",FACE,{"derivedFrom":subQ1,"instanceName":"54"}),makeQuery(id+"F6.opPattern","COPY",FACE,{"derivedFrom":subQ1,"instanceName":"55"}),makeQuery(id+"F6.opPattern","COPY",FACE,{"derivedFrom":subQ1,"instanceName":"56"}),makeQuery(id+"F6.opPattern","COPY",FACE,{"derivedFrom":subQ1,"instanceName":"57"}),makeQuery(id+"F6.opPattern","COPY",FACE,{"derivedFrom":subQ1,"instanceName":"58"}),makeQuery(id+"F6.opPattern","COPY",FACE,{"derivedFrom":subQ1,"instanceName":"59"}),makeQuery(id+"F6.opPattern","COPY",FACE,{"derivedFrom":subQ1,"instanceName":"60"}),makeQuery(id+"F6.opPattern","COPY",FACE,{"derivedFrom":subQ1,"instanceName":"61"}),makeQuery(id+"F6.opPattern","COPY",FACE,{"derivedFrom":subQ1,"instanceName":"62"}),makeQuery(id+"F6.opPattern","COPY",FACE,{"derivedFrom":subQ1,"instanceName":"63"}),makeQuery(id+"F6.opPattern","COPY",FACE,{"derivedFrom":subQ1,"instanceName":"64"}),makeQuery(id+"F6.opPattern","COPY",FACE,{"derivedFrom":subQ1,"instanceName":"65"}),makeQuery(id+"F6.opPattern","COPY",FACE,{"derivedFrom":subQ1,"instanceName":"66"}),makeQuery(id+"F6.opPattern","COPY",FACE,{"derivedFrom":subQ1,"instanceName":"67"}),makeQuery(id+"F6.opPattern","COPY",FACE,{"derivedFrom":subQ1,"instanceName":"68"}),makeQuery(id+"F6.opPattern","COPY",FACE,{"derivedFrom":subQ1,"instanceName":"69"}),makeQuery(id+"F6.opPattern","COPY",FACE,{"derivedFrom":subQ1,"instanceName":"70"}),makeQuery(id+"F6.opPattern","COPY",FACE,{"derivedFrom":subQ1,"instanceName":"71"}),makeQuery(id+"F6.opPattern","COPY",FACE,{"derivedFrom":subQ1,"instanceName":"72"}),makeQuery(id+"F6.opPattern","COPY",FACE,{"derivedFrom":subQ1,"instanceName":"73"}),makeQuery(id+"F6.opPattern","COPY",FACE,{"derivedFrom":subQ1,"instanceName":"74"}),makeQuery(id+"F6.opPattern","COPY",FACE,{"derivedFrom":subQ1,"instanceName":"75"}),makeQuery(id+"F6.opPattern","COPY",FACE,{"derivedFrom":subQ1,"instanceName":"76"}),makeQuery(id+"F6.opPattern","COPY",FACE,{"derivedFrom":subQ1,"instanceName":"77"}),makeQuery(id+"F6.opPattern","COPY",FACE,{"derivedFrom":subQ1,"instanceName":"78"})]})],"blendedInto":[makeQuery(id+"F6.boolean.opBoolean","MERGE",FACE,{"derivedFrom":[subQ1,makeQuery(id+"F6.opPattern","COPY",FACE,{"derivedFrom":subQ1,"instanceName":"1"}),makeQuery(id+"F6.opPattern","COPY",FACE,{"derivedFrom":subQ1,"instanceName":"2"}),makeQuery(id+"F6.opPattern","COPY",FACE,{"derivedFrom":subQ1,"instanceName":"3"}),makeQuery(id+"F6.opPattern","COPY",FACE,{"derivedFrom":subQ1,"instanceName":"4"}),makeQuery(id+"F6.opPattern","COPY",FACE,{"derivedFrom":subQ1,"instanceName":"5"}),makeQuery(id+"F6.opPattern","COPY",FACE,{"derivedFrom":subQ1,"instanceName":"6"}),makeQuery(id+"F6.opPattern","COPY",FACE,{"derivedFrom":subQ1,"instanceName":"7"}),makeQuery(id+"F6.opPattern","COPY",FACE,{"derivedFrom":subQ1,"instanceName":"8"}),makeQuery(id+"F6.opPattern","COPY",FACE,{"derivedFrom":subQ1,"instanceName":"9"}),makeQuery(id+"F6.opPattern","COPY",FACE,{"derivedFrom":subQ1,"instanceName":"10"}),makeQuery(id+"F6.opPattern","COPY",FACE,{"derivedFrom":subQ1,"instanceName":"11"}),makeQuery(id+"F6.opPattern","COPY",FACE,{"derivedFrom":subQ1,"instanceName":"12"}),makeQuery(id+"F6.opPattern","COPY",FACE,{"derivedFrom":subQ1,"instanceName":"13"}),makeQuery(id+"F6.opPattern","COPY",FACE,{"derivedFrom":subQ1,"instanceName":"14"}),makeQuery(id+"F6.opPattern","COPY",FACE,{"derivedFrom":subQ1,"instanceName":"15"}),makeQuery(id+"F6.opPattern","COPY",FACE,{"derivedFrom":subQ1,"instanceName":"16"}),makeQuery(id+"F6.opPattern","COPY",FACE,{"derivedFrom":subQ1,"instanceName":"17"}),makeQuery(id+"F6.opPattern","COPY",FACE,{"derivedFrom":subQ1,"instanceName":"18"}),makeQuery(id+"F6.opPattern","COPY",FACE,{"derivedFrom":subQ1,"instanceName":"19"}),makeQuery(id+"F6.opPattern","COPY",FACE,{"derivedFrom":subQ1,"instanceName":"20"}),makeQuery(id+"F6.opPattern","COPY",FACE,{"derivedFrom":subQ1,"instanceName":"21"}),makeQuery(id+"F6.opPattern","COPY",FACE,{"derivedFrom":subQ1,"instanceName":"22"}),makeQuery(id+"F6.opPattern","COPY",FACE,{"derivedFrom":subQ1,"instanceName":"23"}),makeQuery(id+"F6.opPattern","COPY",FACE,{"derivedFrom":subQ1,"instanceName":"24"}),makeQuery(id+"F6.opPattern","COPY",FACE,{"derivedFrom":subQ1,"instanceName":"25"}),makeQuery(id+"F6.opPattern","COPY",FACE,{"derivedFrom":subQ1,"instanceName":"26"}),makeQuery(id+"F6.opPattern","COPY",FACE,{"derivedFrom":subQ1,"instanceName":"27"}),makeQuery(id+"F6.opPattern","COPY",FACE,{"derivedFrom":subQ1,"instanceName":"28"}),makeQuery(id+"F6.opPattern","COPY",FACE,{"derivedFrom":subQ1,"instanceName":"29"}),makeQuery(id+"F6.opPattern","COPY",FACE,{"derivedFrom":subQ1,"instanceName":"30"}),makeQuery(id+"F6.opPattern","COPY",FACE,{"derivedFrom":subQ1,"instanceName":"31"}),makeQuery(id+"F6.opPattern","COPY",FACE,{"derivedFrom":subQ1,"instanceName":"32"}),makeQuery(id+"F6.opPattern","COPY",FACE,{"derivedFrom":subQ1,"instanceName":"33"}),makeQuery(id+"F6.opPattern","COPY",FACE,{"derivedFrom":subQ1,"instanceName":"34"}),makeQuery(id+"F6.opPattern","COPY",FACE,{"derivedFrom":subQ1,"instanceName":"35"}),makeQuery(id+"F6.opPattern","COPY",FACE,{"derivedFrom":subQ1,"instanceName":"36"}),makeQuery(id+"F6.opPattern","COPY",FACE,{"derivedFrom":subQ1,"instanceName":"37"}),makeQuery(id+"F6.opPattern","COPY",FACE,{"derivedFrom":subQ1,"instanceName":"38"}),makeQuery(id+"F6.opPattern","COPY",FACE,{"derivedFrom":subQ1,"instanceName":"39"}),makeQuery(id+"F6.opPattern","COPY",FACE,{"derivedFrom":subQ1,"instanceName":"40"}),makeQuery(id+"F6.opPattern","COPY",FACE,{"derivedFrom":subQ1,"instanceName":"41"}),makeQuery(id+"F6.opPattern","COPY",FACE,{"derivedFrom":subQ1,"instanceName":"42"}),makeQuery(id+"F6.opPattern","COPY",FACE,{"derivedFrom":subQ1,"instanceName":"43"}),makeQuery(id+"F6.opPattern","COPY",FACE,{"derivedFrom":subQ1,"instanceName":"44"}),makeQuery(id+"F6.opPattern","COPY",FACE,{"derivedFrom":subQ1,"instanceName":"45"}),makeQuery(id+"F6.opPattern","COPY",FACE,{"derivedFrom":subQ1,"instanceName":"46"}),makeQuery(id+"F6.opPattern","COPY",FACE,{"derivedFrom":subQ1,"instanceName":"47"}),makeQuery(id+"F6.opPattern","COPY",FACE,{"derivedFrom":subQ1,"instanceName":"48"}),makeQuery(id+"F6.opPattern","COPY",FACE,{"derivedFrom":subQ1,"instanceName":"49"}),makeQuery(id+"F6.opPattern","COPY",FACE,{"derivedFrom":subQ1,"instanceName":"50"}),makeQuery(id+"F6.opPattern","COPY",FACE,{"derivedFrom":subQ1,"instanceName":"51"}),makeQuery(id+"F6.opPattern","COPY",FACE,{"derivedFrom":subQ1,"instanceName":"52"}),makeQuery(id+"F6.opPattern","COPY",FACE,{"derivedFrom":subQ1,"instanceName":"53"}),makeQuery(id+"F6.opPattern","COPY",FACE,{"derivedFrom":subQ1,"instanceName":"54"}),makeQuery(id+"F6.opPattern","COPY",FACE,{"derivedFrom":subQ1,"instanceName":"55"}),makeQuery(id+"F6.opPattern","COPY",FACE,{"derivedFrom":subQ1,"instanceName":"56"}),makeQuery(id+"F6.opPattern","COPY",FACE,{"derivedFrom":subQ1,"instanceName":"57"}),makeQuery(id+"F6.opPattern","COPY",FACE,{"derivedFrom":subQ1,"instanceName":"58"}),makeQuery(id+"F6.opPattern","COPY",FACE,{"derivedFrom":subQ1,"instanceName":"59"}),makeQuery(id+"F6.opPattern","COPY",FACE,{"derivedFrom":subQ1,"instanceName":"60"}),makeQuery(id+"F6.opPattern","COPY",FACE,{"derivedFrom":subQ1,"instanceName":"61"}),makeQuery(id+"F6.opPattern","COPY",FACE,{"derivedFrom":subQ1,"instanceName":"62"}),makeQuery(id+"F6.opPattern","COPY",FACE,{"derivedFrom":subQ1,"instanceName":"63"}),makeQuery(id+"F6.opPattern","COPY",FACE,{"derivedFrom":subQ1,"instanceName":"64"}),makeQuery(id+"F6.opPattern","COPY",FACE,{"derivedFrom":subQ1,"instanceName":"65"}),makeQuery(id+"F6.opPattern","COPY",FACE,{"derivedFrom":subQ1,"instanceName":"66"}),makeQuery(id+"F6.opPattern","COPY",FACE,{"derivedFrom":subQ1,"instanceName":"67"}),makeQuery(id+"F6.opPattern","COPY",FACE,{"derivedFrom":subQ1,"instanceName":"68"}),makeQuery(id+"F6.opPattern","COPY",FACE,{"derivedFrom":subQ1,"instanceName":"69"}),makeQuery(id+"F6.opPattern","COPY",FACE,{"derivedFrom":subQ1,"instanceName":"70"}),makeQuery(id+"F6.opPattern","COPY",FACE,{"derivedFrom":subQ1,"instanceName":"71"}),makeQuery(id+"F6.opPattern","COPY",FACE,{"derivedFrom":subQ1,"instanceName":"72"}),makeQuery(id+"F6.opPattern","COPY",FACE,{"derivedFrom":subQ1,"instanceName":"73"}),makeQuery(id+"F6.opPattern","COPY",FACE,{"derivedFrom":subQ1,"instanceName":"74"}),makeQuery(id+"F6.opPattern","COPY",FACE,{"derivedFrom":subQ1,"instanceName":"75"}),makeQuery(id+"F6.opPattern","COPY",FACE,{"derivedFrom":subQ1,"instanceName":"76"}),makeQuery(id+"F6.opPattern","COPY",FACE,{"derivedFrom":subQ1,"instanceName":"77"}),makeQuery(id+"F6.opPattern","COPY",FACE,{"derivedFrom":subQ1,"instanceName":"78"})]})]});}
            var Q6;
            {var subQ0=sQuery(id+"F2.wireOp",EDGE,"E0");var subQ1=makeQuery(id+"F5.boolean.opBoolean","MERGE",FACE,{"derivedFrom":[makeQuery(id+"F4.opExtrude","CAP_FACE",FACE,{"disambiguationData":[OSD([subQ0])],"isStart":true}),makeQuery(id+"F5.opExtrude","CAP_FACE",FACE,{"disambiguationData":[OSD([subQ0,sQuery(id+"F2.wireOp",EDGE,"E1"),sQuery(id+"F2.wireOp",EDGE,"E2"),sQuery(id+"F2.wireOp",EDGE,"E3")])],"isStart":true})]});var subQ2=makeQuery(id+"F6.boolean.opBoolean","MERGE",FACE,{"derivedFrom":[subQ1,makeQuery(id+"F6.opPattern","COPY",FACE,{"derivedFrom":subQ1,"instanceName":"1"}),makeQuery(id+"F6.opPattern","COPY",FACE,{"derivedFrom":subQ1,"instanceName":"2"}),makeQuery(id+"F6.opPattern","COPY",FACE,{"derivedFrom":subQ1,"instanceName":"3"}),makeQuery(id+"F6.opPattern","COPY",FACE,{"derivedFrom":subQ1,"instanceName":"4"}),makeQuery(id+"F6.opPattern","COPY",FACE,{"derivedFrom":subQ1,"instanceName":"5"}),makeQuery(id+"F6.opPattern","COPY",FACE,{"derivedFrom":subQ1,"instanceName":"6"}),makeQuery(id+"F6.opPattern","COPY",FACE,{"derivedFrom":subQ1,"instanceName":"7"}),makeQuery(id+"F6.opPattern","COPY",FACE,{"derivedFrom":subQ1,"instanceName":"8"}),makeQuery(id+"F6.opPattern","COPY",FACE,{"derivedFrom":subQ1,"instanceName":"9"}),makeQuery(id+"F6.opPattern","COPY",FACE,{"derivedFrom":subQ1,"instanceName":"10"}),makeQuery(id+"F6.opPattern","COPY",FACE,{"derivedFrom":subQ1,"instanceName":"11"}),makeQuery(id+"F6.opPattern","COPY",FACE,{"derivedFrom":subQ1,"instanceName":"12"}),makeQuery(id+"F6.opPattern","COPY",FACE,{"derivedFrom":subQ1,"instanceName":"13"}),makeQuery(id+"F6.opPattern","COPY",FACE,{"derivedFrom":subQ1,"instanceName":"14"}),makeQuery(id+"F6.opPattern","COPY",FACE,{"derivedFrom":subQ1,"instanceName":"15"}),makeQuery(id+"F6.opPattern","COPY",FACE,{"derivedFrom":subQ1,"instanceName":"16"}),makeQuery(id+"F6.opPattern","COPY",FACE,{"derivedFrom":subQ1,"instanceName":"17"}),makeQuery(id+"F6.opPattern","COPY",FACE,{"derivedFrom":subQ1,"instanceName":"18"}),makeQuery(id+"F6.opPattern","COPY",FACE,{"derivedFrom":subQ1,"instanceName":"19"}),makeQuery(id+"F6.opPattern","COPY",FACE,{"derivedFrom":subQ1,"instanceName":"20"}),makeQuery(id+"F6.opPattern","COPY",FACE,{"derivedFrom":subQ1,"instanceName":"21"}),makeQuery(id+"F6.opPattern","COPY",FACE,{"derivedFrom":subQ1,"instanceName":"22"}),makeQuery(id+"F6.opPattern","COPY",FACE,{"derivedFrom":subQ1,"instanceName":"23"}),makeQuery(id+"F6.opPattern","COPY",FACE,{"derivedFrom":subQ1,"instanceName":"24"}),makeQuery(id+"F6.opPattern","COPY",FACE,{"derivedFrom":subQ1,"instanceName":"25"}),makeQuery(id+"F6.opPattern","COPY",FACE,{"derivedFrom":subQ1,"instanceName":"26"}),makeQuery(id+"F6.opPattern","COPY",FACE,{"derivedFrom":subQ1,"instanceName":"27"}),makeQuery(id+"F6.opPattern","COPY",FACE,{"derivedFrom":subQ1,"instanceName":"28"}),makeQuery(id+"F6.opPattern","COPY",FACE,{"derivedFrom":subQ1,"instanceName":"29"}),makeQuery(id+"F6.opPattern","COPY",FACE,{"derivedFrom":subQ1,"instanceName":"30"}),makeQuery(id+"F6.opPattern","COPY",FACE,{"derivedFrom":subQ1,"instanceName":"31"}),makeQuery(id+"F6.opPattern","COPY",FACE,{"derivedFrom":subQ1,"instanceName":"32"}),makeQuery(id+"F6.opPattern","COPY",FACE,{"derivedFrom":subQ1,"instanceName":"33"}),makeQuery(id+"F6.opPattern","COPY",FACE,{"derivedFrom":subQ1,"instanceName":"34"}),makeQuery(id+"F6.opPattern","COPY",FACE,{"derivedFrom":subQ1,"instanceName":"35"}),makeQuery(id+"F6.opPattern","COPY",FACE,{"derivedFrom":subQ1,"instanceName":"36"}),makeQuery(id+"F6.opPattern","COPY",FACE,{"derivedFrom":subQ1,"instanceName":"37"}),makeQuery(id+"F6.opPattern","COPY",FACE,{"derivedFrom":subQ1,"instanceName":"38"}),makeQuery(id+"F6.opPattern","COPY",FACE,{"derivedFrom":subQ1,"instanceName":"39"}),makeQuery(id+"F6.opPattern","COPY",FACE,{"derivedFrom":subQ1,"instanceName":"40"}),makeQuery(id+"F6.opPattern","COPY",FACE,{"derivedFrom":subQ1,"instanceName":"41"}),makeQuery(id+"F6.opPattern","COPY",FACE,{"derivedFrom":subQ1,"instanceName":"42"}),makeQuery(id+"F6.opPattern","COPY",FACE,{"derivedFrom":subQ1,"instanceName":"43"}),makeQuery(id+"F6.opPattern","COPY",FACE,{"derivedFrom":subQ1,"instanceName":"44"}),makeQuery(id+"F6.opPattern","COPY",FACE,{"derivedFrom":subQ1,"instanceName":"45"}),makeQuery(id+"F6.opPattern","COPY",FACE,{"derivedFrom":subQ1,"instanceName":"46"}),makeQuery(id+"F6.opPattern","COPY",FACE,{"derivedFrom":subQ1,"instanceName":"47"}),makeQuery(id+"F6.opPattern","COPY",FACE,{"derivedFrom":subQ1,"instanceName":"48"}),makeQuery(id+"F6.opPattern","COPY",FACE,{"derivedFrom":subQ1,"instanceName":"49"}),makeQuery(id+"F6.opPattern","COPY",FACE,{"derivedFrom":subQ1,"instanceName":"50"}),makeQuery(id+"F6.opPattern","COPY",FACE,{"derivedFrom":subQ1,"instanceName":"51"}),makeQuery(id+"F6.opPattern","COPY",FACE,{"derivedFrom":subQ1,"instanceName":"52"}),makeQuery(id+"F6.opPattern","COPY",FACE,{"derivedFrom":subQ1,"instanceName":"53"}),makeQuery(id+"F6.opPattern","COPY",FACE,{"derivedFrom":subQ1,"instanceName":"54"}),makeQuery(id+"F6.opPattern","COPY",FACE,{"derivedFrom":subQ1,"instanceName":"55"}),makeQuery(id+"F6.opPattern","COPY",FACE,{"derivedFrom":subQ1,"instanceName":"56"}),makeQuery(id+"F6.opPattern","COPY",FACE,{"derivedFrom":subQ1,"instanceName":"57"}),makeQuery(id+"F6.opPattern","COPY",FACE,{"derivedFrom":subQ1,"instanceName":"58"}),makeQuery(id+"F6.opPattern","COPY",FACE,{"derivedFrom":subQ1,"instanceName":"59"}),makeQuery(id+"F6.opPattern","COPY",FACE,{"derivedFrom":subQ1,"instanceName":"60"}),makeQuery(id+"F6.opPattern","COPY",FACE,{"derivedFrom":subQ1,"instanceName":"61"}),makeQuery(id+"F6.opPattern","COPY",FACE,{"derivedFrom":subQ1,"instanceName":"62"}),makeQuery(id+"F6.opPattern","COPY",FACE,{"derivedFrom":subQ1,"instanceName":"63"}),makeQuery(id+"F6.opPattern","COPY",FACE,{"derivedFrom":subQ1,"instanceName":"64"}),makeQuery(id+"F6.opPattern","COPY",FACE,{"derivedFrom":subQ1,"instanceName":"65"}),makeQuery(id+"F6.opPattern","COPY",FACE,{"derivedFrom":subQ1,"instanceName":"66"}),makeQuery(id+"F6.opPattern","COPY",FACE,{"derivedFrom":subQ1,"instanceName":"67"}),makeQuery(id+"F6.opPattern","COPY",FACE,{"derivedFrom":subQ1,"instanceName":"68"}),makeQuery(id+"F6.opPattern","COPY",FACE,{"derivedFrom":subQ1,"instanceName":"69"}),makeQuery(id+"F6.opPattern","COPY",FACE,{"derivedFrom":subQ1,"instanceName":"70"}),makeQuery(id+"F6.opPattern","COPY",FACE,{"derivedFrom":subQ1,"instanceName":"71"}),makeQuery(id+"F6.opPattern","COPY",FACE,{"derivedFrom":subQ1,"instanceName":"72"}),makeQuery(id+"F6.opPattern","COPY",FACE,{"derivedFrom":subQ1,"instanceName":"73"}),makeQuery(id+"F6.opPattern","COPY",FACE,{"derivedFrom":subQ1,"instanceName":"74"}),makeQuery(id+"F6.opPattern","COPY",FACE,{"derivedFrom":subQ1,"instanceName":"75"}),makeQuery(id+"F6.opPattern","COPY",FACE,{"derivedFrom":subQ1,"instanceName":"76"}),makeQuery(id+"F6.opPattern","COPY",FACE,{"derivedFrom":subQ1,"instanceName":"77"}),makeQuery(id+"F6.opPattern","COPY",FACE,{"derivedFrom":subQ1,"instanceName":"78"})]});Q6=makeQuery(id+"F9.opChamfer","BLEND_EDGE",EDGE,{"blendedFrom":[makeQuery(id+"F8.boolean.opBoolean","INTERSECT",EDGE,{"derivedFrom":[subQ2,makeQuery(id+"F8.opExtrude","SWEPT_FACE",FACE,{"disambiguationData":[OSD([sQuery(id+"F7.wireOp",EDGE,"E14")])]})]}),subQ2],"blendedInto":[subQ2]});}
            var Q7;
            {var subQ0=sQuery(id+"F2.wireOp",EDGE,"E0");var subQ1=makeQuery(id+"F5.boolean.opBoolean","MERGE",FACE,{"derivedFrom":[makeQuery(id+"F4.opExtrude","CAP_FACE",FACE,{"disambiguationData":[OSD([subQ0])],"isStart":true}),makeQuery(id+"F5.opExtrude","CAP_FACE",FACE,{"disambiguationData":[OSD([subQ0,sQuery(id+"F2.wireOp",EDGE,"E1"),sQuery(id+"F2.wireOp",EDGE,"E2"),sQuery(id+"F2.wireOp",EDGE,"E3")])],"isStart":true})]});var subQ2=makeQuery(id+"F6.boolean.opBoolean","MERGE",FACE,{"derivedFrom":[subQ1,makeQuery(id+"F6.opPattern","COPY",FACE,{"derivedFrom":subQ1,"instanceName":"1"}),makeQuery(id+"F6.opPattern","COPY",FACE,{"derivedFrom":subQ1,"instanceName":"2"}),makeQuery(id+"F6.opPattern","COPY",FACE,{"derivedFrom":subQ1,"instanceName":"3"}),makeQuery(id+"F6.opPattern","COPY",FACE,{"derivedFrom":subQ1,"instanceName":"4"}),makeQuery(id+"F6.opPattern","COPY",FACE,{"derivedFrom":subQ1,"instanceName":"5"}),makeQuery(id+"F6.opPattern","COPY",FACE,{"derivedFrom":subQ1,"instanceName":"6"}),makeQuery(id+"F6.opPattern","COPY",FACE,{"derivedFrom":subQ1,"instanceName":"7"}),makeQuery(id+"F6.opPattern","COPY",FACE,{"derivedFrom":subQ1,"instanceName":"8"}),makeQuery(id+"F6.opPattern","COPY",FACE,{"derivedFrom":subQ1,"instanceName":"9"}),makeQuery(id+"F6.opPattern","COPY",FACE,{"derivedFrom":subQ1,"instanceName":"10"}),makeQuery(id+"F6.opPattern","COPY",FACE,{"derivedFrom":subQ1,"instanceName":"11"}),makeQuery(id+"F6.opPattern","COPY",FACE,{"derivedFrom":subQ1,"instanceName":"12"}),makeQuery(id+"F6.opPattern","COPY",FACE,{"derivedFrom":subQ1,"instanceName":"13"}),makeQuery(id+"F6.opPattern","COPY",FACE,{"derivedFrom":subQ1,"instanceName":"14"}),makeQuery(id+"F6.opPattern","COPY",FACE,{"derivedFrom":subQ1,"instanceName":"15"}),makeQuery(id+"F6.opPattern","COPY",FACE,{"derivedFrom":subQ1,"instanceName":"16"}),makeQuery(id+"F6.opPattern","COPY",FACE,{"derivedFrom":subQ1,"instanceName":"17"}),makeQuery(id+"F6.opPattern","COPY",FACE,{"derivedFrom":subQ1,"instanceName":"18"}),makeQuery(id+"F6.opPattern","COPY",FACE,{"derivedFrom":subQ1,"instanceName":"19"}),makeQuery(id+"F6.opPattern","COPY",FACE,{"derivedFrom":subQ1,"instanceName":"20"}),makeQuery(id+"F6.opPattern","COPY",FACE,{"derivedFrom":subQ1,"instanceName":"21"}),makeQuery(id+"F6.opPattern","COPY",FACE,{"derivedFrom":subQ1,"instanceName":"22"}),makeQuery(id+"F6.opPattern","COPY",FACE,{"derivedFrom":subQ1,"instanceName":"23"}),makeQuery(id+"F6.opPattern","COPY",FACE,{"derivedFrom":subQ1,"instanceName":"24"}),makeQuery(id+"F6.opPattern","COPY",FACE,{"derivedFrom":subQ1,"instanceName":"25"}),makeQuery(id+"F6.opPattern","COPY",FACE,{"derivedFrom":subQ1,"instanceName":"26"}),makeQuery(id+"F6.opPattern","COPY",FACE,{"derivedFrom":subQ1,"instanceName":"27"}),makeQuery(id+"F6.opPattern","COPY",FACE,{"derivedFrom":subQ1,"instanceName":"28"}),makeQuery(id+"F6.opPattern","COPY",FACE,{"derivedFrom":subQ1,"instanceName":"29"}),makeQuery(id+"F6.opPattern","COPY",FACE,{"derivedFrom":subQ1,"instanceName":"30"}),makeQuery(id+"F6.opPattern","COPY",FACE,{"derivedFrom":subQ1,"instanceName":"31"}),makeQuery(id+"F6.opPattern","COPY",FACE,{"derivedFrom":subQ1,"instanceName":"32"}),makeQuery(id+"F6.opPattern","COPY",FACE,{"derivedFrom":subQ1,"instanceName":"33"}),makeQuery(id+"F6.opPattern","COPY",FACE,{"derivedFrom":subQ1,"instanceName":"34"}),makeQuery(id+"F6.opPattern","COPY",FACE,{"derivedFrom":subQ1,"instanceName":"35"}),makeQuery(id+"F6.opPattern","COPY",FACE,{"derivedFrom":subQ1,"instanceName":"36"}),makeQuery(id+"F6.opPattern","COPY",FACE,{"derivedFrom":subQ1,"instanceName":"37"}),makeQuery(id+"F6.opPattern","COPY",FACE,{"derivedFrom":subQ1,"instanceName":"38"}),makeQuery(id+"F6.opPattern","COPY",FACE,{"derivedFrom":subQ1,"instanceName":"39"}),makeQuery(id+"F6.opPattern","COPY",FACE,{"derivedFrom":subQ1,"instanceName":"40"}),makeQuery(id+"F6.opPattern","COPY",FACE,{"derivedFrom":subQ1,"instanceName":"41"}),makeQuery(id+"F6.opPattern","COPY",FACE,{"derivedFrom":subQ1,"instanceName":"42"}),makeQuery(id+"F6.opPattern","COPY",FACE,{"derivedFrom":subQ1,"instanceName":"43"}),makeQuery(id+"F6.opPattern","COPY",FACE,{"derivedFrom":subQ1,"instanceName":"44"}),makeQuery(id+"F6.opPattern","COPY",FACE,{"derivedFrom":subQ1,"instanceName":"45"}),makeQuery(id+"F6.opPattern","COPY",FACE,{"derivedFrom":subQ1,"instanceName":"46"}),makeQuery(id+"F6.opPattern","COPY",FACE,{"derivedFrom":subQ1,"instanceName":"47"}),makeQuery(id+"F6.opPattern","COPY",FACE,{"derivedFrom":subQ1,"instanceName":"48"}),makeQuery(id+"F6.opPattern","COPY",FACE,{"derivedFrom":subQ1,"instanceName":"49"}),makeQuery(id+"F6.opPattern","COPY",FACE,{"derivedFrom":subQ1,"instanceName":"50"}),makeQuery(id+"F6.opPattern","COPY",FACE,{"derivedFrom":subQ1,"instanceName":"51"}),makeQuery(id+"F6.opPattern","COPY",FACE,{"derivedFrom":subQ1,"instanceName":"52"}),makeQuery(id+"F6.opPattern","COPY",FACE,{"derivedFrom":subQ1,"instanceName":"53"}),makeQuery(id+"F6.opPattern","COPY",FACE,{"derivedFrom":subQ1,"instanceName":"54"}),makeQuery(id+"F6.opPattern","COPY",FACE,{"derivedFrom":subQ1,"instanceName":"55"}),makeQuery(id+"F6.opPattern","COPY",FACE,{"derivedFrom":subQ1,"instanceName":"56"}),makeQuery(id+"F6.opPattern","COPY",FACE,{"derivedFrom":subQ1,"instanceName":"57"}),makeQuery(id+"F6.opPattern","COPY",FACE,{"derivedFrom":subQ1,"instanceName":"58"}),makeQuery(id+"F6.opPattern","COPY",FACE,{"derivedFrom":subQ1,"instanceName":"59"}),makeQuery(id+"F6.opPattern","COPY",FACE,{"derivedFrom":subQ1,"instanceName":"60"}),makeQuery(id+"F6.opPattern","COPY",FACE,{"derivedFrom":subQ1,"instanceName":"61"}),makeQuery(id+"F6.opPattern","COPY",FACE,{"derivedFrom":subQ1,"instanceName":"62"}),makeQuery(id+"F6.opPattern","COPY",FACE,{"derivedFrom":subQ1,"instanceName":"63"}),makeQuery(id+"F6.opPattern","COPY",FACE,{"derivedFrom":subQ1,"instanceName":"64"}),makeQuery(id+"F6.opPattern","COPY",FACE,{"derivedFrom":subQ1,"instanceName":"65"}),makeQuery(id+"F6.opPattern","COPY",FACE,{"derivedFrom":subQ1,"instanceName":"66"}),makeQuery(id+"F6.opPattern","COPY",FACE,{"derivedFrom":subQ1,"instanceName":"67"}),makeQuery(id+"F6.opPattern","COPY",FACE,{"derivedFrom":subQ1,"instanceName":"68"}),makeQuery(id+"F6.opPattern","COPY",FACE,{"derivedFrom":subQ1,"instanceName":"69"}),makeQuery(id+"F6.opPattern","COPY",FACE,{"derivedFrom":subQ1,"instanceName":"70"}),makeQuery(id+"F6.opPattern","COPY",FACE,{"derivedFrom":subQ1,"instanceName":"71"}),makeQuery(id+"F6.opPattern","COPY",FACE,{"derivedFrom":subQ1,"instanceName":"72"}),makeQuery(id+"F6.opPattern","COPY",FACE,{"derivedFrom":subQ1,"instanceName":"73"}),makeQuery(id+"F6.opPattern","COPY",FACE,{"derivedFrom":subQ1,"instanceName":"74"}),makeQuery(id+"F6.opPattern","COPY",FACE,{"derivedFrom":subQ1,"instanceName":"75"}),makeQuery(id+"F6.opPattern","COPY",FACE,{"derivedFrom":subQ1,"instanceName":"76"}),makeQuery(id+"F6.opPattern","COPY",FACE,{"derivedFrom":subQ1,"instanceName":"77"}),makeQuery(id+"F6.opPattern","COPY",FACE,{"derivedFrom":subQ1,"instanceName":"78"})]});Q7=makeQuery(id+"F9.opChamfer","BLEND_EDGE",EDGE,{"blendedFrom":[makeQuery(id+"F8.boolean.opBoolean","INTERSECT",EDGE,{"derivedFrom":[subQ2,makeQuery(id+"F8.opExtrude","SWEPT_FACE",FACE,{"disambiguationData":[OSD([sQuery(id+"F7.wireOp",EDGE,"E15.1.0")])]})]}),subQ2],"blendedInto":[subQ2]});}
            var Q8;
            {var subQ0=sQuery(id+"F2.wireOp",EDGE,"E0");var subQ1=makeQuery(id+"F5.boolean.opBoolean","MERGE",FACE,{"derivedFrom":[makeQuery(id+"F4.opExtrude","CAP_FACE",FACE,{"disambiguationData":[OSD([subQ0])],"isStart":true}),makeQuery(id+"F5.opExtrude","CAP_FACE",FACE,{"disambiguationData":[OSD([subQ0,sQuery(id+"F2.wireOp",EDGE,"E1"),sQuery(id+"F2.wireOp",EDGE,"E2"),sQuery(id+"F2.wireOp",EDGE,"E3")])],"isStart":true})]});var subQ2=makeQuery(id+"F6.boolean.opBoolean","MERGE",FACE,{"derivedFrom":[subQ1,makeQuery(id+"F6.opPattern","COPY",FACE,{"derivedFrom":subQ1,"instanceName":"1"}),makeQuery(id+"F6.opPattern","COPY",FACE,{"derivedFrom":subQ1,"instanceName":"2"}),makeQuery(id+"F6.opPattern","COPY",FACE,{"derivedFrom":subQ1,"instanceName":"3"}),makeQuery(id+"F6.opPattern","COPY",FACE,{"derivedFrom":subQ1,"instanceName":"4"}),makeQuery(id+"F6.opPattern","COPY",FACE,{"derivedFrom":subQ1,"instanceName":"5"}),makeQuery(id+"F6.opPattern","COPY",FACE,{"derivedFrom":subQ1,"instanceName":"6"}),makeQuery(id+"F6.opPattern","COPY",FACE,{"derivedFrom":subQ1,"instanceName":"7"}),makeQuery(id+"F6.opPattern","COPY",FACE,{"derivedFrom":subQ1,"instanceName":"8"}),makeQuery(id+"F6.opPattern","COPY",FACE,{"derivedFrom":subQ1,"instanceName":"9"}),makeQuery(id+"F6.opPattern","COPY",FACE,{"derivedFrom":subQ1,"instanceName":"10"}),makeQuery(id+"F6.opPattern","COPY",FACE,{"derivedFrom":subQ1,"instanceName":"11"}),makeQuery(id+"F6.opPattern","COPY",FACE,{"derivedFrom":subQ1,"instanceName":"12"}),makeQuery(id+"F6.opPattern","COPY",FACE,{"derivedFrom":subQ1,"instanceName":"13"}),makeQuery(id+"F6.opPattern","COPY",FACE,{"derivedFrom":subQ1,"instanceName":"14"}),makeQuery(id+"F6.opPattern","COPY",FACE,{"derivedFrom":subQ1,"instanceName":"15"}),makeQuery(id+"F6.opPattern","COPY",FACE,{"derivedFrom":subQ1,"instanceName":"16"}),makeQuery(id+"F6.opPattern","COPY",FACE,{"derivedFrom":subQ1,"instanceName":"17"}),makeQuery(id+"F6.opPattern","COPY",FACE,{"derivedFrom":subQ1,"instanceName":"18"}),makeQuery(id+"F6.opPattern","COPY",FACE,{"derivedFrom":subQ1,"instanceName":"19"}),makeQuery(id+"F6.opPattern","COPY",FACE,{"derivedFrom":subQ1,"instanceName":"20"}),makeQuery(id+"F6.opPattern","COPY",FACE,{"derivedFrom":subQ1,"instanceName":"21"}),makeQuery(id+"F6.opPattern","COPY",FACE,{"derivedFrom":subQ1,"instanceName":"22"}),makeQuery(id+"F6.opPattern","COPY",FACE,{"derivedFrom":subQ1,"instanceName":"23"}),makeQuery(id+"F6.opPattern","COPY",FACE,{"derivedFrom":subQ1,"instanceName":"24"}),makeQuery(id+"F6.opPattern","COPY",FACE,{"derivedFrom":subQ1,"instanceName":"25"}),makeQuery(id+"F6.opPattern","COPY",FACE,{"derivedFrom":subQ1,"instanceName":"26"}),makeQuery(id+"F6.opPattern","COPY",FACE,{"derivedFrom":subQ1,"instanceName":"27"}),makeQuery(id+"F6.opPattern","COPY",FACE,{"derivedFrom":subQ1,"instanceName":"28"}),makeQuery(id+"F6.opPattern","COPY",FACE,{"derivedFrom":subQ1,"instanceName":"29"}),makeQuery(id+"F6.opPattern","COPY",FACE,{"derivedFrom":subQ1,"instanceName":"30"}),makeQuery(id+"F6.opPattern","COPY",FACE,{"derivedFrom":subQ1,"instanceName":"31"}),makeQuery(id+"F6.opPattern","COPY",FACE,{"derivedFrom":subQ1,"instanceName":"32"}),makeQuery(id+"F6.opPattern","COPY",FACE,{"derivedFrom":subQ1,"instanceName":"33"}),makeQuery(id+"F6.opPattern","COPY",FACE,{"derivedFrom":subQ1,"instanceName":"34"}),makeQuery(id+"F6.opPattern","COPY",FACE,{"derivedFrom":subQ1,"instanceName":"35"}),makeQuery(id+"F6.opPattern","COPY",FACE,{"derivedFrom":subQ1,"instanceName":"36"}),makeQuery(id+"F6.opPattern","COPY",FACE,{"derivedFrom":subQ1,"instanceName":"37"}),makeQuery(id+"F6.opPattern","COPY",FACE,{"derivedFrom":subQ1,"instanceName":"38"}),makeQuery(id+"F6.opPattern","COPY",FACE,{"derivedFrom":subQ1,"instanceName":"39"}),makeQuery(id+"F6.opPattern","COPY",FACE,{"derivedFrom":subQ1,"instanceName":"40"}),makeQuery(id+"F6.opPattern","COPY",FACE,{"derivedFrom":subQ1,"instanceName":"41"}),makeQuery(id+"F6.opPattern","COPY",FACE,{"derivedFrom":subQ1,"instanceName":"42"}),makeQuery(id+"F6.opPattern","COPY",FACE,{"derivedFrom":subQ1,"instanceName":"43"}),makeQuery(id+"F6.opPattern","COPY",FACE,{"derivedFrom":subQ1,"instanceName":"44"}),makeQuery(id+"F6.opPattern","COPY",FACE,{"derivedFrom":subQ1,"instanceName":"45"}),makeQuery(id+"F6.opPattern","COPY",FACE,{"derivedFrom":subQ1,"instanceName":"46"}),makeQuery(id+"F6.opPattern","COPY",FACE,{"derivedFrom":subQ1,"instanceName":"47"}),makeQuery(id+"F6.opPattern","COPY",FACE,{"derivedFrom":subQ1,"instanceName":"48"}),makeQuery(id+"F6.opPattern","COPY",FACE,{"derivedFrom":subQ1,"instanceName":"49"}),makeQuery(id+"F6.opPattern","COPY",FACE,{"derivedFrom":subQ1,"instanceName":"50"}),makeQuery(id+"F6.opPattern","COPY",FACE,{"derivedFrom":subQ1,"instanceName":"51"}),makeQuery(id+"F6.opPattern","COPY",FACE,{"derivedFrom":subQ1,"instanceName":"52"}),makeQuery(id+"F6.opPattern","COPY",FACE,{"derivedFrom":subQ1,"instanceName":"53"}),makeQuery(id+"F6.opPattern","COPY",FACE,{"derivedFrom":subQ1,"instanceName":"54"}),makeQuery(id+"F6.opPattern","COPY",FACE,{"derivedFrom":subQ1,"instanceName":"55"}),makeQuery(id+"F6.opPattern","COPY",FACE,{"derivedFrom":subQ1,"instanceName":"56"}),makeQuery(id+"F6.opPattern","COPY",FACE,{"derivedFrom":subQ1,"instanceName":"57"}),makeQuery(id+"F6.opPattern","COPY",FACE,{"derivedFrom":subQ1,"instanceName":"58"}),makeQuery(id+"F6.opPattern","COPY",FACE,{"derivedFrom":subQ1,"instanceName":"59"}),makeQuery(id+"F6.opPattern","COPY",FACE,{"derivedFrom":subQ1,"instanceName":"60"}),makeQuery(id+"F6.opPattern","COPY",FACE,{"derivedFrom":subQ1,"instanceName":"61"}),makeQuery(id+"F6.opPattern","COPY",FACE,{"derivedFrom":subQ1,"instanceName":"62"}),makeQuery(id+"F6.opPattern","COPY",FACE,{"derivedFrom":subQ1,"instanceName":"63"}),makeQuery(id+"F6.opPattern","COPY",FACE,{"derivedFrom":subQ1,"instanceName":"64"}),makeQuery(id+"F6.opPattern","COPY",FACE,{"derivedFrom":subQ1,"instanceName":"65"}),makeQuery(id+"F6.opPattern","COPY",FACE,{"derivedFrom":subQ1,"instanceName":"66"}),makeQuery(id+"F6.opPattern","COPY",FACE,{"derivedFrom":subQ1,"instanceName":"67"}),makeQuery(id+"F6.opPattern","COPY",FACE,{"derivedFrom":subQ1,"instanceName":"68"}),makeQuery(id+"F6.opPattern","COPY",FACE,{"derivedFrom":subQ1,"instanceName":"69"}),makeQuery(id+"F6.opPattern","COPY",FACE,{"derivedFrom":subQ1,"instanceName":"70"}),makeQuery(id+"F6.opPattern","COPY",FACE,{"derivedFrom":subQ1,"instanceName":"71"}),makeQuery(id+"F6.opPattern","COPY",FACE,{"derivedFrom":subQ1,"instanceName":"72"}),makeQuery(id+"F6.opPattern","COPY",FACE,{"derivedFrom":subQ1,"instanceName":"73"}),makeQuery(id+"F6.opPattern","COPY",FACE,{"derivedFrom":subQ1,"instanceName":"74"}),makeQuery(id+"F6.opPattern","COPY",FACE,{"derivedFrom":subQ1,"instanceName":"75"}),makeQuery(id+"F6.opPattern","COPY",FACE,{"derivedFrom":subQ1,"instanceName":"76"}),makeQuery(id+"F6.opPattern","COPY",FACE,{"derivedFrom":subQ1,"instanceName":"77"}),makeQuery(id+"F6.opPattern","COPY",FACE,{"derivedFrom":subQ1,"instanceName":"78"})]});Q8=makeQuery(id+"F9.opChamfer","BLEND_EDGE",EDGE,{"blendedFrom":[makeQuery(id+"F8.boolean.opBoolean","INTERSECT",EDGE,{"derivedFrom":[subQ2,makeQuery(id+"F8.opExtrude","SWEPT_FACE",FACE,{"disambiguationData":[OSD([sQuery(id+"F7.wireOp",EDGE,"E15.2.0")])]})]}),subQ2],"blendedInto":[subQ2]});}
            var Q9;
            {var subQ0=sQuery(id+"F2.wireOp",EDGE,"E0");var subQ1=makeQuery(id+"F5.boolean.opBoolean","MERGE",FACE,{"derivedFrom":[makeQuery(id+"F4.opExtrude","CAP_FACE",FACE,{"disambiguationData":[OSD([subQ0])],"isStart":true}),makeQuery(id+"F5.opExtrude","CAP_FACE",FACE,{"disambiguationData":[OSD([subQ0,sQuery(id+"F2.wireOp",EDGE,"E1"),sQuery(id+"F2.wireOp",EDGE,"E2"),sQuery(id+"F2.wireOp",EDGE,"E3")])],"isStart":true})]});var subQ2=makeQuery(id+"F6.boolean.opBoolean","MERGE",FACE,{"derivedFrom":[subQ1,makeQuery(id+"F6.opPattern","COPY",FACE,{"derivedFrom":subQ1,"instanceName":"1"}),makeQuery(id+"F6.opPattern","COPY",FACE,{"derivedFrom":subQ1,"instanceName":"2"}),makeQuery(id+"F6.opPattern","COPY",FACE,{"derivedFrom":subQ1,"instanceName":"3"}),makeQuery(id+"F6.opPattern","COPY",FACE,{"derivedFrom":subQ1,"instanceName":"4"}),makeQuery(id+"F6.opPattern","COPY",FACE,{"derivedFrom":subQ1,"instanceName":"5"}),makeQuery(id+"F6.opPattern","COPY",FACE,{"derivedFrom":subQ1,"instanceName":"6"}),makeQuery(id+"F6.opPattern","COPY",FACE,{"derivedFrom":subQ1,"instanceName":"7"}),makeQuery(id+"F6.opPattern","COPY",FACE,{"derivedFrom":subQ1,"instanceName":"8"}),makeQuery(id+"F6.opPattern","COPY",FACE,{"derivedFrom":subQ1,"instanceName":"9"}),makeQuery(id+"F6.opPattern","COPY",FACE,{"derivedFrom":subQ1,"instanceName":"10"}),makeQuery(id+"F6.opPattern","COPY",FACE,{"derivedFrom":subQ1,"instanceName":"11"}),makeQuery(id+"F6.opPattern","COPY",FACE,{"derivedFrom":subQ1,"instanceName":"12"}),makeQuery(id+"F6.opPattern","COPY",FACE,{"derivedFrom":subQ1,"instanceName":"13"}),makeQuery(id+"F6.opPattern","COPY",FACE,{"derivedFrom":subQ1,"instanceName":"14"}),makeQuery(id+"F6.opPattern","COPY",FACE,{"derivedFrom":subQ1,"instanceName":"15"}),makeQuery(id+"F6.opPattern","COPY",FACE,{"derivedFrom":subQ1,"instanceName":"16"}),makeQuery(id+"F6.opPattern","COPY",FACE,{"derivedFrom":subQ1,"instanceName":"17"}),makeQuery(id+"F6.opPattern","COPY",FACE,{"derivedFrom":subQ1,"instanceName":"18"}),makeQuery(id+"F6.opPattern","COPY",FACE,{"derivedFrom":subQ1,"instanceName":"19"}),makeQuery(id+"F6.opPattern","COPY",FACE,{"derivedFrom":subQ1,"instanceName":"20"}),makeQuery(id+"F6.opPattern","COPY",FACE,{"derivedFrom":subQ1,"instanceName":"21"}),makeQuery(id+"F6.opPattern","COPY",FACE,{"derivedFrom":subQ1,"instanceName":"22"}),makeQuery(id+"F6.opPattern","COPY",FACE,{"derivedFrom":subQ1,"instanceName":"23"}),makeQuery(id+"F6.opPattern","COPY",FACE,{"derivedFrom":subQ1,"instanceName":"24"}),makeQuery(id+"F6.opPattern","COPY",FACE,{"derivedFrom":subQ1,"instanceName":"25"}),makeQuery(id+"F6.opPattern","COPY",FACE,{"derivedFrom":subQ1,"instanceName":"26"}),makeQuery(id+"F6.opPattern","COPY",FACE,{"derivedFrom":subQ1,"instanceName":"27"}),makeQuery(id+"F6.opPattern","COPY",FACE,{"derivedFrom":subQ1,"instanceName":"28"}),makeQuery(id+"F6.opPattern","COPY",FACE,{"derivedFrom":subQ1,"instanceName":"29"}),makeQuery(id+"F6.opPattern","COPY",FACE,{"derivedFrom":subQ1,"instanceName":"30"}),makeQuery(id+"F6.opPattern","COPY",FACE,{"derivedFrom":subQ1,"instanceName":"31"}),makeQuery(id+"F6.opPattern","COPY",FACE,{"derivedFrom":subQ1,"instanceName":"32"}),makeQuery(id+"F6.opPattern","COPY",FACE,{"derivedFrom":subQ1,"instanceName":"33"}),makeQuery(id+"F6.opPattern","COPY",FACE,{"derivedFrom":subQ1,"instanceName":"34"}),makeQuery(id+"F6.opPattern","COPY",FACE,{"derivedFrom":subQ1,"instanceName":"35"}),makeQuery(id+"F6.opPattern","COPY",FACE,{"derivedFrom":subQ1,"instanceName":"36"}),makeQuery(id+"F6.opPattern","COPY",FACE,{"derivedFrom":subQ1,"instanceName":"37"}),makeQuery(id+"F6.opPattern","COPY",FACE,{"derivedFrom":subQ1,"instanceName":"38"}),makeQuery(id+"F6.opPattern","COPY",FACE,{"derivedFrom":subQ1,"instanceName":"39"}),makeQuery(id+"F6.opPattern","COPY",FACE,{"derivedFrom":subQ1,"instanceName":"40"}),makeQuery(id+"F6.opPattern","COPY",FACE,{"derivedFrom":subQ1,"instanceName":"41"}),makeQuery(id+"F6.opPattern","COPY",FACE,{"derivedFrom":subQ1,"instanceName":"42"}),makeQuery(id+"F6.opPattern","COPY",FACE,{"derivedFrom":subQ1,"instanceName":"43"}),makeQuery(id+"F6.opPattern","COPY",FACE,{"derivedFrom":subQ1,"instanceName":"44"}),makeQuery(id+"F6.opPattern","COPY",FACE,{"derivedFrom":subQ1,"instanceName":"45"}),makeQuery(id+"F6.opPattern","COPY",FACE,{"derivedFrom":subQ1,"instanceName":"46"}),makeQuery(id+"F6.opPattern","COPY",FACE,{"derivedFrom":subQ1,"instanceName":"47"}),makeQuery(id+"F6.opPattern","COPY",FACE,{"derivedFrom":subQ1,"instanceName":"48"}),makeQuery(id+"F6.opPattern","COPY",FACE,{"derivedFrom":subQ1,"instanceName":"49"}),makeQuery(id+"F6.opPattern","COPY",FACE,{"derivedFrom":subQ1,"instanceName":"50"}),makeQuery(id+"F6.opPattern","COPY",FACE,{"derivedFrom":subQ1,"instanceName":"51"}),makeQuery(id+"F6.opPattern","COPY",FACE,{"derivedFrom":subQ1,"instanceName":"52"}),makeQuery(id+"F6.opPattern","COPY",FACE,{"derivedFrom":subQ1,"instanceName":"53"}),makeQuery(id+"F6.opPattern","COPY",FACE,{"derivedFrom":subQ1,"instanceName":"54"}),makeQuery(id+"F6.opPattern","COPY",FACE,{"derivedFrom":subQ1,"instanceName":"55"}),makeQuery(id+"F6.opPattern","COPY",FACE,{"derivedFrom":subQ1,"instanceName":"56"}),makeQuery(id+"F6.opPattern","COPY",FACE,{"derivedFrom":subQ1,"instanceName":"57"}),makeQuery(id+"F6.opPattern","COPY",FACE,{"derivedFrom":subQ1,"instanceName":"58"}),makeQuery(id+"F6.opPattern","COPY",FACE,{"derivedFrom":subQ1,"instanceName":"59"}),makeQuery(id+"F6.opPattern","COPY",FACE,{"derivedFrom":subQ1,"instanceName":"60"}),makeQuery(id+"F6.opPattern","COPY",FACE,{"derivedFrom":subQ1,"instanceName":"61"}),makeQuery(id+"F6.opPattern","COPY",FACE,{"derivedFrom":subQ1,"instanceName":"62"}),makeQuery(id+"F6.opPattern","COPY",FACE,{"derivedFrom":subQ1,"instanceName":"63"}),makeQuery(id+"F6.opPattern","COPY",FACE,{"derivedFrom":subQ1,"instanceName":"64"}),makeQuery(id+"F6.opPattern","COPY",FACE,{"derivedFrom":subQ1,"instanceName":"65"}),makeQuery(id+"F6.opPattern","COPY",FACE,{"derivedFrom":subQ1,"instanceName":"66"}),makeQuery(id+"F6.opPattern","COPY",FACE,{"derivedFrom":subQ1,"instanceName":"67"}),makeQuery(id+"F6.opPattern","COPY",FACE,{"derivedFrom":subQ1,"instanceName":"68"}),makeQuery(id+"F6.opPattern","COPY",FACE,{"derivedFrom":subQ1,"instanceName":"69"}),makeQuery(id+"F6.opPattern","COPY",FACE,{"derivedFrom":subQ1,"instanceName":"70"}),makeQuery(id+"F6.opPattern","COPY",FACE,{"derivedFrom":subQ1,"instanceName":"71"}),makeQuery(id+"F6.opPattern","COPY",FACE,{"derivedFrom":subQ1,"instanceName":"72"}),makeQuery(id+"F6.opPattern","COPY",FACE,{"derivedFrom":subQ1,"instanceName":"73"}),makeQuery(id+"F6.opPattern","COPY",FACE,{"derivedFrom":subQ1,"instanceName":"74"}),makeQuery(id+"F6.opPattern","COPY",FACE,{"derivedFrom":subQ1,"instanceName":"75"}),makeQuery(id+"F6.opPattern","COPY",FACE,{"derivedFrom":subQ1,"instanceName":"76"}),makeQuery(id+"F6.opPattern","COPY",FACE,{"derivedFrom":subQ1,"instanceName":"77"}),makeQuery(id+"F6.opPattern","COPY",FACE,{"derivedFrom":subQ1,"instanceName":"78"})]});Q9=makeQuery(id+"F9.opChamfer","BLEND_EDGE",EDGE,{"blendedFrom":[makeQuery(id+"F8.boolean.opBoolean","INTERSECT",EDGE,{"derivedFrom":[subQ2,makeQuery(id+"F8.opExtrude","SWEPT_FACE",FACE,{"disambiguationData":[OSD([sQuery(id+"F7.wireOp",EDGE,"E16.1.3.0")])]})]}),subQ2],"blendedInto":[subQ2]});}
            var Q10;
            {var subQ0=sQuery(id+"F2.wireOp",EDGE,"E0");var subQ1=makeQuery(id+"F5.boolean.opBoolean","MERGE",FACE,{"derivedFrom":[makeQuery(id+"F4.opExtrude","CAP_FACE",FACE,{"disambiguationData":[OSD([subQ0])],"isStart":true}),makeQuery(id+"F5.opExtrude","CAP_FACE",FACE,{"disambiguationData":[OSD([subQ0,sQuery(id+"F2.wireOp",EDGE,"E1"),sQuery(id+"F2.wireOp",EDGE,"E2"),sQuery(id+"F2.wireOp",EDGE,"E3")])],"isStart":true})]});var subQ2=makeQuery(id+"F6.boolean.opBoolean","MERGE",FACE,{"derivedFrom":[subQ1,makeQuery(id+"F6.opPattern","COPY",FACE,{"derivedFrom":subQ1,"instanceName":"1"}),makeQuery(id+"F6.opPattern","COPY",FACE,{"derivedFrom":subQ1,"instanceName":"2"}),makeQuery(id+"F6.opPattern","COPY",FACE,{"derivedFrom":subQ1,"instanceName":"3"}),makeQuery(id+"F6.opPattern","COPY",FACE,{"derivedFrom":subQ1,"instanceName":"4"}),makeQuery(id+"F6.opPattern","COPY",FACE,{"derivedFrom":subQ1,"instanceName":"5"}),makeQuery(id+"F6.opPattern","COPY",FACE,{"derivedFrom":subQ1,"instanceName":"6"}),makeQuery(id+"F6.opPattern","COPY",FACE,{"derivedFrom":subQ1,"instanceName":"7"}),makeQuery(id+"F6.opPattern","COPY",FACE,{"derivedFrom":subQ1,"instanceName":"8"}),makeQuery(id+"F6.opPattern","COPY",FACE,{"derivedFrom":subQ1,"instanceName":"9"}),makeQuery(id+"F6.opPattern","COPY",FACE,{"derivedFrom":subQ1,"instanceName":"10"}),makeQuery(id+"F6.opPattern","COPY",FACE,{"derivedFrom":subQ1,"instanceName":"11"}),makeQuery(id+"F6.opPattern","COPY",FACE,{"derivedFrom":subQ1,"instanceName":"12"}),makeQuery(id+"F6.opPattern","COPY",FACE,{"derivedFrom":subQ1,"instanceName":"13"}),makeQuery(id+"F6.opPattern","COPY",FACE,{"derivedFrom":subQ1,"instanceName":"14"}),makeQuery(id+"F6.opPattern","COPY",FACE,{"derivedFrom":subQ1,"instanceName":"15"}),makeQuery(id+"F6.opPattern","COPY",FACE,{"derivedFrom":subQ1,"instanceName":"16"}),makeQuery(id+"F6.opPattern","COPY",FACE,{"derivedFrom":subQ1,"instanceName":"17"}),makeQuery(id+"F6.opPattern","COPY",FACE,{"derivedFrom":subQ1,"instanceName":"18"}),makeQuery(id+"F6.opPattern","COPY",FACE,{"derivedFrom":subQ1,"instanceName":"19"}),makeQuery(id+"F6.opPattern","COPY",FACE,{"derivedFrom":subQ1,"instanceName":"20"}),makeQuery(id+"F6.opPattern","COPY",FACE,{"derivedFrom":subQ1,"instanceName":"21"}),makeQuery(id+"F6.opPattern","COPY",FACE,{"derivedFrom":subQ1,"instanceName":"22"}),makeQuery(id+"F6.opPattern","COPY",FACE,{"derivedFrom":subQ1,"instanceName":"23"}),makeQuery(id+"F6.opPattern","COPY",FACE,{"derivedFrom":subQ1,"instanceName":"24"}),makeQuery(id+"F6.opPattern","COPY",FACE,{"derivedFrom":subQ1,"instanceName":"25"}),makeQuery(id+"F6.opPattern","COPY",FACE,{"derivedFrom":subQ1,"instanceName":"26"}),makeQuery(id+"F6.opPattern","COPY",FACE,{"derivedFrom":subQ1,"instanceName":"27"}),makeQuery(id+"F6.opPattern","COPY",FACE,{"derivedFrom":subQ1,"instanceName":"28"}),makeQuery(id+"F6.opPattern","COPY",FACE,{"derivedFrom":subQ1,"instanceName":"29"}),makeQuery(id+"F6.opPattern","COPY",FACE,{"derivedFrom":subQ1,"instanceName":"30"}),makeQuery(id+"F6.opPattern","COPY",FACE,{"derivedFrom":subQ1,"instanceName":"31"}),makeQuery(id+"F6.opPattern","COPY",FACE,{"derivedFrom":subQ1,"instanceName":"32"}),makeQuery(id+"F6.opPattern","COPY",FACE,{"derivedFrom":subQ1,"instanceName":"33"}),makeQuery(id+"F6.opPattern","COPY",FACE,{"derivedFrom":subQ1,"instanceName":"34"}),makeQuery(id+"F6.opPattern","COPY",FACE,{"derivedFrom":subQ1,"instanceName":"35"}),makeQuery(id+"F6.opPattern","COPY",FACE,{"derivedFrom":subQ1,"instanceName":"36"}),makeQuery(id+"F6.opPattern","COPY",FACE,{"derivedFrom":subQ1,"instanceName":"37"}),makeQuery(id+"F6.opPattern","COPY",FACE,{"derivedFrom":subQ1,"instanceName":"38"}),makeQuery(id+"F6.opPattern","COPY",FACE,{"derivedFrom":subQ1,"instanceName":"39"}),makeQuery(id+"F6.opPattern","COPY",FACE,{"derivedFrom":subQ1,"instanceName":"40"}),makeQuery(id+"F6.opPattern","COPY",FACE,{"derivedFrom":subQ1,"instanceName":"41"}),makeQuery(id+"F6.opPattern","COPY",FACE,{"derivedFrom":subQ1,"instanceName":"42"}),makeQuery(id+"F6.opPattern","COPY",FACE,{"derivedFrom":subQ1,"instanceName":"43"}),makeQuery(id+"F6.opPattern","COPY",FACE,{"derivedFrom":subQ1,"instanceName":"44"}),makeQuery(id+"F6.opPattern","COPY",FACE,{"derivedFrom":subQ1,"instanceName":"45"}),makeQuery(id+"F6.opPattern","COPY",FACE,{"derivedFrom":subQ1,"instanceName":"46"}),makeQuery(id+"F6.opPattern","COPY",FACE,{"derivedFrom":subQ1,"instanceName":"47"}),makeQuery(id+"F6.opPattern","COPY",FACE,{"derivedFrom":subQ1,"instanceName":"48"}),makeQuery(id+"F6.opPattern","COPY",FACE,{"derivedFrom":subQ1,"instanceName":"49"}),makeQuery(id+"F6.opPattern","COPY",FACE,{"derivedFrom":subQ1,"instanceName":"50"}),makeQuery(id+"F6.opPattern","COPY",FACE,{"derivedFrom":subQ1,"instanceName":"51"}),makeQuery(id+"F6.opPattern","COPY",FACE,{"derivedFrom":subQ1,"instanceName":"52"}),makeQuery(id+"F6.opPattern","COPY",FACE,{"derivedFrom":subQ1,"instanceName":"53"}),makeQuery(id+"F6.opPattern","COPY",FACE,{"derivedFrom":subQ1,"instanceName":"54"}),makeQuery(id+"F6.opPattern","COPY",FACE,{"derivedFrom":subQ1,"instanceName":"55"}),makeQuery(id+"F6.opPattern","COPY",FACE,{"derivedFrom":subQ1,"instanceName":"56"}),makeQuery(id+"F6.opPattern","COPY",FACE,{"derivedFrom":subQ1,"instanceName":"57"}),makeQuery(id+"F6.opPattern","COPY",FACE,{"derivedFrom":subQ1,"instanceName":"58"}),makeQuery(id+"F6.opPattern","COPY",FACE,{"derivedFrom":subQ1,"instanceName":"59"}),makeQuery(id+"F6.opPattern","COPY",FACE,{"derivedFrom":subQ1,"instanceName":"60"}),makeQuery(id+"F6.opPattern","COPY",FACE,{"derivedFrom":subQ1,"instanceName":"61"}),makeQuery(id+"F6.opPattern","COPY",FACE,{"derivedFrom":subQ1,"instanceName":"62"}),makeQuery(id+"F6.opPattern","COPY",FACE,{"derivedFrom":subQ1,"instanceName":"63"}),makeQuery(id+"F6.opPattern","COPY",FACE,{"derivedFrom":subQ1,"instanceName":"64"}),makeQuery(id+"F6.opPattern","COPY",FACE,{"derivedFrom":subQ1,"instanceName":"65"}),makeQuery(id+"F6.opPattern","COPY",FACE,{"derivedFrom":subQ1,"instanceName":"66"}),makeQuery(id+"F6.opPattern","COPY",FACE,{"derivedFrom":subQ1,"instanceName":"67"}),makeQuery(id+"F6.opPattern","COPY",FACE,{"derivedFrom":subQ1,"instanceName":"68"}),makeQuery(id+"F6.opPattern","COPY",FACE,{"derivedFrom":subQ1,"instanceName":"69"}),makeQuery(id+"F6.opPattern","COPY",FACE,{"derivedFrom":subQ1,"instanceName":"70"}),makeQuery(id+"F6.opPattern","COPY",FACE,{"derivedFrom":subQ1,"instanceName":"71"}),makeQuery(id+"F6.opPattern","COPY",FACE,{"derivedFrom":subQ1,"instanceName":"72"}),makeQuery(id+"F6.opPattern","COPY",FACE,{"derivedFrom":subQ1,"instanceName":"73"}),makeQuery(id+"F6.opPattern","COPY",FACE,{"derivedFrom":subQ1,"instanceName":"74"}),makeQuery(id+"F6.opPattern","COPY",FACE,{"derivedFrom":subQ1,"instanceName":"75"}),makeQuery(id+"F6.opPattern","COPY",FACE,{"derivedFrom":subQ1,"instanceName":"76"}),makeQuery(id+"F6.opPattern","COPY",FACE,{"derivedFrom":subQ1,"instanceName":"77"}),makeQuery(id+"F6.opPattern","COPY",FACE,{"derivedFrom":subQ1,"instanceName":"78"})]});Q10=makeQuery(id+"F9.opChamfer","BLEND_EDGE",EDGE,{"blendedFrom":[makeQuery(id+"F8.boolean.opBoolean","INTERSECT",EDGE,{"derivedFrom":[subQ2,makeQuery(id+"F8.opExtrude","SWEPT_FACE",FACE,{"disambiguationData":[OSD([sQuery(id+"F7.wireOp",EDGE,"E16.1.4.0")])]})]}),subQ2],"blendedInto":[subQ2]});}
            var Q11;
            {var subQ0=sQuery(id+"F2.wireOp",EDGE,"E0");var subQ1=makeQuery(id+"F5.boolean.opBoolean","MERGE",FACE,{"derivedFrom":[makeQuery(id+"F4.opExtrude","CAP_FACE",FACE,{"disambiguationData":[OSD([subQ0])],"isStart":true}),makeQuery(id+"F5.opExtrude","CAP_FACE",FACE,{"disambiguationData":[OSD([subQ0,sQuery(id+"F2.wireOp",EDGE,"E1"),sQuery(id+"F2.wireOp",EDGE,"E2"),sQuery(id+"F2.wireOp",EDGE,"E3")])],"isStart":true})]});var subQ2=makeQuery(id+"F6.boolean.opBoolean","MERGE",FACE,{"derivedFrom":[subQ1,makeQuery(id+"F6.opPattern","COPY",FACE,{"derivedFrom":subQ1,"instanceName":"1"}),makeQuery(id+"F6.opPattern","COPY",FACE,{"derivedFrom":subQ1,"instanceName":"2"}),makeQuery(id+"F6.opPattern","COPY",FACE,{"derivedFrom":subQ1,"instanceName":"3"}),makeQuery(id+"F6.opPattern","COPY",FACE,{"derivedFrom":subQ1,"instanceName":"4"}),makeQuery(id+"F6.opPattern","COPY",FACE,{"derivedFrom":subQ1,"instanceName":"5"}),makeQuery(id+"F6.opPattern","COPY",FACE,{"derivedFrom":subQ1,"instanceName":"6"}),makeQuery(id+"F6.opPattern","COPY",FACE,{"derivedFrom":subQ1,"instanceName":"7"}),makeQuery(id+"F6.opPattern","COPY",FACE,{"derivedFrom":subQ1,"instanceName":"8"}),makeQuery(id+"F6.opPattern","COPY",FACE,{"derivedFrom":subQ1,"instanceName":"9"}),makeQuery(id+"F6.opPattern","COPY",FACE,{"derivedFrom":subQ1,"instanceName":"10"}),makeQuery(id+"F6.opPattern","COPY",FACE,{"derivedFrom":subQ1,"instanceName":"11"}),makeQuery(id+"F6.opPattern","COPY",FACE,{"derivedFrom":subQ1,"instanceName":"12"}),makeQuery(id+"F6.opPattern","COPY",FACE,{"derivedFrom":subQ1,"instanceName":"13"}),makeQuery(id+"F6.opPattern","COPY",FACE,{"derivedFrom":subQ1,"instanceName":"14"}),makeQuery(id+"F6.opPattern","COPY",FACE,{"derivedFrom":subQ1,"instanceName":"15"}),makeQuery(id+"F6.opPattern","COPY",FACE,{"derivedFrom":subQ1,"instanceName":"16"}),makeQuery(id+"F6.opPattern","COPY",FACE,{"derivedFrom":subQ1,"instanceName":"17"}),makeQuery(id+"F6.opPattern","COPY",FACE,{"derivedFrom":subQ1,"instanceName":"18"}),makeQuery(id+"F6.opPattern","COPY",FACE,{"derivedFrom":subQ1,"instanceName":"19"}),makeQuery(id+"F6.opPattern","COPY",FACE,{"derivedFrom":subQ1,"instanceName":"20"}),makeQuery(id+"F6.opPattern","COPY",FACE,{"derivedFrom":subQ1,"instanceName":"21"}),makeQuery(id+"F6.opPattern","COPY",FACE,{"derivedFrom":subQ1,"instanceName":"22"}),makeQuery(id+"F6.opPattern","COPY",FACE,{"derivedFrom":subQ1,"instanceName":"23"}),makeQuery(id+"F6.opPattern","COPY",FACE,{"derivedFrom":subQ1,"instanceName":"24"}),makeQuery(id+"F6.opPattern","COPY",FACE,{"derivedFrom":subQ1,"instanceName":"25"}),makeQuery(id+"F6.opPattern","COPY",FACE,{"derivedFrom":subQ1,"instanceName":"26"}),makeQuery(id+"F6.opPattern","COPY",FACE,{"derivedFrom":subQ1,"instanceName":"27"}),makeQuery(id+"F6.opPattern","COPY",FACE,{"derivedFrom":subQ1,"instanceName":"28"}),makeQuery(id+"F6.opPattern","COPY",FACE,{"derivedFrom":subQ1,"instanceName":"29"}),makeQuery(id+"F6.opPattern","COPY",FACE,{"derivedFrom":subQ1,"instanceName":"30"}),makeQuery(id+"F6.opPattern","COPY",FACE,{"derivedFrom":subQ1,"instanceName":"31"}),makeQuery(id+"F6.opPattern","COPY",FACE,{"derivedFrom":subQ1,"instanceName":"32"}),makeQuery(id+"F6.opPattern","COPY",FACE,{"derivedFrom":subQ1,"instanceName":"33"}),makeQuery(id+"F6.opPattern","COPY",FACE,{"derivedFrom":subQ1,"instanceName":"34"}),makeQuery(id+"F6.opPattern","COPY",FACE,{"derivedFrom":subQ1,"instanceName":"35"}),makeQuery(id+"F6.opPattern","COPY",FACE,{"derivedFrom":subQ1,"instanceName":"36"}),makeQuery(id+"F6.opPattern","COPY",FACE,{"derivedFrom":subQ1,"instanceName":"37"}),makeQuery(id+"F6.opPattern","COPY",FACE,{"derivedFrom":subQ1,"instanceName":"38"}),makeQuery(id+"F6.opPattern","COPY",FACE,{"derivedFrom":subQ1,"instanceName":"39"}),makeQuery(id+"F6.opPattern","COPY",FACE,{"derivedFrom":subQ1,"instanceName":"40"}),makeQuery(id+"F6.opPattern","COPY",FACE,{"derivedFrom":subQ1,"instanceName":"41"}),makeQuery(id+"F6.opPattern","COPY",FACE,{"derivedFrom":subQ1,"instanceName":"42"}),makeQuery(id+"F6.opPattern","COPY",FACE,{"derivedFrom":subQ1,"instanceName":"43"}),makeQuery(id+"F6.opPattern","COPY",FACE,{"derivedFrom":subQ1,"instanceName":"44"}),makeQuery(id+"F6.opPattern","COPY",FACE,{"derivedFrom":subQ1,"instanceName":"45"}),makeQuery(id+"F6.opPattern","COPY",FACE,{"derivedFrom":subQ1,"instanceName":"46"}),makeQuery(id+"F6.opPattern","COPY",FACE,{"derivedFrom":subQ1,"instanceName":"47"}),makeQuery(id+"F6.opPattern","COPY",FACE,{"derivedFrom":subQ1,"instanceName":"48"}),makeQuery(id+"F6.opPattern","COPY",FACE,{"derivedFrom":subQ1,"instanceName":"49"}),makeQuery(id+"F6.opPattern","COPY",FACE,{"derivedFrom":subQ1,"instanceName":"50"}),makeQuery(id+"F6.opPattern","COPY",FACE,{"derivedFrom":subQ1,"instanceName":"51"}),makeQuery(id+"F6.opPattern","COPY",FACE,{"derivedFrom":subQ1,"instanceName":"52"}),makeQuery(id+"F6.opPattern","COPY",FACE,{"derivedFrom":subQ1,"instanceName":"53"}),makeQuery(id+"F6.opPattern","COPY",FACE,{"derivedFrom":subQ1,"instanceName":"54"}),makeQuery(id+"F6.opPattern","COPY",FACE,{"derivedFrom":subQ1,"instanceName":"55"}),makeQuery(id+"F6.opPattern","COPY",FACE,{"derivedFrom":subQ1,"instanceName":"56"}),makeQuery(id+"F6.opPattern","COPY",FACE,{"derivedFrom":subQ1,"instanceName":"57"}),makeQuery(id+"F6.opPattern","COPY",FACE,{"derivedFrom":subQ1,"instanceName":"58"}),makeQuery(id+"F6.opPattern","COPY",FACE,{"derivedFrom":subQ1,"instanceName":"59"}),makeQuery(id+"F6.opPattern","COPY",FACE,{"derivedFrom":subQ1,"instanceName":"60"}),makeQuery(id+"F6.opPattern","COPY",FACE,{"derivedFrom":subQ1,"instanceName":"61"}),makeQuery(id+"F6.opPattern","COPY",FACE,{"derivedFrom":subQ1,"instanceName":"62"}),makeQuery(id+"F6.opPattern","COPY",FACE,{"derivedFrom":subQ1,"instanceName":"63"}),makeQuery(id+"F6.opPattern","COPY",FACE,{"derivedFrom":subQ1,"instanceName":"64"}),makeQuery(id+"F6.opPattern","COPY",FACE,{"derivedFrom":subQ1,"instanceName":"65"}),makeQuery(id+"F6.opPattern","COPY",FACE,{"derivedFrom":subQ1,"instanceName":"66"}),makeQuery(id+"F6.opPattern","COPY",FACE,{"derivedFrom":subQ1,"instanceName":"67"}),makeQuery(id+"F6.opPattern","COPY",FACE,{"derivedFrom":subQ1,"instanceName":"68"}),makeQuery(id+"F6.opPattern","COPY",FACE,{"derivedFrom":subQ1,"instanceName":"69"}),makeQuery(id+"F6.opPattern","COPY",FACE,{"derivedFrom":subQ1,"instanceName":"70"}),makeQuery(id+"F6.opPattern","COPY",FACE,{"derivedFrom":subQ1,"instanceName":"71"}),makeQuery(id+"F6.opPattern","COPY",FACE,{"derivedFrom":subQ1,"instanceName":"72"}),makeQuery(id+"F6.opPattern","COPY",FACE,{"derivedFrom":subQ1,"instanceName":"73"}),makeQuery(id+"F6.opPattern","COPY",FACE,{"derivedFrom":subQ1,"instanceName":"74"}),makeQuery(id+"F6.opPattern","COPY",FACE,{"derivedFrom":subQ1,"instanceName":"75"}),makeQuery(id+"F6.opPattern","COPY",FACE,{"derivedFrom":subQ1,"instanceName":"76"}),makeQuery(id+"F6.opPattern","COPY",FACE,{"derivedFrom":subQ1,"instanceName":"77"}),makeQuery(id+"F6.opPattern","COPY",FACE,{"derivedFrom":subQ1,"instanceName":"78"})]});Q11=makeQuery(id+"F9.opChamfer","BLEND_EDGE",EDGE,{"blendedFrom":[makeQuery(id+"F8.boolean.opBoolean","INTERSECT",EDGE,{"derivedFrom":[subQ2,makeQuery(id+"F8.opExtrude","SWEPT_FACE",FACE,{"disambiguationData":[OSD([sQuery(id+"F7.wireOp",EDGE,"E16.1.5.0")])]})]}),subQ2],"blendedInto":[subQ2]});}
            var Q12;
            Q12=makeQuery(id+"F8.boolean.opBoolean","COPY",FACE,{"derivedFrom":makeQuery(id+"F8.opExtrude","SWEPT_FACE",FACE,{"disambiguationData":[OSD([sQuery(id+"F7.wireOp",EDGE,"E16.1.3.0")])]})});
            var Q13;
            Q13=makeQuery(id+"F8.boolean.opBoolean","COPY",FACE,{"derivedFrom":makeQuery(id+"F8.opExtrude","SWEPT_FACE",FACE,{"disambiguationData":[OSD([sQuery(id+"F7.wireOp",EDGE,"E15.2.0")])]})});
            var Q14;
            Q14=makeQuery(id+"F8.boolean.opBoolean","COPY",FACE,{"derivedFrom":makeQuery(id+"F8.opExtrude","SWEPT_FACE",FACE,{"disambiguationData":[OSD([sQuery(id+"F7.wireOp",EDGE,"E15.1.0")])]})});
            var Q15;
            {var subQ0=sQuery(id+"F7.wireOp",EDGE,"E14");Q15=makeQuery(id+"F9.opChamfer","BLEND_EDGE",EDGE,{"blendedFrom":[makeQuery(id+"F8.boolean.opBoolean","COPY",EDGE,{"derivedFrom":makeQuery(id+"F8.opExtrude","CAP_EDGE",EDGE,{"disambiguationData":[OSD([subQ0])],"isStart":true})}),makeQuery(id+"F8.boolean.opBoolean","COPY",FACE,{"derivedFrom":makeQuery(id+"F8.opExtrude","SWEPT_FACE",FACE,{"disambiguationData":[OSD([subQ0])]})})],"blendedInto":[makeQuery(id+"F8.boolean.opBoolean","COPY",FACE,{"derivedFrom":makeQuery(id+"F8.opExtrude","SWEPT_FACE",FACE,{"disambiguationData":[OSD([subQ0])]})})]});}
            var Q16;
            Q16=makeQuery(id+"F8.boolean.opBoolean","COPY",FACE,{"derivedFrom":makeQuery(id+"F8.opExtrude","SWEPT_FACE",FACE,{"disambiguationData":[OSD([sQuery(id+"F7.wireOp",EDGE,"E16.1.5.0")])]})});
            var Q17;
            Q17=makeQuery(id+"F8.boolean.opBoolean","COPY",FACE,{"derivedFrom":makeQuery(id+"F8.opExtrude","SWEPT_FACE",FACE,{"disambiguationData":[OSD([sQuery(id+"F7.wireOp",EDGE,"E16.1.4.0")])]})});
            fillet(context, id + "F10", {"entities" : qUnion([Q0, Q1, Q2, Q3, Q4, Q5, Q6, Q7, Q8, Q9, Q10, Q11, Q12, Q13, Q14, Q15, Q16, Q17]), "radius" : .5 * mm, "tangentPropagation" : true, "allowEdgeOverflow" : false});
        }
    });
